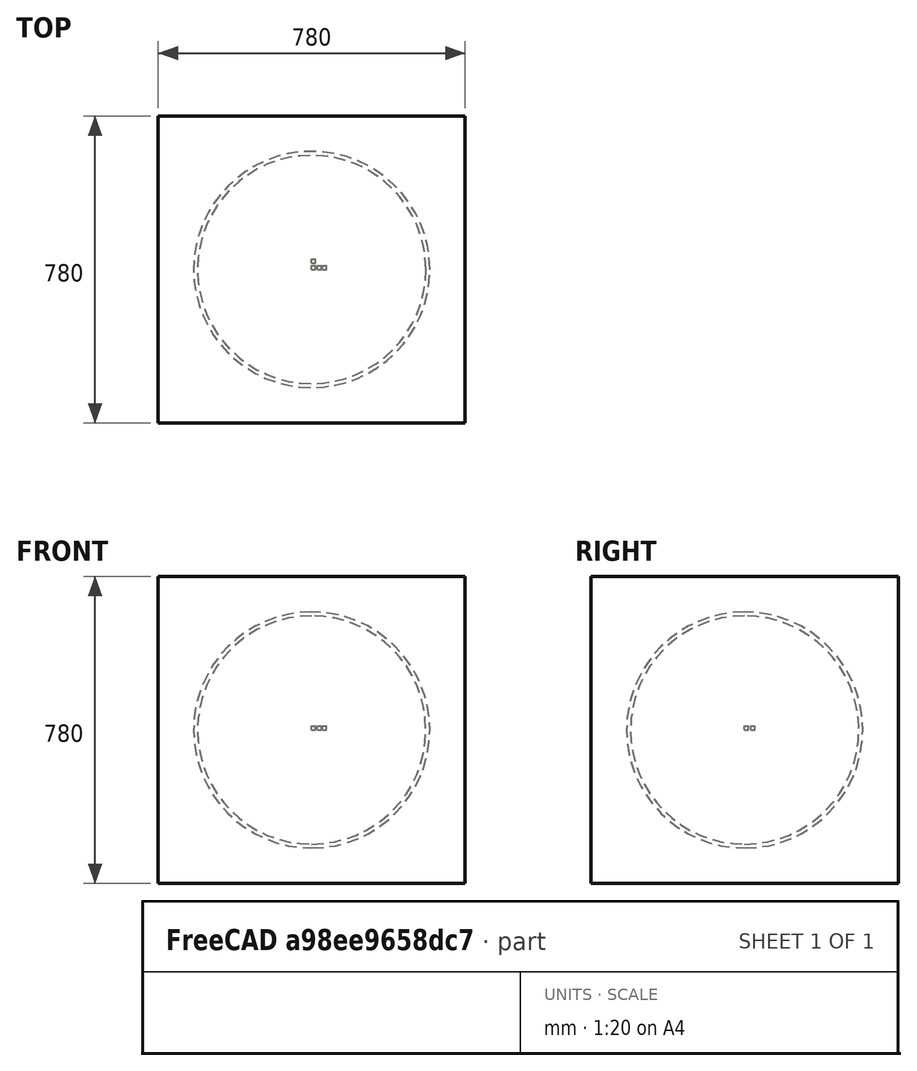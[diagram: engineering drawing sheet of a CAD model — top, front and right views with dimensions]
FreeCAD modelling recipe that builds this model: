
FCSTD DOCUMENT  (FreeCAD 0.20RUnknown)
Label: myTestExperiment_equivalent
License: All rights reserved
objects: App::DocumentObjectGroupPython×1251, App::Part×7, Part::FeaturePython×6, Part::Box×4
note: 6 computed .brp shape members not serialized (recipe doc carries the construction recipe); baked Part::Feature solids carry a one-line shape summary decoded from their .brp

FEATURE [App::DocumentObjectGroupPython] HALFPI  # scripted group (container) (typed FeaturePython)
  name = HALFPI
  value = pi/2.
FEATURE [App::DocumentObjectGroupPython] PI  # scripted group (container) (typed FeaturePython)
  name = PI
  value = 1.*pi
FEATURE [App::DocumentObjectGroupPython] TWOPI  # scripted group (container) (typed FeaturePython)
  name = TWOPI
  value = 2.*pi
FEATURE [App::DocumentObjectGroupPython] Constants  # scripted group (container) (typed FeaturePython)
  Group = -> [HALFPI,PI,TWOPI]
FEATURE [App::DocumentObjectGroupPython] Variables  # scripted group (container) (typed FeaturePython)
FEATURE [App::DocumentObjectGroupPython] Quantities  # scripted group (container) (typed FeaturePython)
FEATURE [App::DocumentObjectGroupPython] Isotopes  # scripted group (container) (typed FeaturePython)
FEATURE [App::DocumentObjectGroupPython] Elements  # scripted group (container) (typed FeaturePython)
FEATURE [App::DocumentObjectGroupPython] Matrix  # scripted group (container) (typed FeaturePython)
FEATURE [App::DocumentObjectGroupPython] Surfaces  # scripted group (container) (typed FeaturePython)
FEATURE [App::DocumentObjectGroupPython] Opticals  # scripted group (container) (typed FeaturePython)
  Group = -> [Matrix,Surfaces]
FEATURE [App::DocumentObjectGroupPython] G4Isotopes  # scripted group (container) (typed FeaturePython)
FEATURE [App::DocumentObjectGroupPython] H_element  # scripted group (container) (typed FeaturePython)
  Z = 1
  atom_value = 1.008
  formula = H
  name = H_element
FEATURE [App::DocumentObjectGroupPython] He_element  # scripted group (container) (typed FeaturePython)
  Z = 2
  atom_value = 4.0026
  formula = He
  name = He_element
FEATURE [App::DocumentObjectGroupPython] Li_element  # scripted group (container) (typed FeaturePython)
  Z = 3
  atom_value = 6.94
  formula = Li
  name = Li_element
FEATURE [App::DocumentObjectGroupPython] Be_element  # scripted group (container) (typed FeaturePython)
  Z = 4
  atom_value = 9.01218
  formula = Be
  name = Be_element
FEATURE [App::DocumentObjectGroupPython] B_element  # scripted group (container) (typed FeaturePython)
  Z = 5
  atom_value = 10.81
  formula = B
  name = B_element
FEATURE [App::DocumentObjectGroupPython] C_element  # scripted group (container) (typed FeaturePython)
  Z = 6
  atom_value = 12.011
  formula = C
  name = C_element
FEATURE [App::DocumentObjectGroupPython] N_element  # scripted group (container) (typed FeaturePython)
  Z = 7
  atom_value = 14.007
  formula = N
  name = N_element
FEATURE [App::DocumentObjectGroupPython] O_element  # scripted group (container) (typed FeaturePython)
  Z = 8
  atom_value = 15.999
  formula = O
  name = O_element
FEATURE [App::DocumentObjectGroupPython] F_element  # scripted group (container) (typed FeaturePython)
  Z = 9
  atom_value = 18.9984
  formula = F
  name = F_element
FEATURE [App::DocumentObjectGroupPython] Ne_element  # scripted group (container) (typed FeaturePython)
  Z = 10
  atom_value = 20.1797
  formula = Ne
  name = Ne_element
FEATURE [App::DocumentObjectGroupPython] Na_element  # scripted group (container) (typed FeaturePython)
  Z = 11
  atom_value = 22.9898
  formula = Na
  name = Na_element
FEATURE [App::DocumentObjectGroupPython] Mg_element  # scripted group (container) (typed FeaturePython)
  Z = 12
  atom_value = 24.305
  formula = Mg
  name = Mg_element
FEATURE [App::DocumentObjectGroupPython] Al_element  # scripted group (container) (typed FeaturePython)
  Z = 13
  atom_value = 26.9815
  formula = Al
  name = Al_element
FEATURE [App::DocumentObjectGroupPython] Si_element  # scripted group (container) (typed FeaturePython)
  Z = 14
  atom_value = 28.085
  formula = Si
  name = Si_element
FEATURE [App::DocumentObjectGroupPython] P_element  # scripted group (container) (typed FeaturePython)
  Z = 15
  atom_value = 30.9738
  formula = P
  name = P_element
FEATURE [App::DocumentObjectGroupPython] S_element  # scripted group (container) (typed FeaturePython)
  Z = 16
  atom_value = 32.06
  formula = S
  name = S_element
FEATURE [App::DocumentObjectGroupPython] Cl_element  # scripted group (container) (typed FeaturePython)
  Z = 17
  atom_value = 35.45
  formula = Cl
  name = Cl_element
FEATURE [App::DocumentObjectGroupPython] Ar_element  # scripted group (container) (typed FeaturePython)
  Z = 18
  atom_value = 39.95
  formula = Ar
  name = Ar_element
FEATURE [App::DocumentObjectGroupPython] K_element  # scripted group (container) (typed FeaturePython)
  Z = 19
  atom_value = 39.0983
  formula = K
  name = K_element
FEATURE [App::DocumentObjectGroupPython] Ca_element  # scripted group (container) (typed FeaturePython)
  Z = 20
  atom_value = 40.078
  formula = Ca
  name = Ca_element
FEATURE [App::DocumentObjectGroupPython] Sc_element  # scripted group (container) (typed FeaturePython)
  Z = 21
  atom_value = 44.9559
  formula = Sc
  name = Sc_element
FEATURE [App::DocumentObjectGroupPython] Ti_element  # scripted group (container) (typed FeaturePython)
  Z = 22
  atom_value = 47.867
  formula = Ti
  name = Ti_element
FEATURE [App::DocumentObjectGroupPython] V_element  # scripted group (container) (typed FeaturePython)
  Z = 23
  atom_value = 50.9415
  formula = V
  name = V_element
FEATURE [App::DocumentObjectGroupPython] Cr_element  # scripted group (container) (typed FeaturePython)
  Z = 24
  atom_value = 51.9961
  formula = Cr
  name = Cr_element
FEATURE [App::DocumentObjectGroupPython] Mn_element  # scripted group (container) (typed FeaturePython)
  Z = 25
  atom_value = 54.938
  formula = Mn
  name = Mn_element
FEATURE [App::DocumentObjectGroupPython] Fe_element  # scripted group (container) (typed FeaturePython)
  Z = 26
  atom_value = 55.845
  formula = Fe
  name = Fe_element
FEATURE [App::DocumentObjectGroupPython] Co_element  # scripted group (container) (typed FeaturePython)
  Z = 27
  atom_value = 58.9332
  formula = Co
  name = Co_element
FEATURE [App::DocumentObjectGroupPython] Ni_element  # scripted group (container) (typed FeaturePython)
  Z = 28
  atom_value = 58.6934
  formula = Ni
  name = Ni_element
FEATURE [App::DocumentObjectGroupPython] Cu_element  # scripted group (container) (typed FeaturePython)
  Z = 29
  atom_value = 63.546
  formula = Cu
  name = Cu_element
FEATURE [App::DocumentObjectGroupPython] Zn_element  # scripted group (container) (typed FeaturePython)
  Z = 30
  atom_value = 65.38
  formula = Zn
  name = Zn_element
FEATURE [App::DocumentObjectGroupPython] Ga_element  # scripted group (container) (typed FeaturePython)
  Z = 31
  atom_value = 69.723
  formula = Ga
  name = Ga_element
FEATURE [App::DocumentObjectGroupPython] Ge_element  # scripted group (container) (typed FeaturePython)
  Z = 32
  atom_value = 72.63
  formula = Ge
  name = Ge_element
FEATURE [App::DocumentObjectGroupPython] As_element  # scripted group (container) (typed FeaturePython)
  Z = 33
  atom_value = 74.9216
  formula = As
  name = As_element
FEATURE [App::DocumentObjectGroupPython] Se_element  # scripted group (container) (typed FeaturePython)
  Z = 34
  atom_value = 78.971
  formula = Se
  name = Se_element
FEATURE [App::DocumentObjectGroupPython] Br_element  # scripted group (container) (typed FeaturePython)
  Z = 35
  atom_value = 79.904
  formula = Br
  name = Br_element
FEATURE [App::DocumentObjectGroupPython] Kr_element  # scripted group (container) (typed FeaturePython)
  Z = 36
  atom_value = 83.798
  formula = Kr
  name = Kr_element
FEATURE [App::DocumentObjectGroupPython] Rb_element  # scripted group (container) (typed FeaturePython)
  Z = 37
  atom_value = 85.4678
  formula = Rb
  name = Rb_element
FEATURE [App::DocumentObjectGroupPython] Sr_element  # scripted group (container) (typed FeaturePython)
  Z = 38
  atom_value = 87.62
  formula = Sr
  name = Sr_element
FEATURE [App::DocumentObjectGroupPython] Y_element  # scripted group (container) (typed FeaturePython)
  Z = 39
  atom_value = 88.9058
  formula = Y
  name = Y_element
FEATURE [App::DocumentObjectGroupPython] Zr_element  # scripted group (container) (typed FeaturePython)
  Z = 40
  atom_value = 91.224
  formula = Zr
  name = Zr_element
FEATURE [App::DocumentObjectGroupPython] Nb_element  # scripted group (container) (typed FeaturePython)
  Z = 41
  atom_value = 92.9064
  formula = Nb
  name = Nb_element
FEATURE [App::DocumentObjectGroupPython] Mo_element  # scripted group (container) (typed FeaturePython)
  Z = 42
  atom_value = 95.95
  formula = Mo
  name = Mo_element
FEATURE [App::DocumentObjectGroupPython] Tc_element  # scripted group (container) (typed FeaturePython)
  Z = 43
  atom_value = 97
  formula = Tc
  name = Tc_element
FEATURE [App::DocumentObjectGroupPython] Ru_element  # scripted group (container) (typed FeaturePython)
  Z = 44
  atom_value = 101.07
  formula = Ru
  name = Ru_element
FEATURE [App::DocumentObjectGroupPython] Rh_element  # scripted group (container) (typed FeaturePython)
  Z = 45
  atom_value = 102.905
  formula = Rh
  name = Rh_element
FEATURE [App::DocumentObjectGroupPython] Pd_element  # scripted group (container) (typed FeaturePython)
  Z = 46
  atom_value = 106.42
  formula = Pd
  name = Pd_element
FEATURE [App::DocumentObjectGroupPython] Ag_element  # scripted group (container) (typed FeaturePython)
  Z = 47
  atom_value = 107.868
  formula = Ag
  name = Ag_element
FEATURE [App::DocumentObjectGroupPython] Cd_element  # scripted group (container) (typed FeaturePython)
  Z = 48
  atom_value = 112.414
  formula = Cd
  name = Cd_element
FEATURE [App::DocumentObjectGroupPython] In_element  # scripted group (container) (typed FeaturePython)
  Z = 49
  atom_value = 114.818
  formula = In
  name = In_element
FEATURE [App::DocumentObjectGroupPython] Sn_element  # scripted group (container) (typed FeaturePython)
  Z = 50
  atom_value = 118.71
  formula = Sn
  name = Sn_element
FEATURE [App::DocumentObjectGroupPython] Sb_element  # scripted group (container) (typed FeaturePython)
  Z = 51
  atom_value = 121.76
  formula = Sb
  name = Sb_element
FEATURE [App::DocumentObjectGroupPython] Te_element  # scripted group (container) (typed FeaturePython)
  Z = 52
  atom_value = 127.6
  formula = Te
  name = Te_element
FEATURE [App::DocumentObjectGroupPython] I_element  # scripted group (container) (typed FeaturePython)
  Z = 53
  atom_value = 126.904
  formula = I
  name = I_element
FEATURE [App::DocumentObjectGroupPython] Xe_element  # scripted group (container) (typed FeaturePython)
  Z = 54
  atom_value = 131.293
  formula = Xe
  name = Xe_element
FEATURE [App::DocumentObjectGroupPython] Cs_element  # scripted group (container) (typed FeaturePython)
  Z = 55
  atom_value = 132.905
  formula = Cs
  name = Cs_element
FEATURE [App::DocumentObjectGroupPython] Ba_element  # scripted group (container) (typed FeaturePython)
  Z = 56
  atom_value = 137.327
  formula = Ba
  name = Ba_element
FEATURE [App::DocumentObjectGroupPython] La_element  # scripted group (container) (typed FeaturePython)
  Z = 57
  atom_value = 138.905
  formula = La
  name = La_element
FEATURE [App::DocumentObjectGroupPython] Ce_element  # scripted group (container) (typed FeaturePython)
  Z = 58
  atom_value = 140.116
  formula = Ce
  name = Ce_element
FEATURE [App::DocumentObjectGroupPython] Pr_element  # scripted group (container) (typed FeaturePython)
  Z = 59
  atom_value = 140.908
  formula = Pr
  name = Pr_element
FEATURE [App::DocumentObjectGroupPython] Nd_element  # scripted group (container) (typed FeaturePython)
  Z = 60
  atom_value = 144.242
  formula = Nd
  name = Nd_element
FEATURE [App::DocumentObjectGroupPython] Pm_element  # scripted group (container) (typed FeaturePython)
  Z = 61
  atom_value = 145
  formula = Pm
  name = Pm_element
FEATURE [App::DocumentObjectGroupPython] Sm_element  # scripted group (container) (typed FeaturePython)
  Z = 62
  atom_value = 150.36
  formula = Sm
  name = Sm_element
FEATURE [App::DocumentObjectGroupPython] Eu_element  # scripted group (container) (typed FeaturePython)
  Z = 63
  atom_value = 151.964
  formula = Eu
  name = Eu_element
FEATURE [App::DocumentObjectGroupPython] Gd_element  # scripted group (container) (typed FeaturePython)
  Z = 64
  atom_value = 157.25
  formula = Gd
  name = Gd_element
FEATURE [App::DocumentObjectGroupPython] Tb_element  # scripted group (container) (typed FeaturePython)
  Z = 65
  atom_value = 158.925
  formula = Tb
  name = Tb_element
FEATURE [App::DocumentObjectGroupPython] Dy_element  # scripted group (container) (typed FeaturePython)
  Z = 66
  atom_value = 162.5
  formula = Dy
  name = Dy_element
FEATURE [App::DocumentObjectGroupPython] Ho_element  # scripted group (container) (typed FeaturePython)
  Z = 67
  atom_value = 164.93
  formula = Ho
  name = Ho_element
FEATURE [App::DocumentObjectGroupPython] Er_element  # scripted group (container) (typed FeaturePython)
  Z = 68
  atom_value = 167.259
  formula = Er
  name = Er_element
FEATURE [App::DocumentObjectGroupPython] Tm_element  # scripted group (container) (typed FeaturePython)
  Z = 69
  atom_value = 168.934
  formula = Tm
  name = Tm_element
FEATURE [App::DocumentObjectGroupPython] Yb_element  # scripted group (container) (typed FeaturePython)
  Z = 70
  atom_value = 173.045
  formula = Yb
  name = Yb_element
FEATURE [App::DocumentObjectGroupPython] Lu_element  # scripted group (container) (typed FeaturePython)
  Z = 71
  atom_value = 174.967
  formula = Lu
  name = Lu_element
FEATURE [App::DocumentObjectGroupPython] Hf_element  # scripted group (container) (typed FeaturePython)
  Z = 72
  atom_value = 178.49
  formula = Hf
  name = Hf_element
FEATURE [App::DocumentObjectGroupPython] Ta_element  # scripted group (container) (typed FeaturePython)
  Z = 73
  atom_value = 180.948
  formula = Ta
  name = Ta_element
FEATURE [App::DocumentObjectGroupPython] W_element  # scripted group (container) (typed FeaturePython)
  Z = 74
  atom_value = 183.84
  formula = W
  name = W_element
FEATURE [App::DocumentObjectGroupPython] Re_element  # scripted group (container) (typed FeaturePython)
  Z = 75
  atom_value = 186.207
  formula = Re
  name = Re_element
FEATURE [App::DocumentObjectGroupPython] Os_element  # scripted group (container) (typed FeaturePython)
  Z = 76
  atom_value = 190.23
  formula = Os
  name = Os_element
FEATURE [App::DocumentObjectGroupPython] Ir_element  # scripted group (container) (typed FeaturePython)
  Z = 77
  atom_value = 192.217
  formula = Ir
  name = Ir_element
FEATURE [App::DocumentObjectGroupPython] Pt_element  # scripted group (container) (typed FeaturePython)
  Z = 78
  atom_value = 195.084
  formula = Pt
  name = Pt_element
FEATURE [App::DocumentObjectGroupPython] Au_element  # scripted group (container) (typed FeaturePython)
  Z = 79
  atom_value = 196.967
  formula = Au
  name = Au_element
FEATURE [App::DocumentObjectGroupPython] Hg_element  # scripted group (container) (typed FeaturePython)
  Z = 80
  atom_value = 200.592
  formula = Hg
  name = Hg_element
FEATURE [App::DocumentObjectGroupPython] Tl_element  # scripted group (container) (typed FeaturePython)
  Z = 81
  atom_value = 204.38
  formula = Tl
  name = Tl_element
FEATURE [App::DocumentObjectGroupPython] Pb_element  # scripted group (container) (typed FeaturePython)
  Z = 82
  atom_value = 207.2
  formula = Pb
  name = Pb_element
FEATURE [App::DocumentObjectGroupPython] Bi_element  # scripted group (container) (typed FeaturePython)
  Z = 83
  atom_value = 208.98
  formula = Bi
  name = Bi_element
FEATURE [App::DocumentObjectGroupPython] Po_element  # scripted group (container) (typed FeaturePython)
  Z = 84
  atom_value = 209
  formula = Po
  name = Po_element
FEATURE [App::DocumentObjectGroupPython] At_element  # scripted group (container) (typed FeaturePython)
  Z = 85
  atom_value = 210
  formula = At
  name = At_element
FEATURE [App::DocumentObjectGroupPython] Rn_element  # scripted group (container) (typed FeaturePython)
  Z = 86
  atom_value = 222
  formula = Rn
  name = Rn_element
FEATURE [App::DocumentObjectGroupPython] Fr_element  # scripted group (container) (typed FeaturePython)
  Z = 87
  atom_value = 223
  formula = Fr
  name = Fr_element
FEATURE [App::DocumentObjectGroupPython] Ra_element  # scripted group (container) (typed FeaturePython)
  Z = 88
  atom_value = 226
  formula = Ra
  name = Ra_element
FEATURE [App::DocumentObjectGroupPython] Ac_element  # scripted group (container) (typed FeaturePython)
  Z = 89
  atom_value = 227
  formula = Ac
  name = Ac_element
FEATURE [App::DocumentObjectGroupPython] Th_element  # scripted group (container) (typed FeaturePython)
  Z = 90
  atom_value = 232.038
  formula = Th
  name = Th_element
FEATURE [App::DocumentObjectGroupPython] Pa_element  # scripted group (container) (typed FeaturePython)
  Z = 91
  atom_value = 231.036
  formula = Pa
  name = Pa_element
FEATURE [App::DocumentObjectGroupPython] U_element  # scripted group (container) (typed FeaturePython)
  Z = 92
  atom_value = 238.029
  formula = U
  name = U_element
FEATURE [App::DocumentObjectGroupPython] Np_element  # scripted group (container) (typed FeaturePython)
  Z = 93
  atom_value = 237
  formula = Np
  name = Np_element
FEATURE [App::DocumentObjectGroupPython] Pu_element  # scripted group (container) (typed FeaturePython)
  Z = 94
  atom_value = 244
  formula = Pu
  name = Pu_element
FEATURE [App::DocumentObjectGroupPython] Am_element  # scripted group (container) (typed FeaturePython)
  Z = 95
  atom_value = 243
  formula = Am
  name = Am_element
FEATURE [App::DocumentObjectGroupPython] Cm_element  # scripted group (container) (typed FeaturePython)
  Z = 96
  atom_value = 247
  formula = Cm
  name = Cm_element
FEATURE [App::DocumentObjectGroupPython] Bk_element  # scripted group (container) (typed FeaturePython)
  Z = 97
  atom_value = 247
  formula = Bk
  name = Bk_element
FEATURE [App::DocumentObjectGroupPython] Cf_element  # scripted group (container) (typed FeaturePython)
  Z = 98
  atom_value = 251
  formula = Cf
  name = Cf_element
FEATURE [App::DocumentObjectGroupPython] G4Elements  # scripted group (container) (typed FeaturePython)
  Group = -> [H_element,He_element,Li_element,Be_element,B_element,C_element,N_element,O_element,F_element,Ne_element,Na_element,Mg_element,Al_element,Si_element,P_element,S_element,Cl_element,Ar_element,K_element,Ca_element,Sc_element,Ti_element,V_element,Cr_element,Mn_element,Fe_element,Co_element,Ni_element,Cu_element,Zn_element,Ga_element,Ge_element,As_element,Se_element,Br_element,Kr_element,Rb_element,+61 more]
FEATURE [App::DocumentObjectGroupPython] H_element001  label="H_element : 0.101"  # scripted group (container) (typed FeaturePython)
  n = 0.101327
FEATURE [App::DocumentObjectGroupPython] C_element001  label="C_element : 0.775"  # scripted group (container) (typed FeaturePython)
  n = 0.7755
FEATURE [App::DocumentObjectGroupPython] N_element001  label="N_element : 0.035"  # scripted group (container) (typed FeaturePython)
  n = 0.035057
FEATURE [App::DocumentObjectGroupPython] O_element001  label="O_element : 0.052"  # scripted group (container) (typed FeaturePython)
  n = 0.0523159
FEATURE [App::DocumentObjectGroupPython] F_element001  label="F_element : 0.017"  # scripted group (container) (typed FeaturePython)
  n = 0.017422
FEATURE [App::DocumentObjectGroupPython] Ca_element001  label="Ca_element : 0.018"  # scripted group (container) (typed FeaturePython)
  n = 0.018378
FEATURE [App::DocumentObjectGroupPython] G4_A_150_TISSUE  label="G4_A-150_TISSUE"  # scripted group (container) (typed FeaturePython)
  Dunit = g/cm3
  Dvalue = 1.127
  Group = -> [H_element001,C_element001,N_element001,O_element001,F_element001,Ca_element001]
  conduct = 2
  density = 1
  expand = 3
  formula = G4_A-150_TISSUE
  name = G4_A-150_TISSUE
  specific = 4
FEATURE [App::DocumentObjectGroupPython] C_element002  label="C_element : 3"  # scripted group (container) (typed FeaturePython)
  n = 3
  ref = C_element
FEATURE [App::DocumentObjectGroupPython] H_element002  label="H_element : 6"  # scripted group (container) (typed FeaturePython)
  n = 6
  ref = H_element
FEATURE [App::DocumentObjectGroupPython] O_element002  label="O_element : 1"  # scripted group (container) (typed FeaturePython)
  n = 1
  ref = O_element
FEATURE [App::DocumentObjectGroupPython] G4_ACETONE  # scripted group (container) (typed FeaturePython)
  Dunit = g/cm3
  Dvalue = 0.7899
  Group = -> [C_element002,H_element002,O_element002]
  conduct = 2
  density = 1
  expand = 3
  formula = G4_ACETONE
  name = G4_ACETONE
  specific = 4
FEATURE [App::DocumentObjectGroupPython] C_element003  label="C_element : 2"  # scripted group (container) (typed FeaturePython)
  n = 2
  ref = C_element
FEATURE [App::DocumentObjectGroupPython] H_element003  label="H_element : 2"  # scripted group (container) (typed FeaturePython)
  n = 2
  ref = H_element
FEATURE [App::DocumentObjectGroupPython] G4_ACETYLENE  # scripted group (container) (typed FeaturePython)
  Dunit = g/cm3
  Dvalue = 0.0010967
  Group = -> [C_element003,H_element003]
  conduct = 2
  density = 1
  expand = 3
  formula = G4_ACETYLENE
  name = G4_ACETYLENE
  specific = 4
FEATURE [App::DocumentObjectGroupPython] C_element004  label="C_element : 5"  # scripted group (container) (typed FeaturePython)
  n = 5
  ref = C_element
FEATURE [App::DocumentObjectGroupPython] H_element004  label="H_element : 5"  # scripted group (container) (typed FeaturePython)
  n = 5
  ref = H_element
FEATURE [App::DocumentObjectGroupPython] N_element002  label="N_element : 5"  # scripted group (container) (typed FeaturePython)
  n = 5
  ref = N_element
FEATURE [App::DocumentObjectGroupPython] G4_ADENINE  # scripted group (container) (typed FeaturePython)
  Dunit = g/cm3
  Dvalue = 1.6
  Group = -> [C_element004,H_element004,N_element002]
  conduct = 2
  density = 1
  expand = 3
  formula = G4_ADENINE
  name = G4_ADENINE
  specific = 4
FEATURE [App::DocumentObjectGroupPython] H_element005  label="H_element : 0.114"  # scripted group (container) (typed FeaturePython)
  n = 0.114
FEATURE [App::DocumentObjectGroupPython] C_element005  label="C_element : 0.598"  # scripted group (container) (typed FeaturePython)
  n = 0.598
FEATURE [App::DocumentObjectGroupPython] N_element003  label="N_element : 0.007"  # scripted group (container) (typed FeaturePython)
  n = 0.007
FEATURE [App::DocumentObjectGroupPython] O_element003  label="O_element : 0.278"  # scripted group (container) (typed FeaturePython)
  n = 0.278
FEATURE [App::DocumentObjectGroupPython] Na_element001  label="Na_element : 0.001"  # scripted group (container) (typed FeaturePython)
  n = 0.001
FEATURE [App::DocumentObjectGroupPython] S_element001  label="S_element : 0.001"  # scripted group (container) (typed FeaturePython)
  n = 0.001
FEATURE [App::DocumentObjectGroupPython] Cl_element001  label="Cl_element : 0.001"  # scripted group (container) (typed FeaturePython)
  n = 0.001
FEATURE [App::DocumentObjectGroupPython] G4_ADIPOSE_TISSUE_ICRP  # scripted group (container) (typed FeaturePython)
  Dunit = g/cm3
  Dvalue = 0.95
  Group = -> [H_element005,C_element005,N_element003,O_element003,Na_element001,S_element001,Cl_element001]
  conduct = 2
  density = 1
  expand = 3
  formula = G4_ADIPOSE_TISSUE_ICRP
  name = G4_ADIPOSE_TISSUE_ICRP
  specific = 4
FEATURE [App::DocumentObjectGroupPython] C_element006  label="C_element : 0.000"  # scripted group (container) (typed FeaturePython)
  n = 0.000124
FEATURE [App::DocumentObjectGroupPython] N_element004  label="N_element : 0.755"  # scripted group (container) (typed FeaturePython)
  n = 0.755268
FEATURE [App::DocumentObjectGroupPython] O_element004  label="O_element : 0.232"  # scripted group (container) (typed FeaturePython)
  n = 0.231781
FEATURE [App::DocumentObjectGroupPython] Ar_element001  label="Ar_element : 0.013"  # scripted group (container) (typed FeaturePython)
  n = 0.012827
FEATURE [App::DocumentObjectGroupPython] G4_AIR  # scripted group (container) (typed FeaturePython)
  Dunit = g/cm3
  Dvalue = 0.00120479
  Group = -> [C_element006,N_element004,O_element004,Ar_element001]
  conduct = 2
  density = 1
  expand = 3
  formula = G4_AIR
  name = G4_AIR
  specific = 4
FEATURE [App::DocumentObjectGroupPython] C_element007  label="C_element : 006"  # scripted group (container) (typed FeaturePython)
  n = 3
  ref = C_element
FEATURE [App::DocumentObjectGroupPython] H_element006  label="H_element : 7"  # scripted group (container) (typed FeaturePython)
  n = 7
  ref = H_element
FEATURE [App::DocumentObjectGroupPython] N_element005  label="N_element : 1"  # scripted group (container) (typed FeaturePython)
  n = 1
  ref = N_element
FEATURE [App::DocumentObjectGroupPython] O_element005  label="O_element : 2"  # scripted group (container) (typed FeaturePython)
  n = 2
  ref = O_element
FEATURE [App::DocumentObjectGroupPython] G4_ALANINE  # scripted group (container) (typed FeaturePython)
  Dunit = g/cm3
  Dvalue = 1.42
  Group = -> [C_element007,H_element006,N_element005,O_element005]
  conduct = 2
  density = 1
  expand = 3
  formula = G4_ALANINE
  name = G4_ALANINE
  specific = 4
FEATURE [App::DocumentObjectGroupPython] Al_element001  label="Al_element : 2"  # scripted group (container) (typed FeaturePython)
  n = 2
  ref = Al_element
FEATURE [App::DocumentObjectGroupPython] O_element006  label="O_element : 3"  # scripted group (container) (typed FeaturePython)
  n = 3
  ref = O_element
FEATURE [App::DocumentObjectGroupPython] G4_ALUMINUM_OXIDE  # scripted group (container) (typed FeaturePython)
  Dunit = g/cm3
  Dvalue = 3.97
  Group = -> [Al_element001,O_element006]
  conduct = 2
  density = 1
  expand = 3
  formula = G4_ALUMINUM_OXIDE
  name = G4_ALUMINUM_OXIDE
  specific = 4
FEATURE [App::DocumentObjectGroupPython] H_element007  label="H_element : 0.106"  # scripted group (container) (typed FeaturePython)
  n = 0.10593
FEATURE [App::DocumentObjectGroupPython] C_element008  label="C_element : 0.789"  # scripted group (container) (typed FeaturePython)
  n = 0.788974
FEATURE [App::DocumentObjectGroupPython] O_element007  label="O_element : 0.105"  # scripted group (container) (typed FeaturePython)
  n = 0.105096
FEATURE [App::DocumentObjectGroupPython] G4_AMBER  # scripted group (container) (typed FeaturePython)
  Dunit = g/cm3
  Dvalue = 1.1
  Group = -> [H_element007,C_element008,O_element007]
  conduct = 2
  density = 1
  expand = 3
  formula = G4_AMBER
  name = G4_AMBER
  specific = 4
FEATURE [App::DocumentObjectGroupPython] N_element006  label="N_element : 006"  # scripted group (container) (typed FeaturePython)
  n = 1
  ref = N_element
FEATURE [App::DocumentObjectGroupPython] H_element008  label="H_element : 3"  # scripted group (container) (typed FeaturePython)
  n = 3
  ref = H_element
FEATURE [App::DocumentObjectGroupPython] G4_AMMONIA  # scripted group (container) (typed FeaturePython)
  Dunit = g/cm3
  Dvalue = 0.000826019
  Group = -> [N_element006,H_element008]
  conduct = 2
  density = 1
  expand = 3
  formula = G4_AMMONIA
  name = G4_AMMONIA
  specific = 4
FEATURE [App::DocumentObjectGroupPython] C_element009  label="C_element : 6"  # scripted group (container) (typed FeaturePython)
  n = 6
  ref = C_element
FEATURE [App::DocumentObjectGroupPython] H_element009  label="H_element : 008"  # scripted group (container) (typed FeaturePython)
  n = 7
  ref = H_element
FEATURE [App::DocumentObjectGroupPython] N_element007  label="N_element : 007"  # scripted group (container) (typed FeaturePython)
  n = 1
  ref = N_element
FEATURE [App::DocumentObjectGroupPython] G4_ANILINE  # scripted group (container) (typed FeaturePython)
  Dunit = g/cm3
  Dvalue = 1.0235
  Group = -> [C_element009,H_element009,N_element007]
  conduct = 2
  density = 1
  expand = 3
  formula = G4_ANILINE
  name = G4_ANILINE
  specific = 4
FEATURE [App::DocumentObjectGroupPython] C_element010  label="C_element : 14"  # scripted group (container) (typed FeaturePython)
  n = 14
  ref = C_element
FEATURE [App::DocumentObjectGroupPython] H_element010  label="H_element : 10"  # scripted group (container) (typed FeaturePython)
  n = 10
  ref = H_element
FEATURE [App::DocumentObjectGroupPython] G4_ANTHRACENE  # scripted group (container) (typed FeaturePython)
  Dunit = g/cm3
  Dvalue = 1.283
  Group = -> [C_element010,H_element010]
  conduct = 2
  density = 1
  expand = 3
  formula = G4_ANTHRACENE
  name = G4_ANTHRACENE
  specific = 4
FEATURE [App::DocumentObjectGroupPython] H_element011  label="H_element : 0.065"  # scripted group (container) (typed FeaturePython)
  n = 0.0654709
FEATURE [App::DocumentObjectGroupPython] C_element011  label="C_element : 0.537"  # scripted group (container) (typed FeaturePython)
  n = 0.536944
FEATURE [App::DocumentObjectGroupPython] N_element008  label="N_element : 0.021"  # scripted group (container) (typed FeaturePython)
  n = 0.0215
FEATURE [App::DocumentObjectGroupPython] O_element008  label="O_element : 0.032"  # scripted group (container) (typed FeaturePython)
  n = 0.032085
FEATURE [App::DocumentObjectGroupPython] F_element002  label="F_element : 0.167"  # scripted group (container) (typed FeaturePython)
  n = 0.167411
FEATURE [App::DocumentObjectGroupPython] Ca_element002  label="Ca_element : 0.177"  # scripted group (container) (typed FeaturePython)
  n = 0.176589
FEATURE [App::DocumentObjectGroupPython] G4_B_100_BONE  label="G4_B-100_BONE"  # scripted group (container) (typed FeaturePython)
  Dunit = g/cm3
  Dvalue = 1.45
  Group = -> [H_element011,C_element011,N_element008,O_element008,F_element002,Ca_element002]
  conduct = 2
  density = 1
  expand = 3
  formula = G4_B-100_BONE
  name = G4_B-100_BONE
  specific = 4
FEATURE [App::DocumentObjectGroupPython] H_element012  label="H_element : 0.057"  # scripted group (container) (typed FeaturePython)
  n = 0.057441
FEATURE [App::DocumentObjectGroupPython] C_element012  label="C_element : 0.790"  # scripted group (container) (typed FeaturePython)
  n = 0.774591
FEATURE [App::DocumentObjectGroupPython] O_element009  label="O_element : 0.168"  # scripted group (container) (typed FeaturePython)
  n = 0.167968
FEATURE [App::DocumentObjectGroupPython] G4_BAKELITE  # scripted group (container) (typed FeaturePython)
  Dunit = g/cm3
  Dvalue = 1.25
  Group = -> [H_element012,C_element012,O_element009]
  conduct = 2
  density = 1
  expand = 3
  formula = G4_BAKELITE
  name = G4_BAKELITE
  specific = 4
FEATURE [App::DocumentObjectGroupPython] Ba_element001  label="Ba_element : 1"  # scripted group (container) (typed FeaturePython)
  n = 1
  ref = Ba_element
FEATURE [App::DocumentObjectGroupPython] F_element003  label="F_element : 2"  # scripted group (container) (typed FeaturePython)
  n = 2
  ref = F_element
FEATURE [App::DocumentObjectGroupPython] G4_BARIUM_FLUORIDE  # scripted group (container) (typed FeaturePython)
  Dunit = g/cm3
  Dvalue = 4.89
  Group = -> [Ba_element001,F_element003]
  conduct = 2
  density = 1
  expand = 3
  formula = G4_BARIUM_FLUORIDE
  name = G4_BARIUM_FLUORIDE
  specific = 4
FEATURE [App::DocumentObjectGroupPython] Ba_element002  label="Ba_element : 002"  # scripted group (container) (typed FeaturePython)
  n = 1
  ref = Ba_element
FEATURE [App::DocumentObjectGroupPython] S_element002  label="S_element : 1"  # scripted group (container) (typed FeaturePython)
  n = 1
  ref = S_element
FEATURE [App::DocumentObjectGroupPython] O_element010  label="O_element : 4"  # scripted group (container) (typed FeaturePython)
  n = 4
  ref = O_element
FEATURE [App::DocumentObjectGroupPython] G4_BARIUM_SULFATE  # scripted group (container) (typed FeaturePython)
  Dunit = g/cm3
  Dvalue = 4.5
  Group = -> [Ba_element002,S_element002,O_element010]
  conduct = 2
  density = 1
  expand = 3
  formula = G4_BARIUM_SULFATE
  name = G4_BARIUM_SULFATE
  specific = 4
FEATURE [App::DocumentObjectGroupPython] C_element013  label="C_element : 007"  # scripted group (container) (typed FeaturePython)
  n = 6
  ref = C_element
FEATURE [App::DocumentObjectGroupPython] H_element013  label="H_element : 009"  # scripted group (container) (typed FeaturePython)
  n = 6
  ref = H_element
FEATURE [App::DocumentObjectGroupPython] G4_BENZENE  # scripted group (container) (typed FeaturePython)
  Dunit = g/cm3
  Dvalue = 0.87865
  Group = -> [C_element013,H_element013]
  conduct = 2
  density = 1
  expand = 3
  formula = G4_BENZENE
  name = G4_BENZENE
  specific = 4
FEATURE [App::DocumentObjectGroupPython] Be_element001  label="Be_element : 1"  # scripted group (container) (typed FeaturePython)
  n = 1
  ref = Be_element
FEATURE [App::DocumentObjectGroupPython] O_element011  label="O_element : 005"  # scripted group (container) (typed FeaturePython)
  n = 1
  ref = O_element
FEATURE [App::DocumentObjectGroupPython] G4_BERYLLIUM_OXIDE  # scripted group (container) (typed FeaturePython)
  Dunit = g/cm3
  Dvalue = 3.01
  Group = -> [Be_element001,O_element011]
  conduct = 2
  density = 1
  expand = 3
  formula = G4_BERYLLIUM_OXIDE
  name = G4_BERYLLIUM_OXIDE
  specific = 4
FEATURE [App::DocumentObjectGroupPython] Bi_element001  label="Bi_element : 4"  # scripted group (container) (typed FeaturePython)
  n = 4
  ref = Bi_element
FEATURE [App::DocumentObjectGroupPython] Ge_element001  label="Ge_element : 3"  # scripted group (container) (typed FeaturePython)
  n = 3
  ref = Ge_element
FEATURE [App::DocumentObjectGroupPython] O_element012  label="O_element : 12"  # scripted group (container) (typed FeaturePython)
  n = 12
  ref = O_element
FEATURE [App::DocumentObjectGroupPython] G4_BGO  # scripted group (container) (typed FeaturePython)
  Dunit = g/cm3
  Dvalue = 7.13
  Group = -> [Bi_element001,Ge_element001,O_element012]
  conduct = 2
  density = 1
  expand = 3
  formula = G4_BGO
  name = G4_BGO
  specific = 4
FEATURE [App::DocumentObjectGroupPython] H_element014  label="H_element : 0.102"  # scripted group (container) (typed FeaturePython)
  n = 0.102
FEATURE [App::DocumentObjectGroupPython] C_element014  label="C_element : 0.110"  # scripted group (container) (typed FeaturePython)
  n = 0.11
FEATURE [App::DocumentObjectGroupPython] N_element009  label="N_element : 0.033"  # scripted group (container) (typed FeaturePython)
  n = 0.033
FEATURE [App::DocumentObjectGroupPython] O_element013  label="O_element : 0.745"  # scripted group (container) (typed FeaturePython)
  n = 0.745
FEATURE [App::DocumentObjectGroupPython] Na_element002  label="Na_element : 0.002"  # scripted group (container) (typed FeaturePython)
  n = 0.001
FEATURE [App::DocumentObjectGroupPython] P_element001  label="P_element : 0.001"  # scripted group (container) (typed FeaturePython)
  n = 0.001
FEATURE [App::DocumentObjectGroupPython] S_element003  label="S_element : 0.002"  # scripted group (container) (typed FeaturePython)
  n = 0.002
FEATURE [App::DocumentObjectGroupPython] Cl_element002  label="Cl_element : 0.003"  # scripted group (container) (typed FeaturePython)
  n = 0.003
FEATURE [App::DocumentObjectGroupPython] K_element001  label="K_element : 0.002"  # scripted group (container) (typed FeaturePython)
  n = 0.002
FEATURE [App::DocumentObjectGroupPython] Fe_element001  label="Fe_element : 0.001"  # scripted group (container) (typed FeaturePython)
  n = 0.001
FEATURE [App::DocumentObjectGroupPython] G4_BLOOD_ICRP  # scripted group (container) (typed FeaturePython)
  Dunit = g/cm3
  Dvalue = 1.06
  Group = -> [H_element014,C_element014,N_element009,O_element013,Na_element002,P_element001,S_element003,Cl_element002,K_element001,Fe_element001]
  conduct = 2
  density = 1
  expand = 3
  formula = G4_BLOOD_ICRP
  name = G4_BLOOD_ICRP
  specific = 4
FEATURE [App::DocumentObjectGroupPython] H_element015  label="H_element : 0.064"  # scripted group (container) (typed FeaturePython)
  n = 0.064
FEATURE [App::DocumentObjectGroupPython] C_element015  label="C_element : 0.278"  # scripted group (container) (typed FeaturePython)
  n = 0.278
FEATURE [App::DocumentObjectGroupPython] N_element010  label="N_element : 0.027"  # scripted group (container) (typed FeaturePython)
  n = 0.027
FEATURE [App::DocumentObjectGroupPython] O_element014  label="O_element : 0.410"  # scripted group (container) (typed FeaturePython)
  n = 0.41
FEATURE [App::DocumentObjectGroupPython] Mg_element001  label="Mg_element : 0.002"  # scripted group (container) (typed FeaturePython)
  n = 0.002
FEATURE [App::DocumentObjectGroupPython] P_element002  label="P_element : 0.070"  # scripted group (container) (typed FeaturePython)
  n = 0.07
FEATURE [App::DocumentObjectGroupPython] S_element004  label="S_element : 0.003"  # scripted group (container) (typed FeaturePython)
  n = 0.002
FEATURE [App::DocumentObjectGroupPython] Ca_element003  label="Ca_element : 0.147"  # scripted group (container) (typed FeaturePython)
  n = 0.147
FEATURE [App::DocumentObjectGroupPython] G4_BONE_COMPACT_ICRU  # scripted group (container) (typed FeaturePython)
  Dunit = g/cm3
  Dvalue = 1.85
  Group = -> [H_element015,C_element015,N_element010,O_element014,Mg_element001,P_element002,S_element004,Ca_element003]
  conduct = 2
  density = 1
  expand = 3
  formula = G4_BONE_COMPACT_ICRU
  name = G4_BONE_COMPACT_ICRU
  specific = 4
FEATURE [App::DocumentObjectGroupPython] H_element016  label="H_element : 0.034"  # scripted group (container) (typed FeaturePython)
  n = 0.034
FEATURE [App::DocumentObjectGroupPython] C_element016  label="C_element : 0.155"  # scripted group (container) (typed FeaturePython)
  n = 0.155
FEATURE [App::DocumentObjectGroupPython] N_element011  label="N_element : 0.042"  # scripted group (container) (typed FeaturePython)
  n = 0.042
FEATURE [App::DocumentObjectGroupPython] O_element015  label="O_element : 0.435"  # scripted group (container) (typed FeaturePython)
  n = 0.435
FEATURE [App::DocumentObjectGroupPython] Na_element003  label="Na_element : 0.003"  # scripted group (container) (typed FeaturePython)
  n = 0.001
FEATURE [App::DocumentObjectGroupPython] Mg_element002  label="Mg_element : 0.003"  # scripted group (container) (typed FeaturePython)
  n = 0.002
FEATURE [App::DocumentObjectGroupPython] P_element003  label="P_element : 0.103"  # scripted group (container) (typed FeaturePython)
  n = 0.103
FEATURE [App::DocumentObjectGroupPython] S_element005  label="S_element : 0.004"  # scripted group (container) (typed FeaturePython)
  n = 0.003
FEATURE [App::DocumentObjectGroupPython] Ca_element004  label="Ca_element : 0.225"  # scripted group (container) (typed FeaturePython)
  n = 0.225
FEATURE [App::DocumentObjectGroupPython] G4_BONE_CORTICAL_ICRP  # scripted group (container) (typed FeaturePython)
  Dunit = g/cm3
  Dvalue = 1.92
  Group = -> [H_element016,C_element016,N_element011,O_element015,Na_element003,Mg_element002,P_element003,S_element005,Ca_element004]
  conduct = 2
  density = 1
  expand = 3
  formula = G4_BONE_CORTICAL_ICRP
  name = G4_BONE_CORTICAL_ICRP
  specific = 4
FEATURE [App::DocumentObjectGroupPython] B_element001  label="B_element : 4"  # scripted group (container) (typed FeaturePython)
  n = 4
  ref = B_element
FEATURE [App::DocumentObjectGroupPython] C_element017  label="C_element : 1"  # scripted group (container) (typed FeaturePython)
  n = 1
  ref = C_element
FEATURE [App::DocumentObjectGroupPython] G4_BORON_CARBIDE  # scripted group (container) (typed FeaturePython)
  Dunit = g/cm3
  Dvalue = 2.52
  Group = -> [B_element001,C_element017]
  conduct = 2
  density = 1
  expand = 3
  formula = G4_BORON_CARBIDE
  name = G4_BORON_CARBIDE
  specific = 4
FEATURE [App::DocumentObjectGroupPython] B_element002  label="B_element : 2"  # scripted group (container) (typed FeaturePython)
  n = 2
  ref = B_element
FEATURE [App::DocumentObjectGroupPython] O_element016  label="O_element : 006"  # scripted group (container) (typed FeaturePython)
  n = 3
  ref = O_element
FEATURE [App::DocumentObjectGroupPython] G4_BORON_OXIDE  # scripted group (container) (typed FeaturePython)
  Dunit = g/cm3
  Dvalue = 1.812
  Group = -> [B_element002,O_element016]
  conduct = 2
  density = 1
  expand = 3
  formula = G4_BORON_OXIDE
  name = G4_BORON_OXIDE
  specific = 4
FEATURE [App::DocumentObjectGroupPython] H_element017  label="H_element : 0.107"  # scripted group (container) (typed FeaturePython)
  n = 0.107
FEATURE [App::DocumentObjectGroupPython] C_element018  label="C_element : 0.145"  # scripted group (container) (typed FeaturePython)
  n = 0.145
FEATURE [App::DocumentObjectGroupPython] N_element012  label="N_element : 0.022"  # scripted group (container) (typed FeaturePython)
  n = 0.022
FEATURE [App::DocumentObjectGroupPython] O_element017  label="O_element : 0.712"  # scripted group (container) (typed FeaturePython)
  n = 0.712
FEATURE [App::DocumentObjectGroupPython] Na_element004  label="Na_element : 0.004"  # scripted group (container) (typed FeaturePython)
  n = 0.002
FEATURE [App::DocumentObjectGroupPython] P_element004  label="P_element : 0.004"  # scripted group (container) (typed FeaturePython)
  n = 0.004
FEATURE [App::DocumentObjectGroupPython] S_element006  label="S_element : 0.005"  # scripted group (container) (typed FeaturePython)
  n = 0.002
FEATURE [App::DocumentObjectGroupPython] Cl_element003  label="Cl_element : 0.004"  # scripted group (container) (typed FeaturePython)
  n = 0.003
FEATURE [App::DocumentObjectGroupPython] K_element002  label="K_element : 0.003"  # scripted group (container) (typed FeaturePython)
  n = 0.003
FEATURE [App::DocumentObjectGroupPython] G4_BRAIN_ICRP  # scripted group (container) (typed FeaturePython)
  Dunit = g/cm3
  Dvalue = 1.04
  Group = -> [H_element017,C_element018,N_element012,O_element017,Na_element004,P_element004,S_element006,Cl_element003,K_element002]
  conduct = 2
  density = 1
  expand = 3
  formula = G4_BRAIN_ICRP
  name = G4_BRAIN_ICRP
  specific = 4
FEATURE [App::DocumentObjectGroupPython] C_element019  label="C_element : 4"  # scripted group (container) (typed FeaturePython)
  n = 4
  ref = C_element
FEATURE [App::DocumentObjectGroupPython] H_element018  label="H_element : 010"  # scripted group (container) (typed FeaturePython)
  n = 10
  ref = H_element
FEATURE [App::DocumentObjectGroupPython] G4_BUTANE  # scripted group (container) (typed FeaturePython)
  Dunit = g/cm3
  Dvalue = 0.00249343
  Group = -> [C_element019,H_element018]
  conduct = 2
  density = 1
  expand = 3
  formula = G4_BUTANE
  name = G4_BUTANE
  specific = 4
FEATURE [App::DocumentObjectGroupPython] C_element020  label="C_element : 008"  # scripted group (container) (typed FeaturePython)
  n = 4
  ref = C_element
FEATURE [App::DocumentObjectGroupPython] H_element019  label="H_element : 011"  # scripted group (container) (typed FeaturePython)
  n = 10
  ref = H_element
FEATURE [App::DocumentObjectGroupPython] O_element018  label="O_element : 007"  # scripted group (container) (typed FeaturePython)
  n = 1
  ref = O_element
FEATURE [App::DocumentObjectGroupPython] G4_N_BUTYL_ALCOHOL  label="G4_N-BUTYL_ALCOHOL"  # scripted group (container) (typed FeaturePython)
  Dunit = g/cm3
  Dvalue = 0.8098
  Group = -> [C_element020,H_element019,O_element018]
  conduct = 2
  density = 1
  expand = 3
  formula = G4_N-BUTYL_ALCOHOL
  name = G4_N-BUTYL_ALCOHOL
  specific = 4
FEATURE [App::DocumentObjectGroupPython] H_element020  label="H_element : 0.025"  # scripted group (container) (typed FeaturePython)
  n = 0.02468
FEATURE [App::DocumentObjectGroupPython] C_element021  label="C_element : 0.502"  # scripted group (container) (typed FeaturePython)
  n = 0.501611
FEATURE [App::DocumentObjectGroupPython] O_element019  label="O_element : 0.005"  # scripted group (container) (typed FeaturePython)
  n = 0.004527
FEATURE [App::DocumentObjectGroupPython] F_element004  label="F_element : 0.465"  # scripted group (container) (typed FeaturePython)
  n = 0.465209
FEATURE [App::DocumentObjectGroupPython] Si_element001  label="Si_element : 0.004"  # scripted group (container) (typed FeaturePython)
  n = 0.003973
FEATURE [App::DocumentObjectGroupPython] G4_C_552  label="G4_C-552"  # scripted group (container) (typed FeaturePython)
  Dunit = g/cm3
  Dvalue = 1.76
  Group = -> [H_element020,C_element021,O_element019,F_element004,Si_element001]
  conduct = 2
  density = 1
  expand = 3
  formula = G4_C-552
  name = G4_C-552
  specific = 4
FEATURE [App::DocumentObjectGroupPython] Cd_element001  label="Cd_element : 1"  # scripted group (container) (typed FeaturePython)
  n = 1
  ref = Cd_element
FEATURE [App::DocumentObjectGroupPython] Te_element001  label="Te_element : 1"  # scripted group (container) (typed FeaturePython)
  n = 1
  ref = Te_element
FEATURE [App::DocumentObjectGroupPython] G4_CADMIUM_TELLURIDE  # scripted group (container) (typed FeaturePython)
  Dunit = g/cm3
  Dvalue = 6.2
  Group = -> [Cd_element001,Te_element001]
  conduct = 2
  density = 1
  expand = 3
  formula = G4_CADMIUM_TELLURIDE
  name = G4_CADMIUM_TELLURIDE
  specific = 4
FEATURE [App::DocumentObjectGroupPython] Cd_element002  label="Cd_element : 002"  # scripted group (container) (typed FeaturePython)
  n = 1
  ref = Cd_element
FEATURE [App::DocumentObjectGroupPython] W_element001  label="W_element : 1"  # scripted group (container) (typed FeaturePython)
  n = 1
  ref = W_element
FEATURE [App::DocumentObjectGroupPython] O_element020  label="O_element : 008"  # scripted group (container) (typed FeaturePython)
  n = 4
  ref = O_element
FEATURE [App::DocumentObjectGroupPython] G4_CADMIUM_TUNGSTATE  # scripted group (container) (typed FeaturePython)
  Dunit = g/cm3
  Dvalue = 7.9
  Group = -> [Cd_element002,W_element001,O_element020]
  conduct = 2
  density = 1
  expand = 3
  formula = G4_CADMIUM_TUNGSTATE
  name = G4_CADMIUM_TUNGSTATE
  specific = 4
FEATURE [App::DocumentObjectGroupPython] Ca_element005  label="Ca_element : 1"  # scripted group (container) (typed FeaturePython)
  n = 1
  ref = Ca_element
FEATURE [App::DocumentObjectGroupPython] C_element022  label="C_element : 009"  # scripted group (container) (typed FeaturePython)
  n = 1
  ref = C_element
FEATURE [App::DocumentObjectGroupPython] O_element021  label="O_element : 009"  # scripted group (container) (typed FeaturePython)
  n = 3
  ref = O_element
FEATURE [App::DocumentObjectGroupPython] G4_CALCIUM_CARBONATE  # scripted group (container) (typed FeaturePython)
  Dunit = g/cm3
  Dvalue = 2.8
  Group = -> [Ca_element005,C_element022,O_element021]
  conduct = 2
  density = 1
  expand = 3
  formula = G4_CALCIUM_CARBONATE
  name = G4_CALCIUM_CARBONATE
  specific = 4
FEATURE [App::DocumentObjectGroupPython] Ca_element006  label="Ca_element : 002"  # scripted group (container) (typed FeaturePython)
  n = 1
  ref = Ca_element
FEATURE [App::DocumentObjectGroupPython] F_element005  label="F_element : 003"  # scripted group (container) (typed FeaturePython)
  n = 2
  ref = F_element
FEATURE [App::DocumentObjectGroupPython] G4_CALCIUM_FLUORIDE  # scripted group (container) (typed FeaturePython)
  Dunit = g/cm3
  Dvalue = 3.18
  Group = -> [Ca_element006,F_element005]
  conduct = 2
  density = 1
  expand = 3
  formula = G4_CALCIUM_FLUORIDE
  name = G4_CALCIUM_FLUORIDE
  specific = 4
FEATURE [App::DocumentObjectGroupPython] Ca_element007  label="Ca_element : 003"  # scripted group (container) (typed FeaturePython)
  n = 1
  ref = Ca_element
FEATURE [App::DocumentObjectGroupPython] O_element022  label="O_element : 010"  # scripted group (container) (typed FeaturePython)
  n = 1
  ref = O_element
FEATURE [App::DocumentObjectGroupPython] G4_CALCIUM_OXIDE  # scripted group (container) (typed FeaturePython)
  Dunit = g/cm3
  Dvalue = 3.3
  Group = -> [Ca_element007,O_element022]
  conduct = 2
  density = 1
  expand = 3
  formula = G4_CALCIUM_OXIDE
  name = G4_CALCIUM_OXIDE
  specific = 4
FEATURE [App::DocumentObjectGroupPython] Ca_element008  label="Ca_element : 004"  # scripted group (container) (typed FeaturePython)
  n = 1
  ref = Ca_element
FEATURE [App::DocumentObjectGroupPython] S_element007  label="S_element : 002"  # scripted group (container) (typed FeaturePython)
  n = 1
  ref = S_element
FEATURE [App::DocumentObjectGroupPython] O_element023  label="O_element : 011"  # scripted group (container) (typed FeaturePython)
  n = 4
  ref = O_element
FEATURE [App::DocumentObjectGroupPython] G4_CALCIUM_SULFATE  # scripted group (container) (typed FeaturePython)
  Dunit = g/cm3
  Dvalue = 2.96
  Group = -> [Ca_element008,S_element007,O_element023]
  conduct = 2
  density = 1
  expand = 3
  formula = G4_CALCIUM_SULFATE
  name = G4_CALCIUM_SULFATE
  specific = 4
FEATURE [App::DocumentObjectGroupPython] Ca_element009  label="Ca_element : 005"  # scripted group (container) (typed FeaturePython)
  n = 1
  ref = Ca_element
FEATURE [App::DocumentObjectGroupPython] W_element002  label="W_element : 002"  # scripted group (container) (typed FeaturePython)
  n = 1
  ref = W_element
FEATURE [App::DocumentObjectGroupPython] O_element024  label="O_element : 012"  # scripted group (container) (typed FeaturePython)
  n = 4
  ref = O_element
FEATURE [App::DocumentObjectGroupPython] G4_CALCIUM_TUNGSTATE  # scripted group (container) (typed FeaturePython)
  Dunit = g/cm3
  Dvalue = 6.062
  Group = -> [Ca_element009,W_element002,O_element024]
  conduct = 2
  density = 1
  expand = 3
  formula = G4_CALCIUM_TUNGSTATE
  name = G4_CALCIUM_TUNGSTATE
  specific = 4
FEATURE [App::DocumentObjectGroupPython] C_element023  label="C_element : 010"  # scripted group (container) (typed FeaturePython)
  n = 1
  ref = C_element
FEATURE [App::DocumentObjectGroupPython] O_element025  label="O_element : 013"  # scripted group (container) (typed FeaturePython)
  n = 2
  ref = O_element
FEATURE [App::DocumentObjectGroupPython] G4_CARBON_DIOXIDE  # scripted group (container) (typed FeaturePython)
  Dunit = g/cm3
  Dvalue = 0.00184212
  Group = -> [C_element023,O_element025]
  conduct = 2
  density = 1
  expand = 3
  formula = G4_CARBON_DIOXIDE
  name = G4_CARBON_DIOXIDE
  specific = 4
FEATURE [App::DocumentObjectGroupPython] C_element024  label="C_element : 011"  # scripted group (container) (typed FeaturePython)
  n = 1
  ref = C_element
FEATURE [App::DocumentObjectGroupPython] Cl_element004  label="Cl_element : 4"  # scripted group (container) (typed FeaturePython)
  n = 4
  ref = Cl_element
FEATURE [App::DocumentObjectGroupPython] G4_CARBON_TETRACHLORIDE  # scripted group (container) (typed FeaturePython)
  Dunit = g/cm3
  Dvalue = 1.594
  Group = -> [C_element024,Cl_element004]
  conduct = 2
  density = 1
  expand = 3
  formula = G4_CARBON_TETRACHLORIDE
  name = G4_CARBON_TETRACHLORIDE
  specific = 4
FEATURE [App::DocumentObjectGroupPython] C_element025  label="C_element : 012"  # scripted group (container) (typed FeaturePython)
  n = 6
  ref = C_element
FEATURE [App::DocumentObjectGroupPython] H_element021  label="H_element : 012"  # scripted group (container) (typed FeaturePython)
  n = 10
  ref = H_element
FEATURE [App::DocumentObjectGroupPython] O_element026  label="O_element : 5"  # scripted group (container) (typed FeaturePython)
  n = 5
  ref = O_element
FEATURE [App::DocumentObjectGroupPython] G4_CELLULOSE_CELLOPHANE  # scripted group (container) (typed FeaturePython)
  Dunit = g/cm3
  Dvalue = 1.42
  Group = -> [C_element025,H_element021,O_element026]
  conduct = 2
  density = 1
  expand = 3
  formula = G4_CELLULOSE_CELLOPHANE
  name = G4_CELLULOSE_CELLOPHANE
  specific = 4
FEATURE [App::DocumentObjectGroupPython] H_element022  label="H_element : 0.067"  # scripted group (container) (typed FeaturePython)
  n = 0.067125
FEATURE [App::DocumentObjectGroupPython] C_element026  label="C_element : 0.545"  # scripted group (container) (typed FeaturePython)
  n = 0.545403
FEATURE [App::DocumentObjectGroupPython] O_element027  label="O_element : 0.387"  # scripted group (container) (typed FeaturePython)
  n = 0.387472
FEATURE [App::DocumentObjectGroupPython] G4_CELLULOSE_BUTYRATE  # scripted group (container) (typed FeaturePython)
  Dunit = g/cm3
  Dvalue = 1.2
  Group = -> [H_element022,C_element026,O_element027]
  conduct = 2
  density = 1
  expand = 3
  formula = G4_CELLULOSE_BUTYRATE
  name = G4_CELLULOSE_BUTYRATE
  specific = 4
FEATURE [App::DocumentObjectGroupPython] H_element023  label="H_element : 0.029"  # scripted group (container) (typed FeaturePython)
  n = 0.029216
FEATURE [App::DocumentObjectGroupPython] C_element027  label="C_element : 0.271"  # scripted group (container) (typed FeaturePython)
  n = 0.271296
FEATURE [App::DocumentObjectGroupPython] N_element013  label="N_element : 0.121"  # scripted group (container) (typed FeaturePython)
  n = 0.121276
FEATURE [App::DocumentObjectGroupPython] O_element028  label="O_element : 0.578"  # scripted group (container) (typed FeaturePython)
  n = 0.578212
FEATURE [App::DocumentObjectGroupPython] G4_CELLULOSE_NITRATE  # scripted group (container) (typed FeaturePython)
  Dunit = g/cm3
  Dvalue = 1.49
  Group = -> [H_element023,C_element027,N_element013,O_element028]
  conduct = 2
  density = 1
  expand = 3
  formula = G4_CELLULOSE_NITRATE
  name = G4_CELLULOSE_NITRATE
  specific = 4
FEATURE [App::DocumentObjectGroupPython] H_element024  label="H_element : 0.108"  # scripted group (container) (typed FeaturePython)
  n = 0.107596
FEATURE [App::DocumentObjectGroupPython] N_element014  label="N_element : 0.001"  # scripted group (container) (typed FeaturePython)
  n = 0.0008
FEATURE [App::DocumentObjectGroupPython] O_element029  label="O_element : 0.875"  # scripted group (container) (typed FeaturePython)
  n = 0.874976
FEATURE [App::DocumentObjectGroupPython] S_element008  label="S_element : 0.015"  # scripted group (container) (typed FeaturePython)
  n = 0.014627
FEATURE [App::DocumentObjectGroupPython] Ce_element001  label="Ce_element : 0.002"  # scripted group (container) (typed FeaturePython)
  n = 0.002001
FEATURE [App::DocumentObjectGroupPython] G4_CERIC_SULFATE  # scripted group (container) (typed FeaturePython)
  Dunit = g/cm3
  Dvalue = 1.03
  Group = -> [H_element024,N_element014,O_element029,S_element008,Ce_element001]
  conduct = 2
  density = 1
  expand = 3
  formula = G4_CERIC_SULFATE
  name = G4_CERIC_SULFATE
  specific = 4
FEATURE [App::DocumentObjectGroupPython] Cs_element001  label="Cs_element : 1"  # scripted group (container) (typed FeaturePython)
  n = 1
  ref = Cs_element
FEATURE [App::DocumentObjectGroupPython] F_element006  label="F_element : 1"  # scripted group (container) (typed FeaturePython)
  n = 1
  ref = F_element
FEATURE [App::DocumentObjectGroupPython] G4_CESIUM_FLUORIDE  # scripted group (container) (typed FeaturePython)
  Dunit = g/cm3
  Dvalue = 4.115
  Group = -> [Cs_element001,F_element006]
  conduct = 2
  density = 1
  expand = 3
  formula = G4_CESIUM_FLUORIDE
  name = G4_CESIUM_FLUORIDE
  specific = 4
FEATURE [App::DocumentObjectGroupPython] Cs_element002  label="Cs_element : 002"  # scripted group (container) (typed FeaturePython)
  n = 1
  ref = Cs_element
FEATURE [App::DocumentObjectGroupPython] I_element001  label="I_element : 1"  # scripted group (container) (typed FeaturePython)
  n = 1
  ref = I_element
FEATURE [App::DocumentObjectGroupPython] G4_CESIUM_IODIDE  # scripted group (container) (typed FeaturePython)
  Dunit = g/cm3
  Dvalue = 4.51
  Group = -> [Cs_element002,I_element001]
  conduct = 2
  density = 1
  expand = 3
  formula = G4_CESIUM_IODIDE
  name = G4_CESIUM_IODIDE
  specific = 4
FEATURE [App::DocumentObjectGroupPython] C_element028  label="C_element : 013"  # scripted group (container) (typed FeaturePython)
  n = 6
  ref = C_element
FEATURE [App::DocumentObjectGroupPython] H_element025  label="H_element : 013"  # scripted group (container) (typed FeaturePython)
  n = 5
  ref = H_element
FEATURE [App::DocumentObjectGroupPython] Cl_element005  label="Cl_element : 1"  # scripted group (container) (typed FeaturePython)
  n = 1
  ref = Cl_element
FEATURE [App::DocumentObjectGroupPython] G4_CHLOROBENZENE  # scripted group (container) (typed FeaturePython)
  Dunit = g/cm3
  Dvalue = 1.1058
  Group = -> [C_element028,H_element025,Cl_element005]
  conduct = 2
  density = 1
  expand = 3
  formula = G4_CHLOROBENZENE
  name = G4_CHLOROBENZENE
  specific = 4
FEATURE [App::DocumentObjectGroupPython] C_element029  label="C_element : 014"  # scripted group (container) (typed FeaturePython)
  n = 1
  ref = C_element
FEATURE [App::DocumentObjectGroupPython] H_element026  label="H_element : 1"  # scripted group (container) (typed FeaturePython)
  n = 1
  ref = H_element
FEATURE [App::DocumentObjectGroupPython] Cl_element006  label="Cl_element : 3"  # scripted group (container) (typed FeaturePython)
  n = 3
  ref = Cl_element
FEATURE [App::DocumentObjectGroupPython] G4_CHLOROFORM  # scripted group (container) (typed FeaturePython)
  Dunit = g/cm3
  Dvalue = 1.4832
  Group = -> [C_element029,H_element026,Cl_element006]
  conduct = 2
  density = 1
  expand = 3
  formula = G4_CHLOROFORM
  name = G4_CHLOROFORM
  specific = 4
FEATURE [App::DocumentObjectGroupPython] H_element027  label="H_element : 0.010"  # scripted group (container) (typed FeaturePython)
  n = 0.01
FEATURE [App::DocumentObjectGroupPython] C_element030  label="C_element : 0.001"  # scripted group (container) (typed FeaturePython)
  n = 0.001
FEATURE [App::DocumentObjectGroupPython] O_element030  label="O_element : 0.529"  # scripted group (container) (typed FeaturePython)
  n = 0.529107
FEATURE [App::DocumentObjectGroupPython] Na_element005  label="Na_element : 0.016"  # scripted group (container) (typed FeaturePython)
  n = 0.016
FEATURE [App::DocumentObjectGroupPython] Mg_element003  label="Mg_element : 0.004"  # scripted group (container) (typed FeaturePython)
  n = 0.002
FEATURE [App::DocumentObjectGroupPython] Al_element002  label="Al_element : 0.034"  # scripted group (container) (typed FeaturePython)
  n = 0.033872
FEATURE [App::DocumentObjectGroupPython] Si_element002  label="Si_element : 0.337"  # scripted group (container) (typed FeaturePython)
  n = 0.337021
FEATURE [App::DocumentObjectGroupPython] K_element003  label="K_element : 0.013"  # scripted group (container) (typed FeaturePython)
  n = 0.013
FEATURE [App::DocumentObjectGroupPython] Ca_element010  label="Ca_element : 0.044"  # scripted group (container) (typed FeaturePython)
  n = 0.044
FEATURE [App::DocumentObjectGroupPython] Fe_element002  label="Fe_element : 0.014"  # scripted group (container) (typed FeaturePython)
  n = 0.014
FEATURE [App::DocumentObjectGroupPython] G4_CONCRETE  # scripted group (container) (typed FeaturePython)
  Dunit = g/cm3
  Dvalue = 2.3
  Group = -> [H_element027,C_element030,O_element030,Na_element005,Mg_element003,Al_element002,Si_element002,K_element003,Ca_element010,Fe_element002]
  conduct = 2
  density = 1
  expand = 3
  formula = G4_CONCRETE
  name = G4_CONCRETE
  specific = 4
FEATURE [App::DocumentObjectGroupPython] C_element031  label="C_element : 015"  # scripted group (container) (typed FeaturePython)
  n = 6
  ref = C_element
FEATURE [App::DocumentObjectGroupPython] H_element028  label="H_element : 12"  # scripted group (container) (typed FeaturePython)
  n = 12
  ref = H_element
FEATURE [App::DocumentObjectGroupPython] G4_CYCLOHEXANE  # scripted group (container) (typed FeaturePython)
  Dunit = g/cm3
  Dvalue = 0.779
  Group = -> [C_element031,H_element028]
  conduct = 2
  density = 1
  expand = 3
  formula = G4_CYCLOHEXANE
  name = G4_CYCLOHEXANE
  specific = 4
FEATURE [App::DocumentObjectGroupPython] C_element032  label="C_element : 016"  # scripted group (container) (typed FeaturePython)
  n = 6
  ref = C_element
FEATURE [App::DocumentObjectGroupPython] H_element029  label="H_element : 4"  # scripted group (container) (typed FeaturePython)
  n = 4
  ref = H_element
FEATURE [App::DocumentObjectGroupPython] Cl_element007  label="Cl_element : 2"  # scripted group (container) (typed FeaturePython)
  n = 2
  ref = Cl_element
FEATURE [App::DocumentObjectGroupPython] G4_1_2_DICHLOROBENZENE  label="G4_1.2-DICHLOROBENZENE"  # scripted group (container) (typed FeaturePython)
  Dunit = g/cm3
  Dvalue = 1.3048
  Group = -> [C_element032,H_element029,Cl_element007]
  conduct = 2
  density = 1
  expand = 3
  formula = G4_1.2-DICHLOROBENZENE
  name = G4_1.2-DICHLOROBENZENE
  specific = 4
FEATURE [App::DocumentObjectGroupPython] C_element033  label="C_element : 017"  # scripted group (container) (typed FeaturePython)
  n = 4
  ref = C_element
FEATURE [App::DocumentObjectGroupPython] H_element030  label="H_element : 8"  # scripted group (container) (typed FeaturePython)
  n = 8
  ref = H_element
FEATURE [App::DocumentObjectGroupPython] O_element031  label="O_element : 014"  # scripted group (container) (typed FeaturePython)
  n = 1
  ref = O_element
FEATURE [App::DocumentObjectGroupPython] Cl_element008  label="Cl_element : 005"  # scripted group (container) (typed FeaturePython)
  n = 2
  ref = Cl_element
FEATURE [App::DocumentObjectGroupPython] G4_DICHLORODIETHYL_ETHER  # scripted group (container) (typed FeaturePython)
  Dunit = g/cm3
  Dvalue = 1.2199
  Group = -> [C_element033,H_element030,O_element031,Cl_element008]
  conduct = 2
  density = 1
  expand = 3
  formula = G4_DICHLORODIETHYL_ETHER
  name = G4_DICHLORODIETHYL_ETHER
  specific = 4
FEATURE [App::DocumentObjectGroupPython] C_element034  label="C_element : 018"  # scripted group (container) (typed FeaturePython)
  n = 2
  ref = C_element
FEATURE [App::DocumentObjectGroupPython] H_element031  label="H_element : 014"  # scripted group (container) (typed FeaturePython)
  n = 4
  ref = H_element
FEATURE [App::DocumentObjectGroupPython] Cl_element009  label="Cl_element : 006"  # scripted group (container) (typed FeaturePython)
  n = 2
  ref = Cl_element
FEATURE [App::DocumentObjectGroupPython] G4_1_2_DICHLOROETHANE  label="G4_1.2-DICHLOROETHANE"  # scripted group (container) (typed FeaturePython)
  Dunit = g/cm3
  Dvalue = 1.2351
  Group = -> [C_element034,H_element031,Cl_element009]
  conduct = 2
  density = 1
  expand = 3
  formula = G4_1.2-DICHLOROETHANE
  name = G4_1.2-DICHLOROETHANE
  specific = 4
FEATURE [App::DocumentObjectGroupPython] C_element035  label="C_element : 019"  # scripted group (container) (typed FeaturePython)
  n = 4
  ref = C_element
FEATURE [App::DocumentObjectGroupPython] H_element032  label="H_element : 015"  # scripted group (container) (typed FeaturePython)
  n = 10
  ref = H_element
FEATURE [App::DocumentObjectGroupPython] O_element032  label="O_element : 015"  # scripted group (container) (typed FeaturePython)
  n = 1
  ref = O_element
FEATURE [App::DocumentObjectGroupPython] G4_DIETHYL_ETHER  # scripted group (container) (typed FeaturePython)
  Dunit = g/cm3
  Dvalue = 0.71378
  Group = -> [C_element035,H_element032,O_element032]
  conduct = 2
  density = 1
  expand = 3
  formula = G4_DIETHYL_ETHER
  name = G4_DIETHYL_ETHER
  specific = 4
FEATURE [App::DocumentObjectGroupPython] C_element036  label="C_element : 020"  # scripted group (container) (typed FeaturePython)
  n = 3
  ref = C_element
FEATURE [App::DocumentObjectGroupPython] H_element033  label="H_element : 016"  # scripted group (container) (typed FeaturePython)
  n = 7
  ref = H_element
FEATURE [App::DocumentObjectGroupPython] N_element015  label="N_element : 008"  # scripted group (container) (typed FeaturePython)
  n = 1
  ref = N_element
FEATURE [App::DocumentObjectGroupPython] O_element033  label="O_element : 016"  # scripted group (container) (typed FeaturePython)
  n = 1
  ref = O_element
FEATURE [App::DocumentObjectGroupPython] G4_N_N_DIMETHYL_FORMAMIDE  label="G4_N.N-DIMETHYL_FORMAMIDE"  # scripted group (container) (typed FeaturePython)
  Dunit = g/cm3
  Dvalue = 0.9487
  Group = -> [C_element036,H_element033,N_element015,O_element033]
  conduct = 2
  density = 1
  expand = 3
  formula = G4_N.N-DIMETHYL_FORMAMIDE
  name = G4_N.N-DIMETHYL_FORMAMIDE
  specific = 4
FEATURE [App::DocumentObjectGroupPython] C_element037  label="C_element : 021"  # scripted group (container) (typed FeaturePython)
  n = 2
  ref = C_element
FEATURE [App::DocumentObjectGroupPython] H_element034  label="H_element : 017"  # scripted group (container) (typed FeaturePython)
  n = 6
  ref = H_element
FEATURE [App::DocumentObjectGroupPython] O_element034  label="O_element : 017"  # scripted group (container) (typed FeaturePython)
  n = 1
  ref = O_element
FEATURE [App::DocumentObjectGroupPython] S_element009  label="S_element : 003"  # scripted group (container) (typed FeaturePython)
  n = 1
  ref = S_element
FEATURE [App::DocumentObjectGroupPython] G4_DIMETHYL_SULFOXIDE  # scripted group (container) (typed FeaturePython)
  Dunit = g/cm3
  Dvalue = 1.1014
  Group = -> [C_element037,H_element034,O_element034,S_element009]
  conduct = 2
  density = 1
  expand = 3
  formula = G4_DIMETHYL_SULFOXIDE
  name = G4_DIMETHYL_SULFOXIDE
  specific = 4
FEATURE [App::DocumentObjectGroupPython] C_element038  label="C_element : 022"  # scripted group (container) (typed FeaturePython)
  n = 2
  ref = C_element
FEATURE [App::DocumentObjectGroupPython] H_element035  label="H_element : 018"  # scripted group (container) (typed FeaturePython)
  n = 6
  ref = H_element
FEATURE [App::DocumentObjectGroupPython] G4_ETHANE  # scripted group (container) (typed FeaturePython)
  Dunit = g/cm3
  Dvalue = 0.00125324
  Group = -> [C_element038,H_element035]
  conduct = 2
  density = 1
  expand = 3
  formula = G4_ETHANE
  name = G4_ETHANE
  specific = 4
FEATURE [App::DocumentObjectGroupPython] C_element039  label="C_element : 023"  # scripted group (container) (typed FeaturePython)
  n = 2
  ref = C_element
FEATURE [App::DocumentObjectGroupPython] H_element036  label="H_element : 019"  # scripted group (container) (typed FeaturePython)
  n = 6
  ref = H_element
FEATURE [App::DocumentObjectGroupPython] O_element035  label="O_element : 018"  # scripted group (container) (typed FeaturePython)
  n = 1
  ref = O_element
FEATURE [App::DocumentObjectGroupPython] G4_ETHYL_ALCOHOL  # scripted group (container) (typed FeaturePython)
  Dunit = g/cm3
  Dvalue = 0.7893
  Group = -> [C_element039,H_element036,O_element035]
  conduct = 2
  density = 1
  expand = 3
  formula = G4_ETHYL_ALCOHOL
  name = G4_ETHYL_ALCOHOL
  specific = 4
FEATURE [App::DocumentObjectGroupPython] H_element037  label="H_element : 0.090"  # scripted group (container) (typed FeaturePython)
  n = 0.090027
FEATURE [App::DocumentObjectGroupPython] C_element040  label="C_element : 0.585"  # scripted group (container) (typed FeaturePython)
  n = 0.585182
FEATURE [App::DocumentObjectGroupPython] O_element036  label="O_element : 0.325"  # scripted group (container) (typed FeaturePython)
  n = 0.324791
FEATURE [App::DocumentObjectGroupPython] G4_ETHYL_CELLULOSE  # scripted group (container) (typed FeaturePython)
  Dunit = g/cm3
  Dvalue = 1.13
  Group = -> [H_element037,C_element040,O_element036]
  conduct = 2
  density = 1
  expand = 3
  formula = G4_ETHYL_CELLULOSE
  name = G4_ETHYL_CELLULOSE
  specific = 4
FEATURE [App::DocumentObjectGroupPython] C_element041  label="C_element : 024"  # scripted group (container) (typed FeaturePython)
  n = 2
  ref = C_element
FEATURE [App::DocumentObjectGroupPython] H_element038  label="H_element : 020"  # scripted group (container) (typed FeaturePython)
  n = 4
  ref = H_element
FEATURE [App::DocumentObjectGroupPython] G4_ETHYLENE  # scripted group (container) (typed FeaturePython)
  Dunit = g/cm3
  Dvalue = 0.00117497
  Group = -> [C_element041,H_element038]
  conduct = 2
  density = 1
  expand = 3
  formula = G4_ETHYLENE
  name = G4_ETHYLENE
  specific = 4
FEATURE [App::DocumentObjectGroupPython] H_element039  label="H_element : 0.096"  # scripted group (container) (typed FeaturePython)
  n = 0.096
FEATURE [App::DocumentObjectGroupPython] C_element042  label="C_element : 0.195"  # scripted group (container) (typed FeaturePython)
  n = 0.195
FEATURE [App::DocumentObjectGroupPython] N_element016  label="N_element : 0.057"  # scripted group (container) (typed FeaturePython)
  n = 0.057
FEATURE [App::DocumentObjectGroupPython] O_element037  label="O_element : 0.646"  # scripted group (container) (typed FeaturePython)
  n = 0.646
FEATURE [App::DocumentObjectGroupPython] Na_element006  label="Na_element : 0.017"  # scripted group (container) (typed FeaturePython)
  n = 0.001
FEATURE [App::DocumentObjectGroupPython] P_element005  label="P_element : 0.104"  # scripted group (container) (typed FeaturePython)
  n = 0.001
FEATURE [App::DocumentObjectGroupPython] S_element010  label="S_element : 0.016"  # scripted group (container) (typed FeaturePython)
  n = 0.003
FEATURE [App::DocumentObjectGroupPython] Cl_element010  label="Cl_element : 0.005"  # scripted group (container) (typed FeaturePython)
  n = 0.001
FEATURE [App::DocumentObjectGroupPython] G4_EYE_LENS_ICRP  # scripted group (container) (typed FeaturePython)
  Dunit = g/cm3
  Dvalue = 1.07
  Group = -> [H_element039,C_element042,N_element016,O_element037,Na_element006,P_element005,S_element010,Cl_element010]
  conduct = 2
  density = 1
  expand = 3
  formula = G4_EYE_LENS_ICRP
  name = G4_EYE_LENS_ICRP
  specific = 4
FEATURE [App::DocumentObjectGroupPython] Fe_element003  label="Fe_element : 2"  # scripted group (container) (typed FeaturePython)
  n = 2
  ref = Fe_element
FEATURE [App::DocumentObjectGroupPython] O_element038  label="O_element : 019"  # scripted group (container) (typed FeaturePython)
  n = 3
  ref = O_element
FEATURE [App::DocumentObjectGroupPython] G4_FERRIC_OXIDE  # scripted group (container) (typed FeaturePython)
  Dunit = g/cm3
  Dvalue = 5.2
  Group = -> [Fe_element003,O_element038]
  conduct = 2
  density = 1
  expand = 3
  formula = G4_FERRIC_OXIDE
  name = G4_FERRIC_OXIDE
  specific = 4
FEATURE [App::DocumentObjectGroupPython] Fe_element004  label="Fe_element : 1"  # scripted group (container) (typed FeaturePython)
  n = 1
  ref = Fe_element
FEATURE [App::DocumentObjectGroupPython] B_element003  label="B_element : 1"  # scripted group (container) (typed FeaturePython)
  n = 1
  ref = B_element
FEATURE [App::DocumentObjectGroupPython] G4_FERROBORIDE  # scripted group (container) (typed FeaturePython)
  Dunit = g/cm3
  Dvalue = 7.15
  Group = -> [Fe_element004,B_element003]
  conduct = 2
  density = 1
  expand = 3
  formula = G4_FERROBORIDE
  name = G4_FERROBORIDE
  specific = 4
FEATURE [App::DocumentObjectGroupPython] Fe_element005  label="Fe_element : 003"  # scripted group (container) (typed FeaturePython)
  n = 1
  ref = Fe_element
FEATURE [App::DocumentObjectGroupPython] O_element039  label="O_element : 020"  # scripted group (container) (typed FeaturePython)
  n = 1
  ref = O_element
FEATURE [App::DocumentObjectGroupPython] G4_FERROUS_OXIDE  # scripted group (container) (typed FeaturePython)
  Dunit = g/cm3
  Dvalue = 5.7
  Group = -> [Fe_element005,O_element039]
  conduct = 2
  density = 1
  expand = 3
  formula = G4_FERROUS_OXIDE
  name = G4_FERROUS_OXIDE
  specific = 4
FEATURE [App::DocumentObjectGroupPython] H_element040  label="H_element : 0.115"  # scripted group (container) (typed FeaturePython)
  n = 0.108259
FEATURE [App::DocumentObjectGroupPython] N_element017  label="N_element : 0.000"  # scripted group (container) (typed FeaturePython)
  n = 2.7e-05
FEATURE [App::DocumentObjectGroupPython] O_element040  label="O_element : 0.879"  # scripted group (container) (typed FeaturePython)
  n = 0.878636
FEATURE [App::DocumentObjectGroupPython] Na_element007  label="Na_element : 0.000"  # scripted group (container) (typed FeaturePython)
  n = 2.2e-05
FEATURE [App::DocumentObjectGroupPython] S_element011  label="S_element : 0.013"  # scripted group (container) (typed FeaturePython)
  n = 0.012968
FEATURE [App::DocumentObjectGroupPython] Cl_element011  label="Cl_element : 0.000"  # scripted group (container) (typed FeaturePython)
  n = 3.4e-05
FEATURE [App::DocumentObjectGroupPython] Fe_element006  label="Fe_element : 0.000"  # scripted group (container) (typed FeaturePython)
  n = 5.4e-05
FEATURE [App::DocumentObjectGroupPython] G4_FERROUS_SULFATE  # scripted group (container) (typed FeaturePython)
  Dunit = g/cm3
  Dvalue = 1.024
  Group = -> [H_element040,N_element017,O_element040,Na_element007,S_element011,Cl_element011,Fe_element006]
  conduct = 2
  density = 1
  expand = 3
  formula = G4_FERROUS_SULFATE
  name = G4_FERROUS_SULFATE
  specific = 4
FEATURE [App::DocumentObjectGroupPython] C_element043  label="C_element : 0.099"  # scripted group (container) (typed FeaturePython)
  n = 0.099335
FEATURE [App::DocumentObjectGroupPython] F_element007  label="F_element : 0.314"  # scripted group (container) (typed FeaturePython)
  n = 0.314247
FEATURE [App::DocumentObjectGroupPython] Cl_element012  label="Cl_element : 0.586"  # scripted group (container) (typed FeaturePython)
  n = 0.586418
FEATURE [App::DocumentObjectGroupPython] G4_FREON_12  label="G4_FREON-12"  # scripted group (container) (typed FeaturePython)
  Dunit = g/cm3
  Dvalue = 1.12
  Group = -> [C_element043,F_element007,Cl_element012]
  conduct = 2
  density = 1
  expand = 3
  formula = G4_FREON-12
  name = G4_FREON-12
  specific = 4
FEATURE [App::DocumentObjectGroupPython] C_element044  label="C_element : 0.057"  # scripted group (container) (typed FeaturePython)
  n = 0.057245
FEATURE [App::DocumentObjectGroupPython] F_element008  label="F_element : 0.181"  # scripted group (container) (typed FeaturePython)
  n = 0.181096
FEATURE [App::DocumentObjectGroupPython] Br_element001  label="Br_element : 0.762"  # scripted group (container) (typed FeaturePython)
  n = 0.761659
FEATURE [App::DocumentObjectGroupPython] G4_FREON_12B2  label="G4_FREON-12B2"  # scripted group (container) (typed FeaturePython)
  Dunit = g/cm3
  Dvalue = 1.8
  Group = -> [C_element044,F_element008,Br_element001]
  conduct = 2
  density = 1
  expand = 3
  formula = G4_FREON-12B2
  name = G4_FREON-12B2
  specific = 4
FEATURE [App::DocumentObjectGroupPython] C_element045  label="C_element : 0.115"  # scripted group (container) (typed FeaturePython)
  n = 0.114983
FEATURE [App::DocumentObjectGroupPython] F_element009  label="F_element : 0.546"  # scripted group (container) (typed FeaturePython)
  n = 0.545621
FEATURE [App::DocumentObjectGroupPython] Cl_element013  label="Cl_element : 0.339"  # scripted group (container) (typed FeaturePython)
  n = 0.339396
FEATURE [App::DocumentObjectGroupPython] G4_FREON_13  label="G4_FREON-13"  # scripted group (container) (typed FeaturePython)
  Dunit = g/cm3
  Dvalue = 0.95
  Group = -> [C_element045,F_element009,Cl_element013]
  conduct = 2
  density = 1
  expand = 3
  formula = G4_FREON-13
  name = G4_FREON-13
  specific = 4
FEATURE [App::DocumentObjectGroupPython] C_element046  label="C_element : 025"  # scripted group (container) (typed FeaturePython)
  n = 1
  ref = C_element
FEATURE [App::DocumentObjectGroupPython] F_element010  label="F_element : 3"  # scripted group (container) (typed FeaturePython)
  n = 3
  ref = F_element
FEATURE [App::DocumentObjectGroupPython] Br_element002  label="Br_element : 1"  # scripted group (container) (typed FeaturePython)
  n = 1
  ref = Br_element
FEATURE [App::DocumentObjectGroupPython] G4_FREON_13B1  label="G4_FREON-13B1"  # scripted group (container) (typed FeaturePython)
  Dunit = g/cm3
  Dvalue = 1.5
  Group = -> [C_element046,F_element010,Br_element002]
  conduct = 2
  density = 1
  expand = 3
  formula = G4_FREON-13B1
  name = G4_FREON-13B1
  specific = 4
FEATURE [App::DocumentObjectGroupPython] C_element047  label="C_element : 0.061"  # scripted group (container) (typed FeaturePython)
  n = 0.061309
FEATURE [App::DocumentObjectGroupPython] F_element011  label="F_element : 0.291"  # scripted group (container) (typed FeaturePython)
  n = 0.290924
FEATURE [App::DocumentObjectGroupPython] I_element002  label="I_element : 0.648"  # scripted group (container) (typed FeaturePython)
  n = 0.647767
FEATURE [App::DocumentObjectGroupPython] G4_FREON_13I1  label="G4_FREON-13I1"  # scripted group (container) (typed FeaturePython)
  Dunit = g/cm3
  Dvalue = 1.8
  Group = -> [C_element047,F_element011,I_element002]
  conduct = 2
  density = 1
  expand = 3
  formula = G4_FREON-13I1
  name = G4_FREON-13I1
  specific = 4
FEATURE [App::DocumentObjectGroupPython] Gd_element001  label="Gd_element : 2"  # scripted group (container) (typed FeaturePython)
  n = 2
  ref = Gd_element
FEATURE [App::DocumentObjectGroupPython] O_element041  label="O_element : 021"  # scripted group (container) (typed FeaturePython)
  n = 2
  ref = O_element
FEATURE [App::DocumentObjectGroupPython] S_element012  label="S_element : 004"  # scripted group (container) (typed FeaturePython)
  n = 1
  ref = S_element
FEATURE [App::DocumentObjectGroupPython] G4_GADOLINIUM_OXYSULFIDE  # scripted group (container) (typed FeaturePython)
  Dunit = g/cm3
  Dvalue = 7.44
  Group = -> [Gd_element001,O_element041,S_element012]
  conduct = 2
  density = 1
  expand = 3
  formula = G4_GADOLINIUM_OXYSULFIDE
  name = G4_GADOLINIUM_OXYSULFIDE
  specific = 4
FEATURE [App::DocumentObjectGroupPython] Ga_element001  label="Ga_element : 1"  # scripted group (container) (typed FeaturePython)
  n = 1
  ref = Ga_element
FEATURE [App::DocumentObjectGroupPython] As_element001  label="As_element : 1"  # scripted group (container) (typed FeaturePython)
  n = 1
  ref = As_element
FEATURE [App::DocumentObjectGroupPython] G4_GALLIUM_ARSENIDE  # scripted group (container) (typed FeaturePython)
  Dunit = g/cm3
  Dvalue = 5.31
  Group = -> [Ga_element001,As_element001]
  conduct = 2
  density = 1
  expand = 3
  formula = G4_GALLIUM_ARSENIDE
  name = G4_GALLIUM_ARSENIDE
  specific = 4
FEATURE [App::DocumentObjectGroupPython] H_element041  label="H_element : 0.081"  # scripted group (container) (typed FeaturePython)
  n = 0.08118
FEATURE [App::DocumentObjectGroupPython] C_element048  label="C_element : 0.416"  # scripted group (container) (typed FeaturePython)
  n = 0.41606
FEATURE [App::DocumentObjectGroupPython] N_element018  label="N_element : 0.111"  # scripted group (container) (typed FeaturePython)
  n = 0.11124
FEATURE [App::DocumentObjectGroupPython] O_element042  label="O_element : 0.381"  # scripted group (container) (typed FeaturePython)
  n = 0.38064
FEATURE [App::DocumentObjectGroupPython] S_element013  label="S_element : 0.011"  # scripted group (container) (typed FeaturePython)
  n = 0.01088
FEATURE [App::DocumentObjectGroupPython] G4_GEL_PHOTO_EMULSION  # scripted group (container) (typed FeaturePython)
  Dunit = g/cm3
  Dvalue = 1.2914
  Group = -> [H_element041,C_element048,N_element018,O_element042,S_element013]
  conduct = 2
  density = 1
  expand = 3
  formula = G4_GEL_PHOTO_EMULSION
  name = G4_GEL_PHOTO_EMULSION
  specific = 4
FEATURE [App::DocumentObjectGroupPython] B_element004  label="B_element : 0.040"  # scripted group (container) (typed FeaturePython)
  n = 0.0400639
FEATURE [App::DocumentObjectGroupPython] O_element043  label="O_element : 0.540"  # scripted group (container) (typed FeaturePython)
  n = 0.539561
FEATURE [App::DocumentObjectGroupPython] Na_element008  label="Na_element : 0.028"  # scripted group (container) (typed FeaturePython)
  n = 0.0281909
FEATURE [App::DocumentObjectGroupPython] Al_element003  label="Al_element : 0.012"  # scripted group (container) (typed FeaturePython)
  n = 0.011644
FEATURE [App::DocumentObjectGroupPython] Si_element003  label="Si_element : 0.377"  # scripted group (container) (typed FeaturePython)
  n = 0.377219
FEATURE [App::DocumentObjectGroupPython] K_element004  label="K_element : 0.014"  # scripted group (container) (typed FeaturePython)
  n = 0.00332099
FEATURE [App::DocumentObjectGroupPython] G4_Pyrex_Glass  # scripted group (container) (typed FeaturePython)
  Dunit = g/cm3
  Dvalue = 2.23
  Group = -> [B_element004,O_element043,Na_element008,Al_element003,Si_element003,K_element004]
  conduct = 2
  density = 1
  expand = 3
  formula = G4_Pyrex_Glass
  name = G4_Pyrex_Glass
  specific = 4
FEATURE [App::DocumentObjectGroupPython] O_element044  label="O_element : 0.156"  # scripted group (container) (typed FeaturePython)
  n = 0.156453
FEATURE [App::DocumentObjectGroupPython] Si_element004  label="Si_element : 0.081"  # scripted group (container) (typed FeaturePython)
  n = 0.080866
FEATURE [App::DocumentObjectGroupPython] Ti_element001  label="Ti_element : 0.008"  # scripted group (container) (typed FeaturePython)
  n = 0.008092
FEATURE [App::DocumentObjectGroupPython] As_element002  label="As_element : 0.003"  # scripted group (container) (typed FeaturePython)
  n = 0.002651
FEATURE [App::DocumentObjectGroupPython] Pb_element001  label="Pb_element : 0.752"  # scripted group (container) (typed FeaturePython)
  n = 0.751938
FEATURE [App::DocumentObjectGroupPython] G4_GLASS_LEAD  # scripted group (container) (typed FeaturePython)
  Dunit = g/cm3
  Dvalue = 6.22
  Group = -> [O_element044,Si_element004,Ti_element001,As_element002,Pb_element001]
  conduct = 2
  density = 1
  expand = 3
  formula = G4_GLASS_LEAD
  name = G4_GLASS_LEAD
  specific = 4
FEATURE [App::DocumentObjectGroupPython] O_element045  label="O_element : 0.460"  # scripted group (container) (typed FeaturePython)
  n = 0.4598
FEATURE [App::DocumentObjectGroupPython] Na_element009  label="Na_element : 0.096"  # scripted group (container) (typed FeaturePython)
  n = 0.0964411
FEATURE [App::DocumentObjectGroupPython] Si_element005  label="Si_element : 0.378"  # scripted group (container) (typed FeaturePython)
  n = 0.336553
FEATURE [App::DocumentObjectGroupPython] Ca_element011  label="Ca_element : 0.107"  # scripted group (container) (typed FeaturePython)
  n = 0.107205
FEATURE [App::DocumentObjectGroupPython] G4_GLASS_PLATE  # scripted group (container) (typed FeaturePython)
  Dunit = g/cm3
  Dvalue = 2.4
  Group = -> [O_element045,Na_element009,Si_element005,Ca_element011]
  conduct = 2
  density = 1
  expand = 3
  formula = G4_GLASS_PLATE
  name = G4_GLASS_PLATE
  specific = 4
FEATURE [App::DocumentObjectGroupPython] C_element049  label="C_element : 026"  # scripted group (container) (typed FeaturePython)
  n = 5
  ref = C_element
FEATURE [App::DocumentObjectGroupPython] H_element042  label="H_element : 021"  # scripted group (container) (typed FeaturePython)
  n = 10
  ref = H_element
FEATURE [App::DocumentObjectGroupPython] N_element019  label="N_element : 2"  # scripted group (container) (typed FeaturePython)
  n = 2
  ref = N_element
FEATURE [App::DocumentObjectGroupPython] O_element046  label="O_element : 022"  # scripted group (container) (typed FeaturePython)
  n = 3
  ref = O_element
FEATURE [App::DocumentObjectGroupPython] G4_GLUTAMINE  # scripted group (container) (typed FeaturePython)
  Dunit = g/cm3
  Dvalue = 1.46
  Group = -> [C_element049,H_element042,N_element019,O_element046]
  conduct = 2
  density = 1
  expand = 3
  formula = G4_GLUTAMINE
  name = G4_GLUTAMINE
  specific = 4
FEATURE [App::DocumentObjectGroupPython] C_element050  label="C_element : 027"  # scripted group (container) (typed FeaturePython)
  n = 3
  ref = C_element
FEATURE [App::DocumentObjectGroupPython] H_element043  label="H_element : 022"  # scripted group (container) (typed FeaturePython)
  n = 8
  ref = H_element
FEATURE [App::DocumentObjectGroupPython] O_element047  label="O_element : 023"  # scripted group (container) (typed FeaturePython)
  n = 3
  ref = O_element
FEATURE [App::DocumentObjectGroupPython] G4_GLYCEROL  # scripted group (container) (typed FeaturePython)
  Dunit = g/cm3
  Dvalue = 1.2613
  Group = -> [C_element050,H_element043,O_element047]
  conduct = 2
  density = 1
  expand = 3
  formula = G4_GLYCEROL
  name = G4_GLYCEROL
  specific = 4
FEATURE [App::DocumentObjectGroupPython] C_element051  label="C_element : 028"  # scripted group (container) (typed FeaturePython)
  n = 5
  ref = C_element
FEATURE [App::DocumentObjectGroupPython] H_element044  label="H_element : 023"  # scripted group (container) (typed FeaturePython)
  n = 5
  ref = H_element
FEATURE [App::DocumentObjectGroupPython] N_element020  label="N_element : 009"  # scripted group (container) (typed FeaturePython)
  n = 5
  ref = N_element
FEATURE [App::DocumentObjectGroupPython] O_element048  label="O_element : 024"  # scripted group (container) (typed FeaturePython)
  n = 1
  ref = O_element
FEATURE [App::DocumentObjectGroupPython] G4_GUANINE  # scripted group (container) (typed FeaturePython)
  Dunit = g/cm3
  Dvalue = 2.2
  Group = -> [C_element051,H_element044,N_element020,O_element048]
  conduct = 2
  density = 1
  expand = 3
  formula = G4_GUANINE
  name = G4_GUANINE
  specific = 4
FEATURE [App::DocumentObjectGroupPython] Ca_element012  label="Ca_element : 006"  # scripted group (container) (typed FeaturePython)
  n = 1
  ref = Ca_element
FEATURE [App::DocumentObjectGroupPython] S_element014  label="S_element : 005"  # scripted group (container) (typed FeaturePython)
  n = 1
  ref = S_element
FEATURE [App::DocumentObjectGroupPython] O_element049  label="O_element : 6"  # scripted group (container) (typed FeaturePython)
  n = 6
  ref = O_element
FEATURE [App::DocumentObjectGroupPython] H_element045  label="H_element : 024"  # scripted group (container) (typed FeaturePython)
  n = 4
  ref = H_element
FEATURE [App::DocumentObjectGroupPython] G4_GYPSUM  # scripted group (container) (typed FeaturePython)
  Dunit = g/cm3
  Dvalue = 2.32
  Group = -> [Ca_element012,S_element014,O_element049,H_element045]
  conduct = 2
  density = 1
  expand = 3
  formula = G4_GYPSUM
  name = G4_GYPSUM
  specific = 4
FEATURE [App::DocumentObjectGroupPython] C_element052  label="C_element : 7"  # scripted group (container) (typed FeaturePython)
  n = 7
  ref = C_element
FEATURE [App::DocumentObjectGroupPython] H_element046  label="H_element : 16"  # scripted group (container) (typed FeaturePython)
  n = 16
  ref = H_element
FEATURE [App::DocumentObjectGroupPython] G4_N_HEPTANE  label="G4_N-HEPTANE"  # scripted group (container) (typed FeaturePython)
  Dunit = g/cm3
  Dvalue = 0.68376
  Group = -> [C_element052,H_element046]
  conduct = 2
  density = 1
  expand = 3
  formula = G4_N-HEPTANE
  name = G4_N-HEPTANE
  specific = 4
FEATURE [App::DocumentObjectGroupPython] C_element053  label="C_element : 029"  # scripted group (container) (typed FeaturePython)
  n = 6
  ref = C_element
FEATURE [App::DocumentObjectGroupPython] H_element047  label="H_element : 14"  # scripted group (container) (typed FeaturePython)
  n = 14
  ref = H_element
FEATURE [App::DocumentObjectGroupPython] G4_N_HEXANE  label="G4_N-HEXANE"  # scripted group (container) (typed FeaturePython)
  Dunit = g/cm3
  Dvalue = 0.6603
  Group = -> [C_element053,H_element047]
  conduct = 2
  density = 1
  expand = 3
  formula = G4_N-HEXANE
  name = G4_N-HEXANE
  specific = 4
FEATURE [App::DocumentObjectGroupPython] C_element054  label="C_element : 22"  # scripted group (container) (typed FeaturePython)
  n = 22
  ref = C_element
FEATURE [App::DocumentObjectGroupPython] H_element048  label="H_element : 025"  # scripted group (container) (typed FeaturePython)
  n = 10
  ref = H_element
FEATURE [App::DocumentObjectGroupPython] N_element021  label="N_element : 010"  # scripted group (container) (typed FeaturePython)
  n = 2
  ref = N_element
FEATURE [App::DocumentObjectGroupPython] O_element050  label="O_element : 025"  # scripted group (container) (typed FeaturePython)
  n = 5
  ref = O_element
FEATURE [App::DocumentObjectGroupPython] G4_KAPTON  # scripted group (container) (typed FeaturePython)
  Dunit = g/cm3
  Dvalue = 1.42
  Group = -> [C_element054,H_element048,N_element021,O_element050]
  conduct = 2
  density = 1
  expand = 3
  formula = G4_KAPTON
  name = G4_KAPTON
  specific = 4
FEATURE [App::DocumentObjectGroupPython] La_element001  label="La_element : 1"  # scripted group (container) (typed FeaturePython)
  n = 1
  ref = La_element
FEATURE [App::DocumentObjectGroupPython] Br_element003  label="Br_element : 002"  # scripted group (container) (typed FeaturePython)
  n = 1
  ref = Br_element
FEATURE [App::DocumentObjectGroupPython] O_element051  label="O_element : 026"  # scripted group (container) (typed FeaturePython)
  n = 1
  ref = O_element
FEATURE [App::DocumentObjectGroupPython] G4_LANTHANUM_OXYBROMIDE  # scripted group (container) (typed FeaturePython)
  Dunit = g/cm3
  Dvalue = 6.28
  Group = -> [La_element001,Br_element003,O_element051]
  conduct = 2
  density = 1
  expand = 3
  formula = G4_LANTHANUM_OXYBROMIDE
  name = G4_LANTHANUM_OXYBROMIDE
  specific = 4
FEATURE [App::DocumentObjectGroupPython] La_element002  label="La_element : 2"  # scripted group (container) (typed FeaturePython)
  n = 2
  ref = La_element
FEATURE [App::DocumentObjectGroupPython] O_element052  label="O_element : 027"  # scripted group (container) (typed FeaturePython)
  n = 2
  ref = O_element
FEATURE [App::DocumentObjectGroupPython] S_element015  label="S_element : 006"  # scripted group (container) (typed FeaturePython)
  n = 1
  ref = S_element
FEATURE [App::DocumentObjectGroupPython] G4_LANTHANUM_OXYSULFIDE  # scripted group (container) (typed FeaturePython)
  Dunit = g/cm3
  Dvalue = 5.86
  Group = -> [La_element002,O_element052,S_element015]
  conduct = 2
  density = 1
  expand = 3
  formula = G4_LANTHANUM_OXYSULFIDE
  name = G4_LANTHANUM_OXYSULFIDE
  specific = 4
FEATURE [App::DocumentObjectGroupPython] O_element053  label="O_element : 0.072"  # scripted group (container) (typed FeaturePython)
  n = 0.071682
FEATURE [App::DocumentObjectGroupPython] Pb_element002  label="Pb_element : 0.928"  # scripted group (container) (typed FeaturePython)
  n = 0.928318
FEATURE [App::DocumentObjectGroupPython] G4_LEAD_OXIDE  # scripted group (container) (typed FeaturePython)
  Dunit = g/cm3
  Dvalue = 9.53
  Group = -> [O_element053,Pb_element002]
  conduct = 2
  density = 1
  expand = 3
  formula = G4_LEAD_OXIDE
  name = G4_LEAD_OXIDE
  specific = 4
FEATURE [App::DocumentObjectGroupPython] Li_element001  label="Li_element : 1"  # scripted group (container) (typed FeaturePython)
  n = 1
  ref = Li_element
FEATURE [App::DocumentObjectGroupPython] N_element022  label="N_element : 011"  # scripted group (container) (typed FeaturePython)
  n = 1
  ref = N_element
FEATURE [App::DocumentObjectGroupPython] H_element049  label="H_element : 026"  # scripted group (container) (typed FeaturePython)
  n = 2
  ref = H_element
FEATURE [App::DocumentObjectGroupPython] G4_LITHIUM_AMIDE  # scripted group (container) (typed FeaturePython)
  Dunit = g/cm3
  Dvalue = 1.178
  Group = -> [Li_element001,N_element022,H_element049]
  conduct = 2
  density = 1
  expand = 3
  formula = G4_LITHIUM_AMIDE
  name = G4_LITHIUM_AMIDE
  specific = 4
FEATURE [App::DocumentObjectGroupPython] Li_element002  label="Li_element : 2"  # scripted group (container) (typed FeaturePython)
  n = 2
  ref = Li_element
FEATURE [App::DocumentObjectGroupPython] C_element055  label="C_element : 030"  # scripted group (container) (typed FeaturePython)
  n = 1
  ref = C_element
FEATURE [App::DocumentObjectGroupPython] O_element054  label="O_element : 028"  # scripted group (container) (typed FeaturePython)
  n = 3
  ref = O_element
FEATURE [App::DocumentObjectGroupPython] G4_LITHIUM_CARBONATE  # scripted group (container) (typed FeaturePython)
  Dunit = g/cm3
  Dvalue = 2.11
  Group = -> [Li_element002,C_element055,O_element054]
  conduct = 2
  density = 1
  expand = 3
  formula = G4_LITHIUM_CARBONATE
  name = G4_LITHIUM_CARBONATE
  specific = 4
FEATURE [App::DocumentObjectGroupPython] Li_element003  label="Li_element : 003"  # scripted group (container) (typed FeaturePython)
  n = 1
  ref = Li_element
FEATURE [App::DocumentObjectGroupPython] F_element012  label="F_element : 004"  # scripted group (container) (typed FeaturePython)
  n = 1
  ref = F_element
FEATURE [App::DocumentObjectGroupPython] G4_LITHIUM_FLUORIDE  # scripted group (container) (typed FeaturePython)
  Dunit = g/cm3
  Dvalue = 2.635
  Group = -> [Li_element003,F_element012]
  conduct = 2
  density = 1
  expand = 3
  formula = G4_LITHIUM_FLUORIDE
  name = G4_LITHIUM_FLUORIDE
  specific = 4
FEATURE [App::DocumentObjectGroupPython] Li_element004  label="Li_element : 004"  # scripted group (container) (typed FeaturePython)
  n = 1
  ref = Li_element
FEATURE [App::DocumentObjectGroupPython] H_element050  label="H_element : 027"  # scripted group (container) (typed FeaturePython)
  n = 1
  ref = H_element
FEATURE [App::DocumentObjectGroupPython] G4_LITHIUM_HYDRIDE  # scripted group (container) (typed FeaturePython)
  Dunit = g/cm3
  Dvalue = 0.82
  Group = -> [Li_element004,H_element050]
  conduct = 2
  density = 1
  expand = 3
  formula = G4_LITHIUM_HYDRIDE
  name = G4_LITHIUM_HYDRIDE
  specific = 4
FEATURE [App::DocumentObjectGroupPython] Li_element005  label="Li_element : 005"  # scripted group (container) (typed FeaturePython)
  n = 1
  ref = Li_element
FEATURE [App::DocumentObjectGroupPython] I_element003  label="I_element : 002"  # scripted group (container) (typed FeaturePython)
  n = 1
  ref = I_element
FEATURE [App::DocumentObjectGroupPython] G4_LITHIUM_IODIDE  # scripted group (container) (typed FeaturePython)
  Dunit = g/cm3
  Dvalue = 3.494
  Group = -> [Li_element005,I_element003]
  conduct = 2
  density = 1
  expand = 3
  formula = G4_LITHIUM_IODIDE
  name = G4_LITHIUM_IODIDE
  specific = 4
FEATURE [App::DocumentObjectGroupPython] Li_element006  label="Li_element : 006"  # scripted group (container) (typed FeaturePython)
  n = 2
  ref = Li_element
FEATURE [App::DocumentObjectGroupPython] O_element055  label="O_element : 029"  # scripted group (container) (typed FeaturePython)
  n = 1
  ref = O_element
FEATURE [App::DocumentObjectGroupPython] G4_LITHIUM_OXIDE  # scripted group (container) (typed FeaturePython)
  Dunit = g/cm3
  Dvalue = 2.013
  Group = -> [Li_element006,O_element055]
  conduct = 2
  density = 1
  expand = 3
  formula = G4_LITHIUM_OXIDE
  name = G4_LITHIUM_OXIDE
  specific = 4
FEATURE [App::DocumentObjectGroupPython] Li_element007  label="Li_element : 007"  # scripted group (container) (typed FeaturePython)
  n = 2
  ref = Li_element
FEATURE [App::DocumentObjectGroupPython] B_element005  label="B_element : 005"  # scripted group (container) (typed FeaturePython)
  n = 4
  ref = B_element
FEATURE [App::DocumentObjectGroupPython] O_element056  label="O_element : 7"  # scripted group (container) (typed FeaturePython)
  n = 7
  ref = O_element
FEATURE [App::DocumentObjectGroupPython] G4_LITHIUM_TETRABORATE  # scripted group (container) (typed FeaturePython)
  Dunit = g/cm3
  Dvalue = 2.44
  Group = -> [Li_element007,B_element005,O_element056]
  conduct = 2
  density = 1
  expand = 3
  formula = G4_LITHIUM_TETRABORATE
  name = G4_LITHIUM_TETRABORATE
  specific = 4
FEATURE [App::DocumentObjectGroupPython] H_element051  label="H_element : 0.105"  # scripted group (container) (typed FeaturePython)
  n = 0.105
FEATURE [App::DocumentObjectGroupPython] C_element056  label="C_element : 0.083"  # scripted group (container) (typed FeaturePython)
  n = 0.083
FEATURE [App::DocumentObjectGroupPython] N_element023  label="N_element : 0.023"  # scripted group (container) (typed FeaturePython)
  n = 0.023
FEATURE [App::DocumentObjectGroupPython] O_element057  label="O_element : 0.779"  # scripted group (container) (typed FeaturePython)
  n = 0.779
FEATURE [App::DocumentObjectGroupPython] Na_element010  label="Na_element : 0.097"  # scripted group (container) (typed FeaturePython)
  n = 0.002
FEATURE [App::DocumentObjectGroupPython] P_element006  label="P_element : 0.105"  # scripted group (container) (typed FeaturePython)
  n = 0.001
FEATURE [App::DocumentObjectGroupPython] S_element016  label="S_element : 0.017"  # scripted group (container) (typed FeaturePython)
  n = 0.002
FEATURE [App::DocumentObjectGroupPython] Cl_element014  label="Cl_element : 0.587"  # scripted group (container) (typed FeaturePython)
  n = 0.003
FEATURE [App::DocumentObjectGroupPython] K_element005  label="K_element : 0.015"  # scripted group (container) (typed FeaturePython)
  n = 0.002
FEATURE [App::DocumentObjectGroupPython] G4_LUNG_ICRP  # scripted group (container) (typed FeaturePython)
  Dunit = g/cm3
  Dvalue = 1.04
  Group = -> [H_element051,C_element056,N_element023,O_element057,Na_element010,P_element006,S_element016,Cl_element014,K_element005]
  conduct = 2
  density = 1
  expand = 3
  formula = G4_LUNG_ICRP
  name = G4_LUNG_ICRP
  specific = 4
FEATURE [App::DocumentObjectGroupPython] H_element052  label="H_element : 0.116"  # scripted group (container) (typed FeaturePython)
  n = 0.114318
FEATURE [App::DocumentObjectGroupPython] C_element057  label="C_element : 0.656"  # scripted group (container) (typed FeaturePython)
  n = 0.655824
FEATURE [App::DocumentObjectGroupPython] O_element058  label="O_element : 0.092"  # scripted group (container) (typed FeaturePython)
  n = 0.0921831
FEATURE [App::DocumentObjectGroupPython] Mg_element004  label="Mg_element : 0.135"  # scripted group (container) (typed FeaturePython)
  n = 0.134792
FEATURE [App::DocumentObjectGroupPython] Ca_element013  label="Ca_element : 0.003"  # scripted group (container) (typed FeaturePython)
  n = 0.002883
FEATURE [App::DocumentObjectGroupPython] G4_M3_WAX  # scripted group (container) (typed FeaturePython)
  Dunit = g/cm3
  Dvalue = 1.05
  Group = -> [H_element052,C_element057,O_element058,Mg_element004,Ca_element013]
  conduct = 2
  density = 1
  expand = 3
  formula = G4_M3_WAX
  name = G4_M3_WAX
  specific = 4
FEATURE [App::DocumentObjectGroupPython] Mg_element005  label="Mg_element : 1"  # scripted group (container) (typed FeaturePython)
  n = 1
  ref = Mg_element
FEATURE [App::DocumentObjectGroupPython] C_element058  label="C_element : 031"  # scripted group (container) (typed FeaturePython)
  n = 1
  ref = C_element
FEATURE [App::DocumentObjectGroupPython] O_element059  label="O_element : 030"  # scripted group (container) (typed FeaturePython)
  n = 3
  ref = O_element
FEATURE [App::DocumentObjectGroupPython] G4_MAGNESIUM_CARBONATE  # scripted group (container) (typed FeaturePython)
  Dunit = g/cm3
  Dvalue = 2.958
  Group = -> [Mg_element005,C_element058,O_element059]
  conduct = 2
  density = 1
  expand = 3
  formula = G4_MAGNESIUM_CARBONATE
  name = G4_MAGNESIUM_CARBONATE
  specific = 4
FEATURE [App::DocumentObjectGroupPython] Mg_element006  label="Mg_element : 002"  # scripted group (container) (typed FeaturePython)
  n = 1
  ref = Mg_element
FEATURE [App::DocumentObjectGroupPython] F_element013  label="F_element : 005"  # scripted group (container) (typed FeaturePython)
  n = 2
  ref = F_element
FEATURE [App::DocumentObjectGroupPython] G4_MAGNESIUM_FLUORIDE  # scripted group (container) (typed FeaturePython)
  Dunit = g/cm3
  Dvalue = 3
  Group = -> [Mg_element006,F_element013]
  conduct = 2
  density = 1
  expand = 3
  formula = G4_MAGNESIUM_FLUORIDE
  name = G4_MAGNESIUM_FLUORIDE
  specific = 4
FEATURE [App::DocumentObjectGroupPython] Mg_element007  label="Mg_element : 003"  # scripted group (container) (typed FeaturePython)
  n = 1
  ref = Mg_element
FEATURE [App::DocumentObjectGroupPython] O_element060  label="O_element : 031"  # scripted group (container) (typed FeaturePython)
  n = 1
  ref = O_element
FEATURE [App::DocumentObjectGroupPython] G4_MAGNESIUM_OXIDE  # scripted group (container) (typed FeaturePython)
  Dunit = g/cm3
  Dvalue = 3.58
  Group = -> [Mg_element007,O_element060]
  conduct = 2
  density = 1
  expand = 3
  formula = G4_MAGNESIUM_OXIDE
  name = G4_MAGNESIUM_OXIDE
  specific = 4
FEATURE [App::DocumentObjectGroupPython] Mg_element008  label="Mg_element : 004"  # scripted group (container) (typed FeaturePython)
  n = 1
  ref = Mg_element
FEATURE [App::DocumentObjectGroupPython] B_element006  label="B_element : 006"  # scripted group (container) (typed FeaturePython)
  n = 4
  ref = B_element
FEATURE [App::DocumentObjectGroupPython] O_element061  label="O_element : 032"  # scripted group (container) (typed FeaturePython)
  n = 7
  ref = O_element
FEATURE [App::DocumentObjectGroupPython] G4_MAGNESIUM_TETRABORATE  # scripted group (container) (typed FeaturePython)
  Dunit = g/cm3
  Dvalue = 2.53
  Group = -> [Mg_element008,B_element006,O_element061]
  conduct = 2
  density = 1
  expand = 3
  formula = G4_MAGNESIUM_TETRABORATE
  name = G4_MAGNESIUM_TETRABORATE
  specific = 4
FEATURE [App::DocumentObjectGroupPython] Hg_element001  label="Hg_element : 1"  # scripted group (container) (typed FeaturePython)
  n = 1
  ref = Hg_element
FEATURE [App::DocumentObjectGroupPython] I_element004  label="I_element : 2"  # scripted group (container) (typed FeaturePython)
  n = 2
  ref = I_element
FEATURE [App::DocumentObjectGroupPython] G4_MERCURIC_IODIDE  # scripted group (container) (typed FeaturePython)
  Dunit = g/cm3
  Dvalue = 6.36
  Group = -> [Hg_element001,I_element004]
  conduct = 2
  density = 1
  expand = 3
  formula = G4_MERCURIC_IODIDE
  name = G4_MERCURIC_IODIDE
  specific = 4
FEATURE [App::DocumentObjectGroupPython] C_element059  label="C_element : 032"  # scripted group (container) (typed FeaturePython)
  n = 1
  ref = C_element
FEATURE [App::DocumentObjectGroupPython] H_element053  label="H_element : 028"  # scripted group (container) (typed FeaturePython)
  n = 4
  ref = H_element
FEATURE [App::DocumentObjectGroupPython] G4_METHANE  # scripted group (container) (typed FeaturePython)
  Dunit = g/cm3
  Dvalue = 0.000667151
  Group = -> [C_element059,H_element053]
  conduct = 2
  density = 1
  expand = 3
  formula = G4_METHANE
  name = G4_METHANE
  specific = 4
FEATURE [App::DocumentObjectGroupPython] C_element060  label="C_element : 033"  # scripted group (container) (typed FeaturePython)
  n = 1
  ref = C_element
FEATURE [App::DocumentObjectGroupPython] H_element054  label="H_element : 029"  # scripted group (container) (typed FeaturePython)
  n = 4
  ref = H_element
FEATURE [App::DocumentObjectGroupPython] O_element062  label="O_element : 033"  # scripted group (container) (typed FeaturePython)
  n = 1
  ref = O_element
FEATURE [App::DocumentObjectGroupPython] G4_METHANOL  # scripted group (container) (typed FeaturePython)
  Dunit = g/cm3
  Dvalue = 0.7914
  Group = -> [C_element060,H_element054,O_element062]
  conduct = 2
  density = 1
  expand = 3
  formula = G4_METHANOL
  name = G4_METHANOL
  specific = 4
FEATURE [App::DocumentObjectGroupPython] H_element055  label="H_element : 0.134"  # scripted group (container) (typed FeaturePython)
  n = 0.13404
FEATURE [App::DocumentObjectGroupPython] C_element061  label="C_element : 0.778"  # scripted group (container) (typed FeaturePython)
  n = 0.77796
FEATURE [App::DocumentObjectGroupPython] O_element063  label="O_element : 0.035"  # scripted group (container) (typed FeaturePython)
  n = 0.03502
FEATURE [App::DocumentObjectGroupPython] Mg_element009  label="Mg_element : 0.039"  # scripted group (container) (typed FeaturePython)
  n = 0.038594
FEATURE [App::DocumentObjectGroupPython] Ti_element002  label="Ti_element : 0.014"  # scripted group (container) (typed FeaturePython)
  n = 0.014386
FEATURE [App::DocumentObjectGroupPython] G4_MIX_D_WAX  # scripted group (container) (typed FeaturePython)
  Dunit = g/cm3
  Dvalue = 0.99
  Group = -> [H_element055,C_element061,O_element063,Mg_element009,Ti_element002]
  conduct = 2
  density = 1
  expand = 3
  formula = G4_MIX_D_WAX
  name = G4_MIX_D_WAX
  specific = 4
FEATURE [App::DocumentObjectGroupPython] H_element056  label="H_element : 0.135"  # scripted group (container) (typed FeaturePython)
  n = 0.081192
FEATURE [App::DocumentObjectGroupPython] C_element062  label="C_element : 0.583"  # scripted group (container) (typed FeaturePython)
  n = 0.583442
FEATURE [App::DocumentObjectGroupPython] N_element024  label="N_element : 0.018"  # scripted group (container) (typed FeaturePython)
  n = 0.017798
FEATURE [App::DocumentObjectGroupPython] O_element064  label="O_element : 0.186"  # scripted group (container) (typed FeaturePython)
  n = 0.186381
FEATURE [App::DocumentObjectGroupPython] Mg_element010  label="Mg_element : 0.130"  # scripted group (container) (typed FeaturePython)
  n = 0.130287
FEATURE [App::DocumentObjectGroupPython] Cl_element015  label="Cl_element : 0.588"  # scripted group (container) (typed FeaturePython)
  n = 0.0009
FEATURE [App::DocumentObjectGroupPython] G4_MS20_TISSUE  # scripted group (container) (typed FeaturePython)
  Dunit = g/cm3
  Dvalue = 1
  Group = -> [H_element056,C_element062,N_element024,O_element064,Mg_element010,Cl_element015]
  conduct = 2
  density = 1
  expand = 3
  formula = G4_MS20_TISSUE
  name = G4_MS20_TISSUE
  specific = 4
FEATURE [App::DocumentObjectGroupPython] H_element057  label="H_element : 0.136"  # scripted group (container) (typed FeaturePython)
  n = 0.102
FEATURE [App::DocumentObjectGroupPython] C_element063  label="C_element : 0.143"  # scripted group (container) (typed FeaturePython)
  n = 0.143
FEATURE [App::DocumentObjectGroupPython] N_element025  label="N_element : 0.034"  # scripted group (container) (typed FeaturePython)
  n = 0.034
FEATURE [App::DocumentObjectGroupPython] O_element065  label="O_element : 0.710"  # scripted group (container) (typed FeaturePython)
  n = 0.71
FEATURE [App::DocumentObjectGroupPython] Na_element011  label="Na_element : 0.098"  # scripted group (container) (typed FeaturePython)
  n = 0.001
FEATURE [App::DocumentObjectGroupPython] P_element007  label="P_element : 0.002"  # scripted group (container) (typed FeaturePython)
  n = 0.002
FEATURE [App::DocumentObjectGroupPython] S_element017  label="S_element : 0.018"  # scripted group (container) (typed FeaturePython)
  n = 0.003
FEATURE [App::DocumentObjectGroupPython] Cl_element016  label="Cl_element : 0.589"  # scripted group (container) (typed FeaturePython)
  n = 0.001
FEATURE [App::DocumentObjectGroupPython] K_element006  label="K_element : 0.004"  # scripted group (container) (typed FeaturePython)
  n = 0.004
FEATURE [App::DocumentObjectGroupPython] G4_MUSCLE_SKELETAL_ICRP  # scripted group (container) (typed FeaturePython)
  Dunit = g/cm3
  Dvalue = 1.05
  Group = -> [H_element057,C_element063,N_element025,O_element065,Na_element011,P_element007,S_element017,Cl_element016,K_element006]
  conduct = 2
  density = 1
  expand = 3
  formula = G4_MUSCLE_SKELETAL_ICRP
  name = G4_MUSCLE_SKELETAL_ICRP
  specific = 4
FEATURE [App::DocumentObjectGroupPython] H_element058  label="H_element : 0.137"  # scripted group (container) (typed FeaturePython)
  n = 0.102102
FEATURE [App::DocumentObjectGroupPython] C_element064  label="C_element : 0.123"  # scripted group (container) (typed FeaturePython)
  n = 0.123123
FEATURE [App::DocumentObjectGroupPython] N_element026  label="N_element : 0.756"  # scripted group (container) (typed FeaturePython)
  n = 0.035035
FEATURE [App::DocumentObjectGroupPython] O_element066  label="O_element : 0.730"  # scripted group (container) (typed FeaturePython)
  n = 0.72973
FEATURE [App::DocumentObjectGroupPython] Na_element012  label="Na_element : 0.099"  # scripted group (container) (typed FeaturePython)
  n = 0.001001
FEATURE [App::DocumentObjectGroupPython] P_element008  label="P_element : 0.106"  # scripted group (container) (typed FeaturePython)
  n = 0.002002
FEATURE [App::DocumentObjectGroupPython] S_element018  label="S_element : 0.019"  # scripted group (container) (typed FeaturePython)
  n = 0.004004
FEATURE [App::DocumentObjectGroupPython] K_element007  label="K_element : 0.016"  # scripted group (container) (typed FeaturePython)
  n = 0.003003
FEATURE [App::DocumentObjectGroupPython] G4_MUSCLE_STRIATED_ICRU  # scripted group (container) (typed FeaturePython)
  Dunit = g/cm3
  Dvalue = 1.04
  Group = -> [H_element058,C_element064,N_element026,O_element066,Na_element012,P_element008,S_element018,K_element007]
  conduct = 2
  density = 1
  expand = 3
  formula = G4_MUSCLE_STRIATED_ICRU
  name = G4_MUSCLE_STRIATED_ICRU
  specific = 4
FEATURE [App::DocumentObjectGroupPython] H_element059  label="H_element : 0.098"  # scripted group (container) (typed FeaturePython)
  n = 0.0982341
FEATURE [App::DocumentObjectGroupPython] C_element065  label="C_element : 0.156"  # scripted group (container) (typed FeaturePython)
  n = 0.156214
FEATURE [App::DocumentObjectGroupPython] N_element027  label="N_element : 0.757"  # scripted group (container) (typed FeaturePython)
  n = 0.035451
FEATURE [App::DocumentObjectGroupPython] O_element067  label="O_element : 0.880"  # scripted group (container) (typed FeaturePython)
  n = 0.710101
FEATURE [App::DocumentObjectGroupPython] G4_MUSCLE_WITH_SUCROSE  # scripted group (container) (typed FeaturePython)
  Dunit = g/cm3
  Dvalue = 1.11
  Group = -> [H_element059,C_element065,N_element027,O_element067]
  conduct = 2
  density = 1
  expand = 3
  formula = G4_MUSCLE_WITH_SUCROSE
  name = G4_MUSCLE_WITH_SUCROSE
  specific = 4
FEATURE [App::DocumentObjectGroupPython] H_element060  label="H_element : 0.138"  # scripted group (container) (typed FeaturePython)
  n = 0.101969
FEATURE [App::DocumentObjectGroupPython] C_element066  label="C_element : 0.120"  # scripted group (container) (typed FeaturePython)
  n = 0.120058
FEATURE [App::DocumentObjectGroupPython] N_element028  label="N_element : 0.758"  # scripted group (container) (typed FeaturePython)
  n = 0.035451
FEATURE [App::DocumentObjectGroupPython] O_element068  label="O_element : 0.743"  # scripted group (container) (typed FeaturePython)
  n = 0.742522
FEATURE [App::DocumentObjectGroupPython] G4_MUSCLE_WITHOUT_SUCROSE  # scripted group (container) (typed FeaturePython)
  Dunit = g/cm3
  Dvalue = 1.07
  Group = -> [H_element060,C_element066,N_element028,O_element068]
  conduct = 2
  density = 1
  expand = 3
  formula = G4_MUSCLE_WITHOUT_SUCROSE
  name = G4_MUSCLE_WITHOUT_SUCROSE
  specific = 4
FEATURE [App::DocumentObjectGroupPython] C_element067  label="C_element : 10"  # scripted group (container) (typed FeaturePython)
  n = 10
  ref = C_element
FEATURE [App::DocumentObjectGroupPython] H_element061  label="H_element : 030"  # scripted group (container) (typed FeaturePython)
  n = 8
  ref = H_element
FEATURE [App::DocumentObjectGroupPython] G4_NAPHTHALENE  # scripted group (container) (typed FeaturePython)
  Dunit = g/cm3
  Dvalue = 1.145
  Group = -> [C_element067,H_element061]
  conduct = 2
  density = 1
  expand = 3
  formula = G4_NAPHTHALENE
  name = G4_NAPHTHALENE
  specific = 4
FEATURE [App::DocumentObjectGroupPython] C_element068  label="C_element : 034"  # scripted group (container) (typed FeaturePython)
  n = 6
  ref = C_element
FEATURE [App::DocumentObjectGroupPython] H_element062  label="H_element : 031"  # scripted group (container) (typed FeaturePython)
  n = 5
  ref = H_element
FEATURE [App::DocumentObjectGroupPython] N_element029  label="N_element : 012"  # scripted group (container) (typed FeaturePython)
  n = 1
  ref = N_element
FEATURE [App::DocumentObjectGroupPython] O_element069  label="O_element : 034"  # scripted group (container) (typed FeaturePython)
  n = 2
  ref = O_element
FEATURE [App::DocumentObjectGroupPython] G4_NITROBENZENE  # scripted group (container) (typed FeaturePython)
  Dunit = g/cm3
  Dvalue = 1.19867
  Group = -> [C_element068,H_element062,N_element029,O_element069]
  conduct = 2
  density = 1
  expand = 3
  formula = G4_NITROBENZENE
  name = G4_NITROBENZENE
  specific = 4
FEATURE [App::DocumentObjectGroupPython] N_element030  label="N_element : 013"  # scripted group (container) (typed FeaturePython)
  n = 2
  ref = N_element
FEATURE [App::DocumentObjectGroupPython] O_element070  label="O_element : 035"  # scripted group (container) (typed FeaturePython)
  n = 1
  ref = O_element
FEATURE [App::DocumentObjectGroupPython] G4_NITROUS_OXIDE  # scripted group (container) (typed FeaturePython)
  Dunit = g/cm3
  Dvalue = 0.00183094
  Group = -> [N_element030,O_element070]
  conduct = 2
  density = 1
  expand = 3
  formula = G4_NITROUS_OXIDE
  name = G4_NITROUS_OXIDE
  specific = 4
FEATURE [App::DocumentObjectGroupPython] H_element063  label="H_element : 0.104"  # scripted group (container) (typed FeaturePython)
  n = 0.103509
FEATURE [App::DocumentObjectGroupPython] C_element069  label="C_element : 0.648"  # scripted group (container) (typed FeaturePython)
  n = 0.648416
FEATURE [App::DocumentObjectGroupPython] N_element031  label="N_element : 0.100"  # scripted group (container) (typed FeaturePython)
  n = 0.0995361
FEATURE [App::DocumentObjectGroupPython] O_element071  label="O_element : 0.149"  # scripted group (container) (typed FeaturePython)
  n = 0.148539
FEATURE [App::DocumentObjectGroupPython] G4_NYLON_8062  label="G4_NYLON-8062"  # scripted group (container) (typed FeaturePython)
  Dunit = g/cm3
  Dvalue = 1.08
  Group = -> [H_element063,C_element069,N_element031,O_element071]
  conduct = 2
  density = 1
  expand = 3
  formula = G4_NYLON-8062
  name = G4_NYLON-8062
  specific = 4
FEATURE [App::DocumentObjectGroupPython] C_element070  label="C_element : 035"  # scripted group (container) (typed FeaturePython)
  n = 6
  ref = C_element
FEATURE [App::DocumentObjectGroupPython] H_element064  label="H_element : 11"  # scripted group (container) (typed FeaturePython)
  n = 11
  ref = H_element
FEATURE [App::DocumentObjectGroupPython] N_element032  label="N_element : 014"  # scripted group (container) (typed FeaturePython)
  n = 1
  ref = N_element
FEATURE [App::DocumentObjectGroupPython] O_element072  label="O_element : 036"  # scripted group (container) (typed FeaturePython)
  n = 1
  ref = O_element
FEATURE [App::DocumentObjectGroupPython] G4_NYLON_6_6  label="G4_NYLON-6-6"  # scripted group (container) (typed FeaturePython)
  Dunit = g/cm3
  Dvalue = 1.14
  Group = -> [C_element070,H_element064,N_element032,O_element072]
  conduct = 2
  density = 1
  expand = 3
  formula = G4_NYLON-6-6
  name = G4_NYLON-6-6
  specific = 4
FEATURE [App::DocumentObjectGroupPython] H_element065  label="H_element : 0.139"  # scripted group (container) (typed FeaturePython)
  n = 0.107062
FEATURE [App::DocumentObjectGroupPython] C_element071  label="C_element : 0.680"  # scripted group (container) (typed FeaturePython)
  n = 0.680449
FEATURE [App::DocumentObjectGroupPython] N_element033  label="N_element : 0.099"  # scripted group (container) (typed FeaturePython)
  n = 0.099189
FEATURE [App::DocumentObjectGroupPython] O_element073  label="O_element : 0.113"  # scripted group (container) (typed FeaturePython)
  n = 0.1133
FEATURE [App::DocumentObjectGroupPython] G4_NYLON_6_10  label="G4_NYLON-6-10"  # scripted group (container) (typed FeaturePython)
  Dunit = g/cm3
  Dvalue = 1.14
  Group = -> [H_element065,C_element071,N_element033,O_element073]
  conduct = 2
  density = 1
  expand = 3
  formula = G4_NYLON-6-10
  name = G4_NYLON-6-10
  specific = 4
FEATURE [App::DocumentObjectGroupPython] H_element066  label="H_element : 0.140"  # scripted group (container) (typed FeaturePython)
  n = 0.115476
FEATURE [App::DocumentObjectGroupPython] C_element072  label="C_element : 0.721"  # scripted group (container) (typed FeaturePython)
  n = 0.720818
FEATURE [App::DocumentObjectGroupPython] N_element034  label="N_element : 0.076"  # scripted group (container) (typed FeaturePython)
  n = 0.0764169
FEATURE [App::DocumentObjectGroupPython] O_element074  label="O_element : 0.087"  # scripted group (container) (typed FeaturePython)
  n = 0.0872889
FEATURE [App::DocumentObjectGroupPython] G4_NYLON_11_RILSAN  label="G4_NYLON-11_RILSAN"  # scripted group (container) (typed FeaturePython)
  Dunit = g/cm3
  Dvalue = 1.425
  Group = -> [H_element066,C_element072,N_element034,O_element074]
  conduct = 2
  density = 1
  expand = 3
  formula = G4_NYLON-11_RILSAN
  name = G4_NYLON-11_RILSAN
  specific = 4
FEATURE [App::DocumentObjectGroupPython] C_element073  label="C_element : 8"  # scripted group (container) (typed FeaturePython)
  n = 8
  ref = C_element
FEATURE [App::DocumentObjectGroupPython] H_element067  label="H_element : 18"  # scripted group (container) (typed FeaturePython)
  n = 18
  ref = H_element
FEATURE [App::DocumentObjectGroupPython] G4_OCTANE  # scripted group (container) (typed FeaturePython)
  Dunit = g/cm3
  Dvalue = 0.7026
  Group = -> [C_element073,H_element067]
  conduct = 2
  density = 1
  expand = 3
  formula = G4_OCTANE
  name = G4_OCTANE
  specific = 4
FEATURE [App::DocumentObjectGroupPython] C_element074  label="C_element : 25"  # scripted group (container) (typed FeaturePython)
  n = 25
  ref = C_element
FEATURE [App::DocumentObjectGroupPython] H_element068  label="H_element : 52"  # scripted group (container) (typed FeaturePython)
  n = 52
  ref = H_element
FEATURE [App::DocumentObjectGroupPython] G4_PARAFFIN  # scripted group (container) (typed FeaturePython)
  Dunit = g/cm3
  Dvalue = 0.93
  Group = -> [C_element074,H_element068]
  conduct = 2
  density = 1
  expand = 3
  formula = G4_PARAFFIN
  name = G4_PARAFFIN
  specific = 4
FEATURE [App::DocumentObjectGroupPython] C_element075  label="C_element : 036"  # scripted group (container) (typed FeaturePython)
  n = 5
  ref = C_element
FEATURE [App::DocumentObjectGroupPython] H_element069  label="H_element : 032"  # scripted group (container) (typed FeaturePython)
  n = 12
  ref = H_element
FEATURE [App::DocumentObjectGroupPython] G4_N_PENTANE  label="G4_N-PENTANE"  # scripted group (container) (typed FeaturePython)
  Dunit = g/cm3
  Dvalue = 0.6262
  Group = -> [C_element075,H_element069]
  conduct = 2
  density = 1
  expand = 3
  formula = G4_N-PENTANE
  name = G4_N-PENTANE
  specific = 4
FEATURE [App::DocumentObjectGroupPython] H_element070  label="H_element : 0.014"  # scripted group (container) (typed FeaturePython)
  n = 0.0141
FEATURE [App::DocumentObjectGroupPython] C_element076  label="C_element : 0.072"  # scripted group (container) (typed FeaturePython)
  n = 0.072261
FEATURE [App::DocumentObjectGroupPython] N_element035  label="N_element : 0.019"  # scripted group (container) (typed FeaturePython)
  n = 0.01932
FEATURE [App::DocumentObjectGroupPython] O_element075  label="O_element : 0.066"  # scripted group (container) (typed FeaturePython)
  n = 0.066101
FEATURE [App::DocumentObjectGroupPython] S_element019  label="S_element : 0.020"  # scripted group (container) (typed FeaturePython)
  n = 0.00189
FEATURE [App::DocumentObjectGroupPython] Br_element004  label="Br_element : 0.349"  # scripted group (container) (typed FeaturePython)
  n = 0.349103
FEATURE [App::DocumentObjectGroupPython] Ag_element001  label="Ag_element : 0.474"  # scripted group (container) (typed FeaturePython)
  n = 0.474105
FEATURE [App::DocumentObjectGroupPython] I_element005  label="I_element : 0.003"  # scripted group (container) (typed FeaturePython)
  n = 0.00312
FEATURE [App::DocumentObjectGroupPython] G4_PHOTO_EMULSION  # scripted group (container) (typed FeaturePython)
  Dunit = g/cm3
  Dvalue = 3.815
  Group = -> [H_element070,C_element076,N_element035,O_element075,S_element019,Br_element004,Ag_element001,I_element005]
  conduct = 2
  density = 1
  expand = 3
  formula = G4_PHOTO_EMULSION
  name = G4_PHOTO_EMULSION
  specific = 4
FEATURE [App::DocumentObjectGroupPython] C_element077  label="C_element : 9"  # scripted group (container) (typed FeaturePython)
  n = 9
  ref = C_element
FEATURE [App::DocumentObjectGroupPython] H_element071  label="H_element : 033"  # scripted group (container) (typed FeaturePython)
  n = 10
  ref = H_element
FEATURE [App::DocumentObjectGroupPython] G4_PLASTIC_SC_VINYLTOLUENE  # scripted group (container) (typed FeaturePython)
  Dunit = g/cm3
  Dvalue = 1.032
  Group = -> [C_element077,H_element071]
  conduct = 2
  density = 1
  expand = 3
  formula = G4_PLASTIC_SC_VINYLTOLUENE
  name = G4_PLASTIC_SC_VINYLTOLUENE
  specific = 4
FEATURE [App::DocumentObjectGroupPython] Pu_element001  label="Pu_element : 1"  # scripted group (container) (typed FeaturePython)
  n = 1
  ref = Pu_element
FEATURE [App::DocumentObjectGroupPython] O_element076  label="O_element : 037"  # scripted group (container) (typed FeaturePython)
  n = 2
  ref = O_element
FEATURE [App::DocumentObjectGroupPython] G4_PLUTONIUM_DIOXIDE  # scripted group (container) (typed FeaturePython)
  Dunit = g/cm3
  Dvalue = 11.46
  Group = -> [Pu_element001,O_element076]
  conduct = 2
  density = 1
  expand = 3
  formula = G4_PLUTONIUM_DIOXIDE
  name = G4_PLUTONIUM_DIOXIDE
  specific = 4
FEATURE [App::DocumentObjectGroupPython] C_element078  label="C_element : 037"  # scripted group (container) (typed FeaturePython)
  n = 3
  ref = C_element
FEATURE [App::DocumentObjectGroupPython] H_element072  label="H_element : 034"  # scripted group (container) (typed FeaturePython)
  n = 3
  ref = H_element
FEATURE [App::DocumentObjectGroupPython] N_element036  label="N_element : 015"  # scripted group (container) (typed FeaturePython)
  n = 1
  ref = N_element
FEATURE [App::DocumentObjectGroupPython] G4_POLYACRYLONITRILE  # scripted group (container) (typed FeaturePython)
  Dunit = g/cm3
  Dvalue = 1.17
  Group = -> [C_element078,H_element072,N_element036]
  conduct = 2
  density = 1
  expand = 3
  formula = G4_POLYACRYLONITRILE
  name = G4_POLYACRYLONITRILE
  specific = 4
FEATURE [App::DocumentObjectGroupPython] C_element079  label="C_element : 16"  # scripted group (container) (typed FeaturePython)
  n = 16
  ref = C_element
FEATURE [App::DocumentObjectGroupPython] H_element073  label="H_element : 035"  # scripted group (container) (typed FeaturePython)
  n = 14
  ref = H_element
FEATURE [App::DocumentObjectGroupPython] O_element077  label="O_element : 038"  # scripted group (container) (typed FeaturePython)
  n = 3
  ref = O_element
FEATURE [App::DocumentObjectGroupPython] G4_POLYCARBONATE  # scripted group (container) (typed FeaturePython)
  Dunit = g/cm3
  Dvalue = 1.2
  Group = -> [C_element079,H_element073,O_element077]
  conduct = 2
  density = 1
  expand = 3
  formula = G4_POLYCARBONATE
  name = G4_POLYCARBONATE
  specific = 4
FEATURE [App::DocumentObjectGroupPython] C_element080  label="C_element : 038"  # scripted group (container) (typed FeaturePython)
  n = 8
  ref = C_element
FEATURE [App::DocumentObjectGroupPython] H_element074  label="H_element : 036"  # scripted group (container) (typed FeaturePython)
  n = 7
  ref = H_element
FEATURE [App::DocumentObjectGroupPython] Cl_element017  label="Cl_element : 007"  # scripted group (container) (typed FeaturePython)
  n = 1
  ref = Cl_element
FEATURE [App::DocumentObjectGroupPython] G4_POLYCHLOROSTYRENE  # scripted group (container) (typed FeaturePython)
  Dunit = g/cm3
  Dvalue = 1.3
  Group = -> [C_element080,H_element074,Cl_element017]
  conduct = 2
  density = 1
  expand = 3
  formula = G4_POLYCHLOROSTYRENE
  name = G4_POLYCHLOROSTYRENE
  specific = 4
FEATURE [App::DocumentObjectGroupPython] C_element081  label="C_element : 039"  # scripted group (container) (typed FeaturePython)
  n = 1
  ref = C_element
FEATURE [App::DocumentObjectGroupPython] H_element075  label="H_element : 037"  # scripted group (container) (typed FeaturePython)
  n = 2
  ref = H_element
FEATURE [App::DocumentObjectGroupPython] G4_POLYETHYLENE  # scripted group (container) (typed FeaturePython)
  Dunit = g/cm3
  Dvalue = 0.94
  Group = -> [C_element081,H_element075]
  conduct = 2
  density = 1
  expand = 3
  formula = G4_POLYETHYLENE
  name = G4_POLYETHYLENE
  specific = 4
FEATURE [App::DocumentObjectGroupPython] C_element082  label="C_element : 040"  # scripted group (container) (typed FeaturePython)
  n = 10
  ref = C_element
FEATURE [App::DocumentObjectGroupPython] H_element076  label="H_element : 038"  # scripted group (container) (typed FeaturePython)
  n = 8
  ref = H_element
FEATURE [App::DocumentObjectGroupPython] O_element078  label="O_element : 039"  # scripted group (container) (typed FeaturePython)
  n = 4
  ref = O_element
FEATURE [App::DocumentObjectGroupPython] G4_MYLAR  # scripted group (container) (typed FeaturePython)
  Dunit = g/cm3
  Dvalue = 1.4
  Group = -> [C_element082,H_element076,O_element078]
  conduct = 2
  density = 1
  expand = 3
  formula = G4_MYLAR
  name = G4_MYLAR
  specific = 4
FEATURE [App::DocumentObjectGroupPython] C_element083  label="C_element : 041"  # scripted group (container) (typed FeaturePython)
  n = 5
  ref = C_element
FEATURE [App::DocumentObjectGroupPython] H_element077  label="H_element : 039"  # scripted group (container) (typed FeaturePython)
  n = 8
  ref = H_element
FEATURE [App::DocumentObjectGroupPython] O_element079  label="O_element : 040"  # scripted group (container) (typed FeaturePython)
  n = 2
  ref = O_element
FEATURE [App::DocumentObjectGroupPython] G4_PLEXIGLASS  # scripted group (container) (typed FeaturePython)
  Dunit = g/cm3
  Dvalue = 1.19
  Group = -> [C_element083,H_element077,O_element079]
  conduct = 2
  density = 1
  expand = 3
  formula = G4_PLEXIGLASS
  name = G4_PLEXIGLASS
  specific = 4
FEATURE [App::DocumentObjectGroupPython] C_element084  label="C_element : 042"  # scripted group (container) (typed FeaturePython)
  n = 1
  ref = C_element
FEATURE [App::DocumentObjectGroupPython] H_element078  label="H_element : 040"  # scripted group (container) (typed FeaturePython)
  n = 2
  ref = H_element
FEATURE [App::DocumentObjectGroupPython] O_element080  label="O_element : 041"  # scripted group (container) (typed FeaturePython)
  n = 1
  ref = O_element
FEATURE [App::DocumentObjectGroupPython] G4_POLYOXYMETHYLENE  # scripted group (container) (typed FeaturePython)
  Dunit = g/cm3
  Dvalue = 1.425
  Group = -> [C_element084,H_element078,O_element080]
  conduct = 2
  density = 1
  expand = 3
  formula = G4_POLYOXYMETHYLENE
  name = G4_POLYOXYMETHYLENE
  specific = 4
FEATURE [App::DocumentObjectGroupPython] C_element085  label="C_element : 043"  # scripted group (container) (typed FeaturePython)
  n = 2
  ref = C_element
FEATURE [App::DocumentObjectGroupPython] H_element079  label="H_element : 041"  # scripted group (container) (typed FeaturePython)
  n = 4
  ref = H_element
FEATURE [App::DocumentObjectGroupPython] G4_POLYPROPYLENE  # scripted group (container) (typed FeaturePython)
  Dunit = g/cm3
  Dvalue = 0.9
  Group = -> [C_element085,H_element079]
  conduct = 2
  density = 1
  expand = 3
  formula = G4_POLYPROPYLENE
  name = G4_POLYPROPYLENE
  specific = 4
FEATURE [App::DocumentObjectGroupPython] C_element086  label="C_element : 044"  # scripted group (container) (typed FeaturePython)
  n = 8
  ref = C_element
FEATURE [App::DocumentObjectGroupPython] H_element080  label="H_element : 042"  # scripted group (container) (typed FeaturePython)
  n = 8
  ref = H_element
FEATURE [App::DocumentObjectGroupPython] G4_POLYSTYRENE  # scripted group (container) (typed FeaturePython)
  Dunit = g/cm3
  Dvalue = 1.06
  Group = -> [C_element086,H_element080]
  conduct = 2
  density = 1
  expand = 3
  formula = G4_POLYSTYRENE
  name = G4_POLYSTYRENE
  specific = 4
FEATURE [App::DocumentObjectGroupPython] C_element087  label="C_element : 045"  # scripted group (container) (typed FeaturePython)
  n = 2
  ref = C_element
FEATURE [App::DocumentObjectGroupPython] F_element014  label="F_element : 4"  # scripted group (container) (typed FeaturePython)
  n = 4
  ref = F_element
FEATURE [App::DocumentObjectGroupPython] G4_TEFLON  # scripted group (container) (typed FeaturePython)
  Dunit = g/cm3
  Dvalue = 2.2
  Group = -> [C_element087,F_element014]
  conduct = 2
  density = 1
  expand = 3
  formula = G4_TEFLON
  name = G4_TEFLON
  specific = 4
FEATURE [App::DocumentObjectGroupPython] C_element088  label="C_element : 046"  # scripted group (container) (typed FeaturePython)
  n = 2
  ref = C_element
FEATURE [App::DocumentObjectGroupPython] F_element015  label="F_element : 006"  # scripted group (container) (typed FeaturePython)
  n = 3
  ref = F_element
FEATURE [App::DocumentObjectGroupPython] Cl_element018  label="Cl_element : 008"  # scripted group (container) (typed FeaturePython)
  n = 1
  ref = Cl_element
FEATURE [App::DocumentObjectGroupPython] G4_POLYTRIFLUOROCHLOROETHYLENE  # scripted group (container) (typed FeaturePython)
  Dunit = g/cm3
  Dvalue = 2.1
  Group = -> [C_element088,F_element015,Cl_element018]
  conduct = 2
  density = 1
  expand = 3
  formula = G4_POLYTRIFLUOROCHLOROETHYLENE
  name = G4_POLYTRIFLUOROCHLOROETHYLENE
  specific = 4
FEATURE [App::DocumentObjectGroupPython] C_element089  label="C_element : 047"  # scripted group (container) (typed FeaturePython)
  n = 4
  ref = C_element
FEATURE [App::DocumentObjectGroupPython] H_element081  label="H_element : 043"  # scripted group (container) (typed FeaturePython)
  n = 6
  ref = H_element
FEATURE [App::DocumentObjectGroupPython] O_element081  label="O_element : 042"  # scripted group (container) (typed FeaturePython)
  n = 2
  ref = O_element
FEATURE [App::DocumentObjectGroupPython] G4_POLYVINYL_ACETATE  # scripted group (container) (typed FeaturePython)
  Dunit = g/cm3
  Dvalue = 1.19
  Group = -> [C_element089,H_element081,O_element081]
  conduct = 2
  density = 1
  expand = 3
  formula = G4_POLYVINYL_ACETATE
  name = G4_POLYVINYL_ACETATE
  specific = 4
FEATURE [App::DocumentObjectGroupPython] C_element090  label="C_element : 048"  # scripted group (container) (typed FeaturePython)
  n = 2
  ref = C_element
FEATURE [App::DocumentObjectGroupPython] H_element082  label="H_element : 044"  # scripted group (container) (typed FeaturePython)
  n = 4
  ref = H_element
FEATURE [App::DocumentObjectGroupPython] O_element082  label="O_element : 043"  # scripted group (container) (typed FeaturePython)
  n = 1
  ref = O_element
FEATURE [App::DocumentObjectGroupPython] G4_POLYVINYL_ALCOHOL  # scripted group (container) (typed FeaturePython)
  Dunit = g/cm3
  Dvalue = 1.3
  Group = -> [C_element090,H_element082,O_element082]
  conduct = 2
  density = 1
  expand = 3
  formula = G4_POLYVINYL_ALCOHOL
  name = G4_POLYVINYL_ALCOHOL
  specific = 4
FEATURE [App::DocumentObjectGroupPython] C_element091  label="C_element : 049"  # scripted group (container) (typed FeaturePython)
  n = 8
  ref = C_element
FEATURE [App::DocumentObjectGroupPython] H_element083  label="H_element : 045"  # scripted group (container) (typed FeaturePython)
  n = 14
  ref = H_element
FEATURE [App::DocumentObjectGroupPython] O_element083  label="O_element : 044"  # scripted group (container) (typed FeaturePython)
  n = 2
  ref = O_element
FEATURE [App::DocumentObjectGroupPython] G4_POLYVINYL_BUTYRAL  # scripted group (container) (typed FeaturePython)
  Dunit = g/cm3
  Dvalue = 1.12
  Group = -> [C_element091,H_element083,O_element083]
  conduct = 2
  density = 1
  expand = 3
  formula = G4_POLYVINYL_BUTYRAL
  name = G4_POLYVINYL_BUTYRAL
  specific = 4
FEATURE [App::DocumentObjectGroupPython] C_element092  label="C_element : 050"  # scripted group (container) (typed FeaturePython)
  n = 2
  ref = C_element
FEATURE [App::DocumentObjectGroupPython] H_element084  label="H_element : 046"  # scripted group (container) (typed FeaturePython)
  n = 3
  ref = H_element
FEATURE [App::DocumentObjectGroupPython] Cl_element019  label="Cl_element : 009"  # scripted group (container) (typed FeaturePython)
  n = 1
  ref = Cl_element
FEATURE [App::DocumentObjectGroupPython] G4_POLYVINYL_CHLORIDE  # scripted group (container) (typed FeaturePython)
  Dunit = g/cm3
  Dvalue = 1.3
  Group = -> [C_element092,H_element084,Cl_element019]
  conduct = 2
  density = 1
  expand = 3
  formula = G4_POLYVINYL_CHLORIDE
  name = G4_POLYVINYL_CHLORIDE
  specific = 4
FEATURE [App::DocumentObjectGroupPython] C_element093  label="C_element : 051"  # scripted group (container) (typed FeaturePython)
  n = 2
  ref = C_element
FEATURE [App::DocumentObjectGroupPython] H_element085  label="H_element : 047"  # scripted group (container) (typed FeaturePython)
  n = 2
  ref = H_element
FEATURE [App::DocumentObjectGroupPython] Cl_element020  label="Cl_element : 010"  # scripted group (container) (typed FeaturePython)
  n = 2
  ref = Cl_element
FEATURE [App::DocumentObjectGroupPython] G4_POLYVINYLIDENE_CHLORIDE  # scripted group (container) (typed FeaturePython)
  Dunit = g/cm3
  Dvalue = 1.7
  Group = -> [C_element093,H_element085,Cl_element020]
  conduct = 2
  density = 1
  expand = 3
  formula = G4_POLYVINYLIDENE_CHLORIDE
  name = G4_POLYVINYLIDENE_CHLORIDE
  specific = 4
FEATURE [App::DocumentObjectGroupPython] C_element094  label="C_element : 052"  # scripted group (container) (typed FeaturePython)
  n = 2
  ref = C_element
FEATURE [App::DocumentObjectGroupPython] H_element086  label="H_element : 048"  # scripted group (container) (typed FeaturePython)
  n = 2
  ref = H_element
FEATURE [App::DocumentObjectGroupPython] F_element016  label="F_element : 007"  # scripted group (container) (typed FeaturePython)
  n = 2
  ref = F_element
FEATURE [App::DocumentObjectGroupPython] G4_POLYVINYLIDENE_FLUORIDE  # scripted group (container) (typed FeaturePython)
  Dunit = g/cm3
  Dvalue = 1.76
  Group = -> [C_element094,H_element086,F_element016]
  conduct = 2
  density = 1
  expand = 3
  formula = G4_POLYVINYLIDENE_FLUORIDE
  name = G4_POLYVINYLIDENE_FLUORIDE
  specific = 4
FEATURE [App::DocumentObjectGroupPython] C_element095  label="C_element : 053"  # scripted group (container) (typed FeaturePython)
  n = 6
  ref = C_element
FEATURE [App::DocumentObjectGroupPython] H_element087  label="H_element : 9"  # scripted group (container) (typed FeaturePython)
  n = 9
  ref = H_element
FEATURE [App::DocumentObjectGroupPython] N_element037  label="N_element : 016"  # scripted group (container) (typed FeaturePython)
  n = 1
  ref = N_element
FEATURE [App::DocumentObjectGroupPython] O_element084  label="O_element : 045"  # scripted group (container) (typed FeaturePython)
  n = 1
  ref = O_element
FEATURE [App::DocumentObjectGroupPython] G4_POLYVINYL_PYRROLIDONE  # scripted group (container) (typed FeaturePython)
  Dunit = g/cm3
  Dvalue = 1.25
  Group = -> [C_element095,H_element087,N_element037,O_element084]
  conduct = 2
  density = 1
  expand = 3
  formula = G4_POLYVINYL_PYRROLIDONE
  name = G4_POLYVINYL_PYRROLIDONE
  specific = 4
FEATURE [App::DocumentObjectGroupPython] K_element008  label="K_element : 1"  # scripted group (container) (typed FeaturePython)
  n = 1
  ref = K_element
FEATURE [App::DocumentObjectGroupPython] I_element006  label="I_element : 003"  # scripted group (container) (typed FeaturePython)
  n = 1
  ref = I_element
FEATURE [App::DocumentObjectGroupPython] G4_POTASSIUM_IODIDE  # scripted group (container) (typed FeaturePython)
  Dunit = g/cm3
  Dvalue = 3.13
  Group = -> [K_element008,I_element006]
  conduct = 2
  density = 1
  expand = 3
  formula = G4_POTASSIUM_IODIDE
  name = G4_POTASSIUM_IODIDE
  specific = 4
FEATURE [App::DocumentObjectGroupPython] K_element009  label="K_element : 2"  # scripted group (container) (typed FeaturePython)
  n = 2
  ref = K_element
FEATURE [App::DocumentObjectGroupPython] O_element085  label="O_element : 046"  # scripted group (container) (typed FeaturePython)
  n = 1
  ref = O_element
FEATURE [App::DocumentObjectGroupPython] G4_POTASSIUM_OXIDE  # scripted group (container) (typed FeaturePython)
  Dunit = g/cm3
  Dvalue = 2.32
  Group = -> [K_element009,O_element085]
  conduct = 2
  density = 1
  expand = 3
  formula = G4_POTASSIUM_OXIDE
  name = G4_POTASSIUM_OXIDE
  specific = 4
FEATURE [App::DocumentObjectGroupPython] C_element096  label="C_element : 054"  # scripted group (container) (typed FeaturePython)
  n = 3
  ref = C_element
FEATURE [App::DocumentObjectGroupPython] H_element088  label="H_element : 049"  # scripted group (container) (typed FeaturePython)
  n = 8
  ref = H_element
FEATURE [App::DocumentObjectGroupPython] G4_PROPANE  # scripted group (container) (typed FeaturePython)
  Dunit = g/cm3
  Dvalue = 0.00187939
  Group = -> [C_element096,H_element088]
  conduct = 2
  density = 1
  expand = 3
  formula = G4_PROPANE
  name = G4_PROPANE
  specific = 4
FEATURE [App::DocumentObjectGroupPython] C_element097  label="C_element : 055"  # scripted group (container) (typed FeaturePython)
  n = 3
  ref = C_element
FEATURE [App::DocumentObjectGroupPython] H_element089  label="H_element : 050"  # scripted group (container) (typed FeaturePython)
  n = 8
  ref = H_element
FEATURE [App::DocumentObjectGroupPython] G4_lPROPANE  # scripted group (container) (typed FeaturePython)
  Dunit = g/cm3
  Dvalue = 0.43
  Group = -> [C_element097,H_element089]
  conduct = 2
  density = 1
  expand = 3
  formula = G4_lPROPANE
  name = G4_lPROPANE
  specific = 4
FEATURE [App::DocumentObjectGroupPython] C_element098  label="C_element : 056"  # scripted group (container) (typed FeaturePython)
  n = 3
  ref = C_element
FEATURE [App::DocumentObjectGroupPython] H_element090  label="H_element : 051"  # scripted group (container) (typed FeaturePython)
  n = 8
  ref = H_element
FEATURE [App::DocumentObjectGroupPython] O_element086  label="O_element : 047"  # scripted group (container) (typed FeaturePython)
  n = 1
  ref = O_element
FEATURE [App::DocumentObjectGroupPython] G4_N_PROPYL_ALCOHOL  label="G4_N-PROPYL_ALCOHOL"  # scripted group (container) (typed FeaturePython)
  Dunit = g/cm3
  Dvalue = 0.8035
  Group = -> [C_element098,H_element090,O_element086]
  conduct = 2
  density = 1
  expand = 3
  formula = G4_N-PROPYL_ALCOHOL
  name = G4_N-PROPYL_ALCOHOL
  specific = 4
FEATURE [App::DocumentObjectGroupPython] C_element099  label="C_element : 057"  # scripted group (container) (typed FeaturePython)
  n = 5
  ref = C_element
FEATURE [App::DocumentObjectGroupPython] H_element091  label="H_element : 052"  # scripted group (container) (typed FeaturePython)
  n = 5
  ref = H_element
FEATURE [App::DocumentObjectGroupPython] N_element038  label="N_element : 017"  # scripted group (container) (typed FeaturePython)
  n = 1
  ref = N_element
FEATURE [App::DocumentObjectGroupPython] G4_PYRIDINE  # scripted group (container) (typed FeaturePython)
  Dunit = g/cm3
  Dvalue = 0.9819
  Group = -> [C_element099,H_element091,N_element038]
  conduct = 2
  density = 1
  expand = 3
  formula = G4_PYRIDINE
  name = G4_PYRIDINE
  specific = 4
FEATURE [App::DocumentObjectGroupPython] H_element092  label="H_element : 0.144"  # scripted group (container) (typed FeaturePython)
  n = 0.143711
FEATURE [App::DocumentObjectGroupPython] C_element100  label="C_element : 0.856"  # scripted group (container) (typed FeaturePython)
  n = 0.856289
FEATURE [App::DocumentObjectGroupPython] G4_RUBBER_BUTYL  # scripted group (container) (typed FeaturePython)
  Dunit = g/cm3
  Dvalue = 0.92
  Group = -> [H_element092,C_element100]
  conduct = 2
  density = 1
  expand = 3
  formula = G4_RUBBER_BUTYL
  name = G4_RUBBER_BUTYL
  specific = 4
FEATURE [App::DocumentObjectGroupPython] H_element093  label="H_element : 0.118"  # scripted group (container) (typed FeaturePython)
  n = 0.118371
FEATURE [App::DocumentObjectGroupPython] C_element101  label="C_element : 0.882"  # scripted group (container) (typed FeaturePython)
  n = 0.881629
FEATURE [App::DocumentObjectGroupPython] G4_RUBBER_NATURAL  # scripted group (container) (typed FeaturePython)
  Dunit = g/cm3
  Dvalue = 0.92
  Group = -> [H_element093,C_element101]
  conduct = 2
  density = 1
  expand = 3
  formula = G4_RUBBER_NATURAL
  name = G4_RUBBER_NATURAL
  specific = 4
FEATURE [App::DocumentObjectGroupPython] H_element094  label="H_element : 0.145"  # scripted group (container) (typed FeaturePython)
  n = 0.05692
FEATURE [App::DocumentObjectGroupPython] C_element102  label="C_element : 0.543"  # scripted group (container) (typed FeaturePython)
  n = 0.542646
FEATURE [App::DocumentObjectGroupPython] Cl_element021  label="Cl_element : 0.400"  # scripted group (container) (typed FeaturePython)
  n = 0.400434
FEATURE [App::DocumentObjectGroupPython] G4_RUBBER_NEOPRENE  # scripted group (container) (typed FeaturePython)
  Dunit = g/cm3
  Dvalue = 1.23
  Group = -> [H_element094,C_element102,Cl_element021]
  conduct = 2
  density = 1
  expand = 3
  formula = G4_RUBBER_NEOPRENE
  name = G4_RUBBER_NEOPRENE
  specific = 4
FEATURE [App::DocumentObjectGroupPython] Si_element006  label="Si_element : 1"  # scripted group (container) (typed FeaturePython)
  n = 1
  ref = Si_element
FEATURE [App::DocumentObjectGroupPython] O_element087  label="O_element : 048"  # scripted group (container) (typed FeaturePython)
  n = 2
  ref = O_element
FEATURE [App::DocumentObjectGroupPython] G4_SILICON_DIOXIDE  # scripted group (container) (typed FeaturePython)
  Dunit = g/cm3
  Dvalue = 2.32
  Group = -> [Si_element006,O_element087]
  conduct = 2
  density = 1
  expand = 3
  formula = G4_SILICON_DIOXIDE
  name = G4_SILICON_DIOXIDE
  specific = 4
FEATURE [App::DocumentObjectGroupPython] Ag_element002  label="Ag_element : 1"  # scripted group (container) (typed FeaturePython)
  n = 1
  ref = Ag_element
FEATURE [App::DocumentObjectGroupPython] Br_element005  label="Br_element : 003"  # scripted group (container) (typed FeaturePython)
  n = 1
  ref = Br_element
FEATURE [App::DocumentObjectGroupPython] G4_SILVER_BROMIDE  # scripted group (container) (typed FeaturePython)
  Dunit = g/cm3
  Dvalue = 6.473
  Group = -> [Ag_element002,Br_element005]
  conduct = 2
  density = 1
  expand = 3
  formula = G4_SILVER_BROMIDE
  name = G4_SILVER_BROMIDE
  specific = 4
FEATURE [App::DocumentObjectGroupPython] Ag_element003  label="Ag_element : 002"  # scripted group (container) (typed FeaturePython)
  n = 1
  ref = Ag_element
FEATURE [App::DocumentObjectGroupPython] Cl_element022  label="Cl_element : 011"  # scripted group (container) (typed FeaturePython)
  n = 1
  ref = Cl_element
FEATURE [App::DocumentObjectGroupPython] G4_SILVER_CHLORIDE  # scripted group (container) (typed FeaturePython)
  Dunit = g/cm3
  Dvalue = 5.56
  Group = -> [Ag_element003,Cl_element022]
  conduct = 2
  density = 1
  expand = 3
  formula = G4_SILVER_CHLORIDE
  name = G4_SILVER_CHLORIDE
  specific = 4
FEATURE [App::DocumentObjectGroupPython] Br_element006  label="Br_element : 0.423"  # scripted group (container) (typed FeaturePython)
  n = 0.422895
FEATURE [App::DocumentObjectGroupPython] Ag_element004  label="Ag_element : 0.574"  # scripted group (container) (typed FeaturePython)
  n = 0.573748
FEATURE [App::DocumentObjectGroupPython] I_element007  label="I_element : 0.649"  # scripted group (container) (typed FeaturePython)
  n = 0.003357
FEATURE [App::DocumentObjectGroupPython] G4_SILVER_HALIDES  # scripted group (container) (typed FeaturePython)
  Dunit = g/cm3
  Dvalue = 6.47
  Group = -> [Br_element006,Ag_element004,I_element007]
  conduct = 2
  density = 1
  expand = 3
  formula = G4_SILVER_HALIDES
  name = G4_SILVER_HALIDES
  specific = 4
FEATURE [App::DocumentObjectGroupPython] Ag_element005  label="Ag_element : 003"  # scripted group (container) (typed FeaturePython)
  n = 1
  ref = Ag_element
FEATURE [App::DocumentObjectGroupPython] I_element008  label="I_element : 004"  # scripted group (container) (typed FeaturePython)
  n = 1
  ref = I_element
FEATURE [App::DocumentObjectGroupPython] G4_SILVER_IODIDE  # scripted group (container) (typed FeaturePython)
  Dunit = g/cm3
  Dvalue = 6.01
  Group = -> [Ag_element005,I_element008]
  conduct = 2
  density = 1
  expand = 3
  formula = G4_SILVER_IODIDE
  name = G4_SILVER_IODIDE
  specific = 4
FEATURE [App::DocumentObjectGroupPython] H_element095  label="H_element : 0.100"  # scripted group (container) (typed FeaturePython)
  n = 0.1
FEATURE [App::DocumentObjectGroupPython] C_element103  label="C_element : 0.204"  # scripted group (container) (typed FeaturePython)
  n = 0.204
FEATURE [App::DocumentObjectGroupPython] N_element039  label="N_element : 0.759"  # scripted group (container) (typed FeaturePython)
  n = 0.042
FEATURE [App::DocumentObjectGroupPython] O_element088  label="O_element : 0.645"  # scripted group (container) (typed FeaturePython)
  n = 0.645
FEATURE [App::DocumentObjectGroupPython] Na_element013  label="Na_element : 0.100"  # scripted group (container) (typed FeaturePython)
  n = 0.002
FEATURE [App::DocumentObjectGroupPython] P_element009  label="P_element : 0.107"  # scripted group (container) (typed FeaturePython)
  n = 0.001
FEATURE [App::DocumentObjectGroupPython] S_element020  label="S_element : 0.021"  # scripted group (container) (typed FeaturePython)
  n = 0.002
FEATURE [App::DocumentObjectGroupPython] Cl_element023  label="Cl_element : 0.590"  # scripted group (container) (typed FeaturePython)
  n = 0.003
FEATURE [App::DocumentObjectGroupPython] K_element010  label="K_element : 0.001"  # scripted group (container) (typed FeaturePython)
  n = 0.001
FEATURE [App::DocumentObjectGroupPython] G4_SKIN_ICRP  # scripted group (container) (typed FeaturePython)
  Dunit = g/cm3
  Dvalue = 1.09
  Group = -> [H_element095,C_element103,N_element039,O_element088,Na_element013,P_element009,S_element020,Cl_element023,K_element010]
  conduct = 2
  density = 1
  expand = 3
  formula = G4_SKIN_ICRP
  name = G4_SKIN_ICRP
  specific = 4
FEATURE [App::DocumentObjectGroupPython] Na_element014  label="Na_element : 2"  # scripted group (container) (typed FeaturePython)
  n = 2
  ref = Na_element
FEATURE [App::DocumentObjectGroupPython] C_element104  label="C_element : 058"  # scripted group (container) (typed FeaturePython)
  n = 1
  ref = C_element
FEATURE [App::DocumentObjectGroupPython] O_element089  label="O_element : 049"  # scripted group (container) (typed FeaturePython)
  n = 3
  ref = O_element
FEATURE [App::DocumentObjectGroupPython] G4_SODIUM_CARBONATE  # scripted group (container) (typed FeaturePython)
  Dunit = g/cm3
  Dvalue = 2.532
  Group = -> [Na_element014,C_element104,O_element089]
  conduct = 2
  density = 1
  expand = 3
  formula = G4_SODIUM_CARBONATE
  name = G4_SODIUM_CARBONATE
  specific = 4
FEATURE [App::DocumentObjectGroupPython] Na_element015  label="Na_element : 1"  # scripted group (container) (typed FeaturePython)
  n = 1
  ref = Na_element
FEATURE [App::DocumentObjectGroupPython] I_element009  label="I_element : 005"  # scripted group (container) (typed FeaturePython)
  n = 1
  ref = I_element
FEATURE [App::DocumentObjectGroupPython] G4_SODIUM_IODIDE  # scripted group (container) (typed FeaturePython)
  Dunit = g/cm3
  Dvalue = 3.667
  Group = -> [Na_element015,I_element009]
  conduct = 2
  density = 1
  expand = 3
  formula = G4_SODIUM_IODIDE
  name = G4_SODIUM_IODIDE
  specific = 4
FEATURE [App::DocumentObjectGroupPython] Na_element016  label="Na_element : 003"  # scripted group (container) (typed FeaturePython)
  n = 2
  ref = Na_element
FEATURE [App::DocumentObjectGroupPython] O_element090  label="O_element : 050"  # scripted group (container) (typed FeaturePython)
  n = 1
  ref = O_element
FEATURE [App::DocumentObjectGroupPython] G4_SODIUM_MONOXIDE  # scripted group (container) (typed FeaturePython)
  Dunit = g/cm3
  Dvalue = 2.27
  Group = -> [Na_element016,O_element090]
  conduct = 2
  density = 1
  expand = 3
  formula = G4_SODIUM_MONOXIDE
  name = G4_SODIUM_MONOXIDE
  specific = 4
FEATURE [App::DocumentObjectGroupPython] Na_element017  label="Na_element : 004"  # scripted group (container) (typed FeaturePython)
  n = 1
  ref = Na_element
FEATURE [App::DocumentObjectGroupPython] N_element040  label="N_element : 018"  # scripted group (container) (typed FeaturePython)
  n = 1
  ref = N_element
FEATURE [App::DocumentObjectGroupPython] O_element091  label="O_element : 051"  # scripted group (container) (typed FeaturePython)
  n = 3
  ref = O_element
FEATURE [App::DocumentObjectGroupPython] G4_SODIUM_NITRATE  # scripted group (container) (typed FeaturePython)
  Dunit = g/cm3
  Dvalue = 2.261
  Group = -> [Na_element017,N_element040,O_element091]
  conduct = 2
  density = 1
  expand = 3
  formula = G4_SODIUM_NITRATE
  name = G4_SODIUM_NITRATE
  specific = 4
FEATURE [App::DocumentObjectGroupPython] C_element105  label="C_element : 059"  # scripted group (container) (typed FeaturePython)
  n = 14
  ref = C_element
FEATURE [App::DocumentObjectGroupPython] H_element096  label="H_element : 053"  # scripted group (container) (typed FeaturePython)
  n = 12
  ref = H_element
FEATURE [App::DocumentObjectGroupPython] G4_STILBENE  # scripted group (container) (typed FeaturePython)
  Dunit = g/cm3
  Dvalue = 0.9707
  Group = -> [C_element105,H_element096]
  conduct = 2
  density = 1
  expand = 3
  formula = G4_STILBENE
  name = G4_STILBENE
  specific = 4
FEATURE [App::DocumentObjectGroupPython] C_element106  label="C_element : 12"  # scripted group (container) (typed FeaturePython)
  n = 12
  ref = C_element
FEATURE [App::DocumentObjectGroupPython] H_element097  label="H_element : 22"  # scripted group (container) (typed FeaturePython)
  n = 22
  ref = H_element
FEATURE [App::DocumentObjectGroupPython] O_element092  label="O_element : 11"  # scripted group (container) (typed FeaturePython)
  n = 11
  ref = O_element
FEATURE [App::DocumentObjectGroupPython] G4_SUCROSE  # scripted group (container) (typed FeaturePython)
  Dunit = g/cm3
  Dvalue = 1.5805
  Group = -> [C_element106,H_element097,O_element092]
  conduct = 2
  density = 1
  expand = 3
  formula = G4_SUCROSE
  name = G4_SUCROSE
  specific = 4
FEATURE [App::DocumentObjectGroupPython] C_element107  label="C_element : 18"  # scripted group (container) (typed FeaturePython)
  n = 18
  ref = C_element
FEATURE [App::DocumentObjectGroupPython] H_element098  label="H_element : 054"  # scripted group (container) (typed FeaturePython)
  n = 14
  ref = H_element
FEATURE [App::DocumentObjectGroupPython] G4_TERPHENYL  # scripted group (container) (typed FeaturePython)
  Dunit = g/cm3
  Dvalue = 1.24
  Group = -> [C_element107,H_element098]
  conduct = 2
  density = 1
  expand = 3
  formula = G4_TERPHENYL
  name = G4_TERPHENYL
  specific = 4
FEATURE [App::DocumentObjectGroupPython] H_element099  label="H_element : 0.146"  # scripted group (container) (typed FeaturePython)
  n = 0.106
FEATURE [App::DocumentObjectGroupPython] C_element108  label="C_element : 0.883"  # scripted group (container) (typed FeaturePython)
  n = 0.099
FEATURE [App::DocumentObjectGroupPython] N_element041  label="N_element : 0.020"  # scripted group (container) (typed FeaturePython)
  n = 0.02
FEATURE [App::DocumentObjectGroupPython] O_element093  label="O_element : 0.766"  # scripted group (container) (typed FeaturePython)
  n = 0.766
FEATURE [App::DocumentObjectGroupPython] Na_element018  label="Na_element : 0.101"  # scripted group (container) (typed FeaturePython)
  n = 0.002
FEATURE [App::DocumentObjectGroupPython] P_element010  label="P_element : 0.108"  # scripted group (container) (typed FeaturePython)
  n = 0.001
FEATURE [App::DocumentObjectGroupPython] S_element021  label="S_element : 0.022"  # scripted group (container) (typed FeaturePython)
  n = 0.002
FEATURE [App::DocumentObjectGroupPython] Cl_element024  label="Cl_element : 0.002"  # scripted group (container) (typed FeaturePython)
  n = 0.002
FEATURE [App::DocumentObjectGroupPython] K_element011  label="K_element : 0.017"  # scripted group (container) (typed FeaturePython)
  n = 0.002
FEATURE [App::DocumentObjectGroupPython] G4_TESTIS_ICRP  # scripted group (container) (typed FeaturePython)
  Dunit = g/cm3
  Dvalue = 1.04
  Group = -> [H_element099,C_element108,N_element041,O_element093,Na_element018,P_element010,S_element021,Cl_element024,K_element011]
  conduct = 2
  density = 1
  expand = 3
  formula = G4_TESTIS_ICRP
  name = G4_TESTIS_ICRP
  specific = 4
FEATURE [App::DocumentObjectGroupPython] C_element109  label="C_element : 060"  # scripted group (container) (typed FeaturePython)
  n = 2
  ref = C_element
FEATURE [App::DocumentObjectGroupPython] Cl_element025  label="Cl_element : 012"  # scripted group (container) (typed FeaturePython)
  n = 4
  ref = Cl_element
FEATURE [App::DocumentObjectGroupPython] G4_TETRACHLOROETHYLENE  # scripted group (container) (typed FeaturePython)
  Dunit = g/cm3
  Dvalue = 1.625
  Group = -> [C_element109,Cl_element025]
  conduct = 2
  density = 1
  expand = 3
  formula = G4_TETRACHLOROETHYLENE
  name = G4_TETRACHLOROETHYLENE
  specific = 4
FEATURE [App::DocumentObjectGroupPython] Tl_element001  label="Tl_element : 1"  # scripted group (container) (typed FeaturePython)
  n = 1
  ref = Tl_element
FEATURE [App::DocumentObjectGroupPython] Cl_element026  label="Cl_element : 013"  # scripted group (container) (typed FeaturePython)
  n = 1
  ref = Cl_element
FEATURE [App::DocumentObjectGroupPython] G4_THALLIUM_CHLORIDE  # scripted group (container) (typed FeaturePython)
  Dunit = g/cm3
  Dvalue = 7.004
  Group = -> [Tl_element001,Cl_element026]
  conduct = 2
  density = 1
  expand = 3
  formula = G4_THALLIUM_CHLORIDE
  name = G4_THALLIUM_CHLORIDE
  specific = 4
FEATURE [App::DocumentObjectGroupPython] H_element100  label="H_element : 0.147"  # scripted group (container) (typed FeaturePython)
  n = 0.105
FEATURE [App::DocumentObjectGroupPython] C_element110  label="C_element : 0.256"  # scripted group (container) (typed FeaturePython)
  n = 0.256
FEATURE [App::DocumentObjectGroupPython] N_element042  label="N_element : 0.760"  # scripted group (container) (typed FeaturePython)
  n = 0.027
FEATURE [App::DocumentObjectGroupPython] O_element094  label="O_element : 0.602"  # scripted group (container) (typed FeaturePython)
  n = 0.602
FEATURE [App::DocumentObjectGroupPython] Na_element019  label="Na_element : 0.102"  # scripted group (container) (typed FeaturePython)
  n = 0.001
FEATURE [App::DocumentObjectGroupPython] P_element011  label="P_element : 0.109"  # scripted group (container) (typed FeaturePython)
  n = 0.002
FEATURE [App::DocumentObjectGroupPython] S_element022  label="S_element : 0.023"  # scripted group (container) (typed FeaturePython)
  n = 0.003
FEATURE [App::DocumentObjectGroupPython] Cl_element027  label="Cl_element : 0.591"  # scripted group (container) (typed FeaturePython)
  n = 0.002
FEATURE [App::DocumentObjectGroupPython] K_element012  label="K_element : 0.018"  # scripted group (container) (typed FeaturePython)
  n = 0.002
FEATURE [App::DocumentObjectGroupPython] G4_TISSUE_SOFT_ICRP  # scripted group (container) (typed FeaturePython)
  Dunit = g/cm3
  Dvalue = 1.03
  Group = -> [H_element100,C_element110,N_element042,O_element094,Na_element019,P_element011,S_element022,Cl_element027,K_element012]
  conduct = 2
  density = 1
  expand = 3
  formula = G4_TISSUE_SOFT_ICRP
  name = G4_TISSUE_SOFT_ICRP
  specific = 4
FEATURE [App::DocumentObjectGroupPython] H_element101  label="H_element : 0.148"  # scripted group (container) (typed FeaturePython)
  n = 0.101
FEATURE [App::DocumentObjectGroupPython] C_element111  label="C_element : 0.111"  # scripted group (container) (typed FeaturePython)
  n = 0.111
FEATURE [App::DocumentObjectGroupPython] N_element043  label="N_element : 0.026"  # scripted group (container) (typed FeaturePython)
  n = 0.026
FEATURE [App::DocumentObjectGroupPython] O_element095  label="O_element : 0.762"  # scripted group (container) (typed FeaturePython)
  n = 0.762
FEATURE [App::DocumentObjectGroupPython] G4_TISSUE_SOFT_ICRU_4  label="G4_TISSUE_SOFT_ICRU-4"  # scripted group (container) (typed FeaturePython)
  Dunit = g/cm3
  Dvalue = 1
  Group = -> [H_element101,C_element111,N_element043,O_element095]
  conduct = 2
  density = 1
  expand = 3
  formula = G4_TISSUE_SOFT_ICRU-4
  name = G4_TISSUE_SOFT_ICRU-4
  specific = 4
FEATURE [App::DocumentObjectGroupPython] H_element102  label="H_element : 0.149"  # scripted group (container) (typed FeaturePython)
  n = 0.101869
FEATURE [App::DocumentObjectGroupPython] C_element112  label="C_element : 0.456"  # scripted group (container) (typed FeaturePython)
  n = 0.456179
FEATURE [App::DocumentObjectGroupPython] N_element044  label="N_element : 0.761"  # scripted group (container) (typed FeaturePython)
  n = 0.035172
FEATURE [App::DocumentObjectGroupPython] O_element096  label="O_element : 0.407"  # scripted group (container) (typed FeaturePython)
  n = 0.40678
FEATURE [App::DocumentObjectGroupPython] G4_TISSUE_METHANE  label="G4_TISSUE-METHANE"  # scripted group (container) (typed FeaturePython)
  Dunit = g/cm3
  Dvalue = 0.00106409
  Group = -> [H_element102,C_element112,N_element044,O_element096]
  conduct = 2
  density = 1
  expand = 3
  formula = G4_TISSUE-METHANE
  name = G4_TISSUE-METHANE
  specific = 4
FEATURE [App::DocumentObjectGroupPython] H_element103  label="H_element : 0.103"  # scripted group (container) (typed FeaturePython)
  n = 0.102672
FEATURE [App::DocumentObjectGroupPython] C_element113  label="C_element : 0.569"  # scripted group (container) (typed FeaturePython)
  n = 0.56894
FEATURE [App::DocumentObjectGroupPython] N_element045  label="N_element : 0.762"  # scripted group (container) (typed FeaturePython)
  n = 0.035022
FEATURE [App::DocumentObjectGroupPython] O_element097  label="O_element : 0.293"  # scripted group (container) (typed FeaturePython)
  n = 0.293366
FEATURE [App::DocumentObjectGroupPython] G4_TISSUE_PROPANE  label="G4_TISSUE-PROPANE"  # scripted group (container) (typed FeaturePython)
  Dunit = g/cm3
  Dvalue = 0.00182628
  Group = -> [H_element103,C_element113,N_element045,O_element097]
  conduct = 2
  density = 1
  expand = 3
  formula = G4_TISSUE-PROPANE
  name = G4_TISSUE-PROPANE
  specific = 4
FEATURE [App::DocumentObjectGroupPython] Ti_element003  label="Ti_element : 1"  # scripted group (container) (typed FeaturePython)
  n = 1
  ref = Ti_element
FEATURE [App::DocumentObjectGroupPython] O_element098  label="O_element : 052"  # scripted group (container) (typed FeaturePython)
  n = 2
  ref = O_element
FEATURE [App::DocumentObjectGroupPython] G4_TITANIUM_DIOXIDE  # scripted group (container) (typed FeaturePython)
  Dunit = g/cm3
  Dvalue = 4.26
  Group = -> [Ti_element003,O_element098]
  conduct = 2
  density = 1
  expand = 3
  formula = G4_TITANIUM_DIOXIDE
  name = G4_TITANIUM_DIOXIDE
  specific = 4
FEATURE [App::DocumentObjectGroupPython] C_element114  label="C_element : 061"  # scripted group (container) (typed FeaturePython)
  n = 7
  ref = C_element
FEATURE [App::DocumentObjectGroupPython] H_element104  label="H_element : 055"  # scripted group (container) (typed FeaturePython)
  n = 8
  ref = H_element
FEATURE [App::DocumentObjectGroupPython] G4_TOLUENE  # scripted group (container) (typed FeaturePython)
  Dunit = g/cm3
  Dvalue = 0.8669
  Group = -> [C_element114,H_element104]
  conduct = 2
  density = 1
  expand = 3
  formula = G4_TOLUENE
  name = G4_TOLUENE
  specific = 4
FEATURE [App::DocumentObjectGroupPython] C_element115  label="C_element : 062"  # scripted group (container) (typed FeaturePython)
  n = 2
  ref = C_element
FEATURE [App::DocumentObjectGroupPython] H_element105  label="H_element : 056"  # scripted group (container) (typed FeaturePython)
  n = 1
  ref = H_element
FEATURE [App::DocumentObjectGroupPython] Cl_element028  label="Cl_element : 014"  # scripted group (container) (typed FeaturePython)
  n = 3
  ref = Cl_element
FEATURE [App::DocumentObjectGroupPython] G4_TRICHLOROETHYLENE  # scripted group (container) (typed FeaturePython)
  Dunit = g/cm3
  Dvalue = 1.46
  Group = -> [C_element115,H_element105,Cl_element028]
  conduct = 2
  density = 1
  expand = 3
  formula = G4_TRICHLOROETHYLENE
  name = G4_TRICHLOROETHYLENE
  specific = 4
FEATURE [App::DocumentObjectGroupPython] C_element116  label="C_element : 063"  # scripted group (container) (typed FeaturePython)
  n = 6
  ref = C_element
FEATURE [App::DocumentObjectGroupPython] H_element106  label="H_element : 15"  # scripted group (container) (typed FeaturePython)
  n = 15
  ref = H_element
FEATURE [App::DocumentObjectGroupPython] O_element099  label="O_element : 053"  # scripted group (container) (typed FeaturePython)
  n = 4
  ref = O_element
FEATURE [App::DocumentObjectGroupPython] P_element012  label="P_element : 1"  # scripted group (container) (typed FeaturePython)
  n = 1
  ref = P_element
FEATURE [App::DocumentObjectGroupPython] G4_TRIETHYL_PHOSPHATE  # scripted group (container) (typed FeaturePython)
  Dunit = g/cm3
  Dvalue = 1.07
  Group = -> [C_element116,H_element106,O_element099,P_element012]
  conduct = 2
  density = 1
  expand = 3
  formula = G4_TRIETHYL_PHOSPHATE
  name = G4_TRIETHYL_PHOSPHATE
  specific = 4
FEATURE [App::DocumentObjectGroupPython] W_element003  label="W_element : 003"  # scripted group (container) (typed FeaturePython)
  n = 1
  ref = W_element
FEATURE [App::DocumentObjectGroupPython] F_element017  label="F_element : 6"  # scripted group (container) (typed FeaturePython)
  n = 6
  ref = F_element
FEATURE [App::DocumentObjectGroupPython] G4_TUNGSTEN_HEXAFLUORIDE  # scripted group (container) (typed FeaturePython)
  Dunit = g/cm3
  Dvalue = 2.4
  Group = -> [W_element003,F_element017]
  conduct = 2
  density = 1
  expand = 3
  formula = G4_TUNGSTEN_HEXAFLUORIDE
  name = G4_TUNGSTEN_HEXAFLUORIDE
  specific = 4
FEATURE [App::DocumentObjectGroupPython] U_element001  label="U_element : 1"  # scripted group (container) (typed FeaturePython)
  n = 1
  ref = U_element
FEATURE [App::DocumentObjectGroupPython] C_element117  label="C_element : 064"  # scripted group (container) (typed FeaturePython)
  n = 2
  ref = C_element
FEATURE [App::DocumentObjectGroupPython] G4_URANIUM_DICARBIDE  # scripted group (container) (typed FeaturePython)
  Dunit = g/cm3
  Dvalue = 11.28
  Group = -> [U_element001,C_element117]
  conduct = 2
  density = 1
  expand = 3
  formula = G4_URANIUM_DICARBIDE
  name = G4_URANIUM_DICARBIDE
  specific = 4
FEATURE [App::DocumentObjectGroupPython] U_element002  label="U_element : 002"  # scripted group (container) (typed FeaturePython)
  n = 1
  ref = U_element
FEATURE [App::DocumentObjectGroupPython] C_element118  label="C_element : 065"  # scripted group (container) (typed FeaturePython)
  n = 1
  ref = C_element
FEATURE [App::DocumentObjectGroupPython] G4_URANIUM_MONOCARBIDE  # scripted group (container) (typed FeaturePython)
  Dunit = g/cm3
  Dvalue = 13.63
  Group = -> [U_element002,C_element118]
  conduct = 2
  density = 1
  expand = 3
  formula = G4_URANIUM_MONOCARBIDE
  name = G4_URANIUM_MONOCARBIDE
  specific = 4
FEATURE [App::DocumentObjectGroupPython] U_element003  label="U_element : 003"  # scripted group (container) (typed FeaturePython)
  n = 1
  ref = U_element
FEATURE [App::DocumentObjectGroupPython] O_element100  label="O_element : 054"  # scripted group (container) (typed FeaturePython)
  n = 2
  ref = O_element
FEATURE [App::DocumentObjectGroupPython] G4_URANIUM_OXIDE  # scripted group (container) (typed FeaturePython)
  Dunit = g/cm3
  Dvalue = 10.96
  Group = -> [U_element003,O_element100]
  conduct = 2
  density = 1
  expand = 3
  formula = G4_URANIUM_OXIDE
  name = G4_URANIUM_OXIDE
  specific = 4
FEATURE [App::DocumentObjectGroupPython] C_element119  label="C_element : 066"  # scripted group (container) (typed FeaturePython)
  n = 1
  ref = C_element
FEATURE [App::DocumentObjectGroupPython] H_element107  label="H_element : 057"  # scripted group (container) (typed FeaturePython)
  n = 4
  ref = H_element
FEATURE [App::DocumentObjectGroupPython] N_element046  label="N_element : 019"  # scripted group (container) (typed FeaturePython)
  n = 2
  ref = N_element
FEATURE [App::DocumentObjectGroupPython] O_element101  label="O_element : 055"  # scripted group (container) (typed FeaturePython)
  n = 1
  ref = O_element
FEATURE [App::DocumentObjectGroupPython] G4_UREA  # scripted group (container) (typed FeaturePython)
  Dunit = g/cm3
  Dvalue = 1.323
  Group = -> [C_element119,H_element107,N_element046,O_element101]
  conduct = 2
  density = 1
  expand = 3
  formula = G4_UREA
  name = G4_UREA
  specific = 4
FEATURE [App::DocumentObjectGroupPython] C_element120  label="C_element : 067"  # scripted group (container) (typed FeaturePython)
  n = 5
  ref = C_element
FEATURE [App::DocumentObjectGroupPython] H_element108  label="H_element : 058"  # scripted group (container) (typed FeaturePython)
  n = 11
  ref = H_element
FEATURE [App::DocumentObjectGroupPython] N_element047  label="N_element : 020"  # scripted group (container) (typed FeaturePython)
  n = 1
  ref = N_element
FEATURE [App::DocumentObjectGroupPython] O_element102  label="O_element : 056"  # scripted group (container) (typed FeaturePython)
  n = 2
  ref = O_element
FEATURE [App::DocumentObjectGroupPython] G4_VALINE  # scripted group (container) (typed FeaturePython)
  Dunit = g/cm3
  Dvalue = 1.23
  Group = -> [C_element120,H_element108,N_element047,O_element102]
  conduct = 2
  density = 1
  expand = 3
  formula = G4_VALINE
  name = G4_VALINE
  specific = 4
FEATURE [App::DocumentObjectGroupPython] H_element109  label="H_element : 0.009"  # scripted group (container) (typed FeaturePython)
  n = 0.009417
FEATURE [App::DocumentObjectGroupPython] C_element121  label="C_element : 0.281"  # scripted group (container) (typed FeaturePython)
  n = 0.280555
FEATURE [App::DocumentObjectGroupPython] F_element018  label="F_element : 0.710"  # scripted group (container) (typed FeaturePython)
  n = 0.710028
FEATURE [App::DocumentObjectGroupPython] G4_VITON  # scripted group (container) (typed FeaturePython)
  Dunit = g/cm3
  Dvalue = 1.8
  Group = -> [H_element109,C_element121,F_element018]
  conduct = 2
  density = 1
  expand = 3
  formula = G4_VITON
  name = G4_VITON
  specific = 4
FEATURE [App::DocumentObjectGroupPython] H_element110  label="H_element : 059"  # scripted group (container) (typed FeaturePython)
  n = 2
  ref = H_element
FEATURE [App::DocumentObjectGroupPython] O_element103  label="O_element : 057"  # scripted group (container) (typed FeaturePython)
  n = 1
  ref = O_element
FEATURE [App::DocumentObjectGroupPython] G4_WATER  # scripted group (container) (typed FeaturePython)
  Dunit = g/cm3
  Dvalue = 1
  Group = -> [H_element110,O_element103]
  conduct = 2
  density = 1
  expand = 3
  formula = G4_WATER
  name = G4_WATER
  specific = 4
FEATURE [App::DocumentObjectGroupPython] H_element111  label="H_element : 060"  # scripted group (container) (typed FeaturePython)
  n = 2
  ref = H_element
FEATURE [App::DocumentObjectGroupPython] O_element104  label="O_element : 058"  # scripted group (container) (typed FeaturePython)
  n = 1
  ref = O_element
FEATURE [App::DocumentObjectGroupPython] G4_WATER_VAPOR  # scripted group (container) (typed FeaturePython)
  Dunit = g/cm3
  Dvalue = 0.000756182
  Group = -> [H_element111,O_element104]
  conduct = 2
  density = 1
  expand = 3
  formula = G4_WATER_VAPOR
  name = G4_WATER_VAPOR
  specific = 4
FEATURE [App::DocumentObjectGroupPython] C_element122  label="C_element : 068"  # scripted group (container) (typed FeaturePython)
  n = 8
  ref = C_element
FEATURE [App::DocumentObjectGroupPython] H_element112  label="H_element : 061"  # scripted group (container) (typed FeaturePython)
  n = 10
  ref = H_element
FEATURE [App::DocumentObjectGroupPython] G4_XYLENE  # scripted group (container) (typed FeaturePython)
  Dunit = g/cm3
  Dvalue = 0.87
  Group = -> [C_element122,H_element112]
  conduct = 2
  density = 1
  expand = 3
  formula = G4_XYLENE
  name = G4_XYLENE
  specific = 4
FEATURE [App::DocumentObjectGroupPython] C_element123  label="C_element : 069"  # scripted group (container) (typed FeaturePython)
  n = 1
  ref = C_element
FEATURE [App::DocumentObjectGroupPython] G4_GRAPHITE  # scripted group (container) (typed FeaturePython)
  Dunit = g/cm3
  Dvalue = 2.21
  Group = -> [C_element123]
  conduct = 2
  density = 1
  expand = 3
  formula = G4_GRAPHITE
  name = G4_GRAPHITE
  specific = 4
FEATURE [App::DocumentObjectGroupPython] NIST  # scripted group (container) (typed FeaturePython)
  Group = -> [G4_A_150_TISSUE,G4_ACETONE,G4_ACETYLENE,G4_ADENINE,G4_ADIPOSE_TISSUE_ICRP,G4_AIR,G4_ALANINE,G4_ALUMINUM_OXIDE,G4_AMBER,G4_AMMONIA,G4_ANILINE,G4_ANTHRACENE,G4_B_100_BONE,G4_BAKELITE,G4_BARIUM_FLUORIDE,G4_BARIUM_SULFATE,G4_BENZENE,G4_BERYLLIUM_OXIDE,G4_BGO,G4_BLOOD_ICRP,G4_BONE_COMPACT_ICRU,G4_BONE_CORTICAL_ICRP,G4_BORON_CARBIDE,G4_BORON_OXIDE,G4_BRAIN_ICRP,G4_BUTANE,G4_N_BUTYL_ALCOHOL,G4_C_552,+152 more]
FEATURE [App::DocumentObjectGroupPython] H_element113  label="H_element : 062"  # scripted group (container) (typed FeaturePython)
  n = 1
  ref = H_element
FEATURE [App::DocumentObjectGroupPython] G4_H  # scripted group (container) (typed FeaturePython)
  Dunit = g/cm3
  Dvalue = 8.3748e-05
  Group = -> [H_element113]
  conduct = 2
  density = 1
  expand = 3
  formula = H
  name = G4_H
  specific = 4
FEATURE [App::DocumentObjectGroupPython] He_element001  label="He_element : 1"  # scripted group (container) (typed FeaturePython)
  n = 1
  ref = He_element
FEATURE [App::DocumentObjectGroupPython] G4_He  # scripted group (container) (typed FeaturePython)
  Dunit = g/cm3
  Dvalue = 0.000166322
  Group = -> [He_element001]
  conduct = 2
  density = 1
  expand = 3
  formula = He
  name = G4_He
  specific = 4
FEATURE [App::DocumentObjectGroupPython] Li_element008  label="Li_element : 008"  # scripted group (container) (typed FeaturePython)
  n = 1
  ref = Li_element
FEATURE [App::DocumentObjectGroupPython] G4_Li  # scripted group (container) (typed FeaturePython)
  Dunit = g/cm3
  Dvalue = 0.534
  Group = -> [Li_element008]
  conduct = 2
  density = 1
  expand = 3
  formula = Li
  name = G4_Li
  specific = 4
FEATURE [App::DocumentObjectGroupPython] Be_element002  label="Be_element : 002"  # scripted group (container) (typed FeaturePython)
  n = 1
  ref = Be_element
FEATURE [App::DocumentObjectGroupPython] G4_Be  # scripted group (container) (typed FeaturePython)
  Dunit = g/cm3
  Dvalue = 1.848
  Group = -> [Be_element002]
  conduct = 2
  density = 1
  expand = 3
  formula = Be
  name = G4_Be
  specific = 4
FEATURE [App::DocumentObjectGroupPython] B_element007  label="B_element : 007"  # scripted group (container) (typed FeaturePython)
  n = 1
  ref = B_element
FEATURE [App::DocumentObjectGroupPython] G4_B  # scripted group (container) (typed FeaturePython)
  Dunit = g/cm3
  Dvalue = 2.37
  Group = -> [B_element007]
  conduct = 2
  density = 1
  expand = 3
  formula = B
  name = G4_B
  specific = 4
FEATURE [App::DocumentObjectGroupPython] C_element124  label="C_element : 070"  # scripted group (container) (typed FeaturePython)
  n = 1
  ref = C_element
FEATURE [App::DocumentObjectGroupPython] G4_C  # scripted group (container) (typed FeaturePython)
  Dunit = g/cm3
  Dvalue = 2
  Group = -> [C_element124]
  conduct = 2
  density = 1
  expand = 3
  formula = C
  name = G4_C
  specific = 4
FEATURE [App::DocumentObjectGroupPython] N_element048  label="N_element : 021"  # scripted group (container) (typed FeaturePython)
  n = 1
  ref = N_element
FEATURE [App::DocumentObjectGroupPython] G4_N  # scripted group (container) (typed FeaturePython)
  Dunit = g/cm3
  Dvalue = 0.0011652
  Group = -> [N_element048]
  conduct = 2
  density = 1
  expand = 3
  formula = N
  name = G4_N
  specific = 4
FEATURE [App::DocumentObjectGroupPython] O_element105  label="O_element : 059"  # scripted group (container) (typed FeaturePython)
  n = 1
  ref = O_element
FEATURE [App::DocumentObjectGroupPython] G4_O  # scripted group (container) (typed FeaturePython)
  Dunit = g/cm3
  Dvalue = 0.00133151
  Group = -> [O_element105]
  conduct = 2
  density = 1
  expand = 3
  formula = O
  name = G4_O
  specific = 4
FEATURE [App::DocumentObjectGroupPython] F_element019  label="F_element : 008"  # scripted group (container) (typed FeaturePython)
  n = 1
  ref = F_element
FEATURE [App::DocumentObjectGroupPython] G4_F  # scripted group (container) (typed FeaturePython)
  Dunit = g/cm3
  Dvalue = 0.00158029
  Group = -> [F_element019]
  conduct = 2
  density = 1
  expand = 3
  formula = F
  name = G4_F
  specific = 4
FEATURE [App::DocumentObjectGroupPython] Ne_element001  label="Ne_element : 1"  # scripted group (container) (typed FeaturePython)
  n = 1
  ref = Ne_element
FEATURE [App::DocumentObjectGroupPython] G4_Ne  # scripted group (container) (typed FeaturePython)
  Dunit = g/cm3
  Dvalue = 0.000838505
  Group = -> [Ne_element001]
  conduct = 2
  density = 1
  expand = 3
  formula = Ne
  name = G4_Ne
  specific = 4
FEATURE [App::DocumentObjectGroupPython] Na_element020  label="Na_element : 005"  # scripted group (container) (typed FeaturePython)
  n = 1
  ref = Na_element
FEATURE [App::DocumentObjectGroupPython] G4_Na  # scripted group (container) (typed FeaturePython)
  Dunit = g/cm3
  Dvalue = 0.971
  Group = -> [Na_element020]
  conduct = 2
  density = 1
  expand = 3
  formula = Na
  name = G4_Na
  specific = 4
FEATURE [App::DocumentObjectGroupPython] Mg_element011  label="Mg_element : 005"  # scripted group (container) (typed FeaturePython)
  n = 1
  ref = Mg_element
FEATURE [App::DocumentObjectGroupPython] G4_Mg  # scripted group (container) (typed FeaturePython)
  Dunit = g/cm3
  Dvalue = 1.74
  Group = -> [Mg_element011]
  conduct = 2
  density = 1
  expand = 3
  formula = Mg
  name = G4_Mg
  specific = 4
FEATURE [App::DocumentObjectGroupPython] Al_element004  label="Al_element : 1"  # scripted group (container) (typed FeaturePython)
  n = 1
  ref = Al_element
FEATURE [App::DocumentObjectGroupPython] G4_Al  # scripted group (container) (typed FeaturePython)
  Dunit = g/cm3
  Dvalue = 2.699
  Group = -> [Al_element004]
  conduct = 2
  density = 1
  expand = 3
  formula = Al
  name = G4_Al
  specific = 4
FEATURE [App::DocumentObjectGroupPython] Si_element007  label="Si_element : 002"  # scripted group (container) (typed FeaturePython)
  n = 1
  ref = Si_element
FEATURE [App::DocumentObjectGroupPython] G4_Si  # scripted group (container) (typed FeaturePython)
  Dunit = g/cm3
  Dvalue = 2.33
  Group = -> [Si_element007]
  conduct = 2
  density = 1
  expand = 3
  formula = Si
  name = G4_Si
  specific = 4
FEATURE [App::DocumentObjectGroupPython] P_element013  label="P_element : 002"  # scripted group (container) (typed FeaturePython)
  n = 1
  ref = P_element
FEATURE [App::DocumentObjectGroupPython] G4_P  # scripted group (container) (typed FeaturePython)
  Dunit = g/cm3
  Dvalue = 2.2
  Group = -> [P_element013]
  conduct = 2
  density = 1
  expand = 3
  formula = P
  name = G4_P
  specific = 4
FEATURE [App::DocumentObjectGroupPython] S_element023  label="S_element : 007"  # scripted group (container) (typed FeaturePython)
  n = 1
  ref = S_element
FEATURE [App::DocumentObjectGroupPython] G4_S  # scripted group (container) (typed FeaturePython)
  Dunit = g/cm3
  Dvalue = 2
  Group = -> [S_element023]
  conduct = 2
  density = 1
  expand = 3
  formula = S
  name = G4_S
  specific = 4
FEATURE [App::DocumentObjectGroupPython] Cl_element029  label="Cl_element : 015"  # scripted group (container) (typed FeaturePython)
  n = 1
  ref = Cl_element
FEATURE [App::DocumentObjectGroupPython] G4_Cl  # scripted group (container) (typed FeaturePython)
  Dunit = g/cm3
  Dvalue = 0.00299473
  Group = -> [Cl_element029]
  conduct = 2
  density = 1
  expand = 3
  formula = Cl
  name = G4_Cl
  specific = 4
FEATURE [App::DocumentObjectGroupPython] Ar_element002  label="Ar_element : 1"  # scripted group (container) (typed FeaturePython)
  n = 1
  ref = Ar_element
FEATURE [App::DocumentObjectGroupPython] G4_Ar  # scripted group (container) (typed FeaturePython)
  Dunit = g/cm3
  Dvalue = 0.00166201
  Group = -> [Ar_element002]
  conduct = 2
  density = 1
  expand = 3
  formula = Ar
  name = G4_Ar
  specific = 4
FEATURE [App::DocumentObjectGroupPython] K_element013  label="K_element : 003"  # scripted group (container) (typed FeaturePython)
  n = 1
  ref = K_element
FEATURE [App::DocumentObjectGroupPython] G4_K  # scripted group (container) (typed FeaturePython)
  Dunit = g/cm3
  Dvalue = 0.862
  Group = -> [K_element013]
  conduct = 2
  density = 1
  expand = 3
  formula = K
  name = G4_K
  specific = 4
FEATURE [App::DocumentObjectGroupPython] Ca_element014  label="Ca_element : 007"  # scripted group (container) (typed FeaturePython)
  n = 1
  ref = Ca_element
FEATURE [App::DocumentObjectGroupPython] G4_Ca  # scripted group (container) (typed FeaturePython)
  Dunit = g/cm3
  Dvalue = 1.55
  Group = -> [Ca_element014]
  conduct = 2
  density = 1
  expand = 3
  formula = Ca
  name = G4_Ca
  specific = 4
FEATURE [App::DocumentObjectGroupPython] Sc_element001  label="Sc_element : 1"  # scripted group (container) (typed FeaturePython)
  n = 1
  ref = Sc_element
FEATURE [App::DocumentObjectGroupPython] G4_Sc  # scripted group (container) (typed FeaturePython)
  Dunit = g/cm3
  Dvalue = 2.989
  Group = -> [Sc_element001]
  conduct = 2
  density = 1
  expand = 3
  formula = Sc
  name = G4_Sc
  specific = 4
FEATURE [App::DocumentObjectGroupPython] Ti_element004  label="Ti_element : 002"  # scripted group (container) (typed FeaturePython)
  n = 1
  ref = Ti_element
FEATURE [App::DocumentObjectGroupPython] G4_Ti  # scripted group (container) (typed FeaturePython)
  Dunit = g/cm3
  Dvalue = 4.54
  Group = -> [Ti_element004]
  conduct = 2
  density = 1
  expand = 3
  formula = Ti
  name = G4_Ti
  specific = 4
FEATURE [App::DocumentObjectGroupPython] V_element001  label="V_element : 1"  # scripted group (container) (typed FeaturePython)
  n = 1
  ref = V_element
FEATURE [App::DocumentObjectGroupPython] G4_V  # scripted group (container) (typed FeaturePython)
  Dunit = g/cm3
  Dvalue = 6.11
  Group = -> [V_element001]
  conduct = 2
  density = 1
  expand = 3
  formula = V
  name = G4_V
  specific = 4
FEATURE [App::DocumentObjectGroupPython] Cr_element001  label="Cr_element : 1"  # scripted group (container) (typed FeaturePython)
  n = 1
  ref = Cr_element
FEATURE [App::DocumentObjectGroupPython] G4_Cr  # scripted group (container) (typed FeaturePython)
  Dunit = g/cm3
  Dvalue = 7.18
  Group = -> [Cr_element001]
  conduct = 2
  density = 1
  expand = 3
  formula = Cr
  name = G4_Cr
  specific = 4
FEATURE [App::DocumentObjectGroupPython] Mn_element001  label="Mn_element : 1"  # scripted group (container) (typed FeaturePython)
  n = 1
  ref = Mn_element
FEATURE [App::DocumentObjectGroupPython] G4_Mn  # scripted group (container) (typed FeaturePython)
  Dunit = g/cm3
  Dvalue = 7.44
  Group = -> [Mn_element001]
  conduct = 2
  density = 1
  expand = 3
  formula = Mn
  name = G4_Mn
  specific = 4
FEATURE [App::DocumentObjectGroupPython] Fe_element007  label="Fe_element : 004"  # scripted group (container) (typed FeaturePython)
  n = 1
  ref = Fe_element
FEATURE [App::DocumentObjectGroupPython] G4_Fe  # scripted group (container) (typed FeaturePython)
  Dunit = g/cm3
  Dvalue = 7.874
  Group = -> [Fe_element007]
  conduct = 2
  density = 1
  expand = 3
  formula = Fe
  name = G4_Fe
  specific = 4
FEATURE [App::DocumentObjectGroupPython] Co_element001  label="Co_element : 1"  # scripted group (container) (typed FeaturePython)
  n = 1
  ref = Co_element
FEATURE [App::DocumentObjectGroupPython] G4_Co  # scripted group (container) (typed FeaturePython)
  Dunit = g/cm3
  Dvalue = 8.9
  Group = -> [Co_element001]
  conduct = 2
  density = 1
  expand = 3
  formula = Co
  name = G4_Co
  specific = 4
FEATURE [App::DocumentObjectGroupPython] Ni_element001  label="Ni_element : 1"  # scripted group (container) (typed FeaturePython)
  n = 1
  ref = Ni_element
FEATURE [App::DocumentObjectGroupPython] G4_Ni  # scripted group (container) (typed FeaturePython)
  Dunit = g/cm3
  Dvalue = 8.902
  Group = -> [Ni_element001]
  conduct = 2
  density = 1
  expand = 3
  formula = Ni
  name = G4_Ni
  specific = 4
FEATURE [App::DocumentObjectGroupPython] Cu_element001  label="Cu_element : 1"  # scripted group (container) (typed FeaturePython)
  n = 1
  ref = Cu_element
FEATURE [App::DocumentObjectGroupPython] G4_Cu  # scripted group (container) (typed FeaturePython)
  Dunit = g/cm3
  Dvalue = 8.96
  Group = -> [Cu_element001]
  conduct = 2
  density = 1
  expand = 3
  formula = Cu
  name = G4_Cu
  specific = 4
FEATURE [App::DocumentObjectGroupPython] Zn_element001  label="Zn_element : 1"  # scripted group (container) (typed FeaturePython)
  n = 1
  ref = Zn_element
FEATURE [App::DocumentObjectGroupPython] G4_Zn  # scripted group (container) (typed FeaturePython)
  Dunit = g/cm3
  Dvalue = 7.133
  Group = -> [Zn_element001]
  conduct = 2
  density = 1
  expand = 3
  formula = Zn
  name = G4_Zn
  specific = 4
FEATURE [App::DocumentObjectGroupPython] Ga_element002  label="Ga_element : 002"  # scripted group (container) (typed FeaturePython)
  n = 1
  ref = Ga_element
FEATURE [App::DocumentObjectGroupPython] G4_Ga  # scripted group (container) (typed FeaturePython)
  Dunit = g/cm3
  Dvalue = 5.904
  Group = -> [Ga_element002]
  conduct = 2
  density = 1
  expand = 3
  formula = Ga
  name = G4_Ga
  specific = 4
FEATURE [App::DocumentObjectGroupPython] Ge_element002  label="Ge_element : 1"  # scripted group (container) (typed FeaturePython)
  n = 1
  ref = Ge_element
FEATURE [App::DocumentObjectGroupPython] G4_Ge  # scripted group (container) (typed FeaturePython)
  Dunit = g/cm3
  Dvalue = 5.323
  Group = -> [Ge_element002]
  conduct = 2
  density = 1
  expand = 3
  formula = Ge
  name = G4_Ge
  specific = 4
FEATURE [App::DocumentObjectGroupPython] As_element003  label="As_element : 002"  # scripted group (container) (typed FeaturePython)
  n = 1
  ref = As_element
FEATURE [App::DocumentObjectGroupPython] G4_As  # scripted group (container) (typed FeaturePython)
  Dunit = g/cm3
  Dvalue = 5.73
  Group = -> [As_element003]
  conduct = 2
  density = 1
  expand = 3
  formula = As
  name = G4_As
  specific = 4
FEATURE [App::DocumentObjectGroupPython] Se_element001  label="Se_element : 1"  # scripted group (container) (typed FeaturePython)
  n = 1
  ref = Se_element
FEATURE [App::DocumentObjectGroupPython] G4_Se  # scripted group (container) (typed FeaturePython)
  Dunit = g/cm3
  Dvalue = 4.5
  Group = -> [Se_element001]
  conduct = 2
  density = 1
  expand = 3
  formula = Se
  name = G4_Se
  specific = 4
FEATURE [App::DocumentObjectGroupPython] Br_element007  label="Br_element : 004"  # scripted group (container) (typed FeaturePython)
  n = 1
  ref = Br_element
FEATURE [App::DocumentObjectGroupPython] G4_Br  # scripted group (container) (typed FeaturePython)
  Dunit = g/cm3
  Dvalue = 0.0070721
  Group = -> [Br_element007]
  conduct = 2
  density = 1
  expand = 3
  formula = Br
  name = G4_Br
  specific = 4
FEATURE [App::DocumentObjectGroupPython] Kr_element001  label="Kr_element : 1"  # scripted group (container) (typed FeaturePython)
  n = 1
  ref = Kr_element
FEATURE [App::DocumentObjectGroupPython] G4_Kr  # scripted group (container) (typed FeaturePython)
  Dunit = g/cm3
  Dvalue = 0.00347832
  Group = -> [Kr_element001]
  conduct = 2
  density = 1
  expand = 3
  formula = Kr
  name = G4_Kr
  specific = 4
FEATURE [App::DocumentObjectGroupPython] Rb_element001  label="Rb_element : 1"  # scripted group (container) (typed FeaturePython)
  n = 1
  ref = Rb_element
FEATURE [App::DocumentObjectGroupPython] G4_Rb  # scripted group (container) (typed FeaturePython)
  Dunit = g/cm3
  Dvalue = 1.532
  Group = -> [Rb_element001]
  conduct = 2
  density = 1
  expand = 3
  formula = Rb
  name = G4_Rb
  specific = 4
FEATURE [App::DocumentObjectGroupPython] Sr_element001  label="Sr_element : 1"  # scripted group (container) (typed FeaturePython)
  n = 1
  ref = Sr_element
FEATURE [App::DocumentObjectGroupPython] G4_Sr  # scripted group (container) (typed FeaturePython)
  Dunit = g/cm3
  Dvalue = 2.54
  Group = -> [Sr_element001]
  conduct = 2
  density = 1
  expand = 3
  formula = Sr
  name = G4_Sr
  specific = 4
FEATURE [App::DocumentObjectGroupPython] Y_element001  label="Y_element : 1"  # scripted group (container) (typed FeaturePython)
  n = 1
  ref = Y_element
FEATURE [App::DocumentObjectGroupPython] G4_Y  # scripted group (container) (typed FeaturePython)
  Dunit = g/cm3
  Dvalue = 4.469
  Group = -> [Y_element001]
  conduct = 2
  density = 1
  expand = 3
  formula = Y
  name = G4_Y
  specific = 4
FEATURE [App::DocumentObjectGroupPython] Zr_element001  label="Zr_element : 1"  # scripted group (container) (typed FeaturePython)
  n = 1
  ref = Zr_element
FEATURE [App::DocumentObjectGroupPython] G4_Zr  # scripted group (container) (typed FeaturePython)
  Dunit = g/cm3
  Dvalue = 6.506
  Group = -> [Zr_element001]
  conduct = 2
  density = 1
  expand = 3
  formula = Zr
  name = G4_Zr
  specific = 4
FEATURE [App::DocumentObjectGroupPython] Nb_element001  label="Nb_element : 1"  # scripted group (container) (typed FeaturePython)
  n = 1
  ref = Nb_element
FEATURE [App::DocumentObjectGroupPython] G4_Nb  # scripted group (container) (typed FeaturePython)
  Dunit = g/cm3
  Dvalue = 8.57
  Group = -> [Nb_element001]
  conduct = 2
  density = 1
  expand = 3
  formula = Nb
  name = G4_Nb
  specific = 4
FEATURE [App::DocumentObjectGroupPython] Mo_element001  label="Mo_element : 1"  # scripted group (container) (typed FeaturePython)
  n = 1
  ref = Mo_element
FEATURE [App::DocumentObjectGroupPython] G4_Mo  # scripted group (container) (typed FeaturePython)
  Dunit = g/cm3
  Dvalue = 10.22
  Group = -> [Mo_element001]
  conduct = 2
  density = 1
  expand = 3
  formula = Mo
  name = G4_Mo
  specific = 4
FEATURE [App::DocumentObjectGroupPython] Tc_element001  label="Tc_element : 1"  # scripted group (container) (typed FeaturePython)
  n = 1
  ref = Tc_element
FEATURE [App::DocumentObjectGroupPython] G4_Tc  # scripted group (container) (typed FeaturePython)
  Dunit = g/cm3
  Dvalue = 11.5
  Group = -> [Tc_element001]
  conduct = 2
  density = 1
  expand = 3
  formula = Tc
  name = G4_Tc
  specific = 4
FEATURE [App::DocumentObjectGroupPython] Ru_element001  label="Ru_element : 1"  # scripted group (container) (typed FeaturePython)
  n = 1
  ref = Ru_element
FEATURE [App::DocumentObjectGroupPython] G4_Ru  # scripted group (container) (typed FeaturePython)
  Dunit = g/cm3
  Dvalue = 12.41
  Group = -> [Ru_element001]
  conduct = 2
  density = 1
  expand = 3
  formula = Ru
  name = G4_Ru
  specific = 4
FEATURE [App::DocumentObjectGroupPython] Rh_element001  label="Rh_element : 1"  # scripted group (container) (typed FeaturePython)
  n = 1
  ref = Rh_element
FEATURE [App::DocumentObjectGroupPython] G4_Rh  # scripted group (container) (typed FeaturePython)
  Dunit = g/cm3
  Dvalue = 12.41
  Group = -> [Rh_element001]
  conduct = 2
  density = 1
  expand = 3
  formula = Rh
  name = G4_Rh
  specific = 4
FEATURE [App::DocumentObjectGroupPython] Pd_element001  label="Pd_element : 1"  # scripted group (container) (typed FeaturePython)
  n = 1
  ref = Pd_element
FEATURE [App::DocumentObjectGroupPython] G4_Pd  # scripted group (container) (typed FeaturePython)
  Dunit = g/cm3
  Dvalue = 12.02
  Group = -> [Pd_element001]
  conduct = 2
  density = 1
  expand = 3
  formula = Pd
  name = G4_Pd
  specific = 4
FEATURE [App::DocumentObjectGroupPython] Ag_element006  label="Ag_element : 004"  # scripted group (container) (typed FeaturePython)
  n = 1
  ref = Ag_element
FEATURE [App::DocumentObjectGroupPython] G4_Ag  # scripted group (container) (typed FeaturePython)
  Dunit = g/cm3
  Dvalue = 10.5
  Group = -> [Ag_element006]
  conduct = 2
  density = 1
  expand = 3
  formula = Ag
  name = G4_Ag
  specific = 4
FEATURE [App::DocumentObjectGroupPython] Cd_element003  label="Cd_element : 003"  # scripted group (container) (typed FeaturePython)
  n = 1
  ref = Cd_element
FEATURE [App::DocumentObjectGroupPython] G4_Cd  # scripted group (container) (typed FeaturePython)
  Dunit = g/cm3
  Dvalue = 8.65
  Group = -> [Cd_element003]
  conduct = 2
  density = 1
  expand = 3
  formula = Cd
  name = G4_Cd
  specific = 4
FEATURE [App::DocumentObjectGroupPython] In_element001  label="In_element : 1"  # scripted group (container) (typed FeaturePython)
  n = 1
  ref = In_element
FEATURE [App::DocumentObjectGroupPython] G4_In  # scripted group (container) (typed FeaturePython)
  Dunit = g/cm3
  Dvalue = 7.31
  Group = -> [In_element001]
  conduct = 2
  density = 1
  expand = 3
  formula = In
  name = G4_In
  specific = 4
FEATURE [App::DocumentObjectGroupPython] Sn_element001  label="Sn_element : 1"  # scripted group (container) (typed FeaturePython)
  n = 1
  ref = Sn_element
FEATURE [App::DocumentObjectGroupPython] G4_Sn  # scripted group (container) (typed FeaturePython)
  Dunit = g/cm3
  Dvalue = 7.31
  Group = -> [Sn_element001]
  conduct = 2
  density = 1
  expand = 3
  formula = Sn
  name = G4_Sn
  specific = 4
FEATURE [App::DocumentObjectGroupPython] Sb_element001  label="Sb_element : 1"  # scripted group (container) (typed FeaturePython)
  n = 1
  ref = Sb_element
FEATURE [App::DocumentObjectGroupPython] G4_Sb  # scripted group (container) (typed FeaturePython)
  Dunit = g/cm3
  Dvalue = 6.691
  Group = -> [Sb_element001]
  conduct = 2
  density = 1
  expand = 3
  formula = Sb
  name = G4_Sb
  specific = 4
FEATURE [App::DocumentObjectGroupPython] Te_element002  label="Te_element : 002"  # scripted group (container) (typed FeaturePython)
  n = 1
  ref = Te_element
FEATURE [App::DocumentObjectGroupPython] G4_Te  # scripted group (container) (typed FeaturePython)
  Dunit = g/cm3
  Dvalue = 6.24
  Group = -> [Te_element002]
  conduct = 2
  density = 1
  expand = 3
  formula = Te
  name = G4_Te
  specific = 4
FEATURE [App::DocumentObjectGroupPython] I_element010  label="I_element : 006"  # scripted group (container) (typed FeaturePython)
  n = 1
  ref = I_element
FEATURE [App::DocumentObjectGroupPython] G4_I  # scripted group (container) (typed FeaturePython)
  Dunit = g/cm3
  Dvalue = 4.93
  Group = -> [I_element010]
  conduct = 2
  density = 1
  expand = 3
  formula = I
  name = G4_I
  specific = 4
FEATURE [App::DocumentObjectGroupPython] Xe_element001  label="Xe_element : 1"  # scripted group (container) (typed FeaturePython)
  n = 1
  ref = Xe_element
FEATURE [App::DocumentObjectGroupPython] G4_Xe  # scripted group (container) (typed FeaturePython)
  Dunit = g/cm3
  Dvalue = 0.00548536
  Group = -> [Xe_element001]
  conduct = 2
  density = 1
  expand = 3
  formula = Xe
  name = G4_Xe
  specific = 4
FEATURE [App::DocumentObjectGroupPython] Cs_element003  label="Cs_element : 003"  # scripted group (container) (typed FeaturePython)
  n = 1
  ref = Cs_element
FEATURE [App::DocumentObjectGroupPython] G4_Cs  # scripted group (container) (typed FeaturePython)
  Dunit = g/cm3
  Dvalue = 1.873
  Group = -> [Cs_element003]
  conduct = 2
  density = 1
  expand = 3
  formula = Cs
  name = G4_Cs
  specific = 4
FEATURE [App::DocumentObjectGroupPython] Ba_element003  label="Ba_element : 003"  # scripted group (container) (typed FeaturePython)
  n = 1
  ref = Ba_element
FEATURE [App::DocumentObjectGroupPython] G4_Ba  # scripted group (container) (typed FeaturePython)
  Dunit = g/cm3
  Dvalue = 3.5
  Group = -> [Ba_element003]
  conduct = 2
  density = 1
  expand = 3
  formula = Ba
  name = G4_Ba
  specific = 4
FEATURE [App::DocumentObjectGroupPython] La_element003  label="La_element : 003"  # scripted group (container) (typed FeaturePython)
  n = 1
  ref = La_element
FEATURE [App::DocumentObjectGroupPython] G4_La  # scripted group (container) (typed FeaturePython)
  Dunit = g/cm3
  Dvalue = 6.154
  Group = -> [La_element003]
  conduct = 2
  density = 1
  expand = 3
  formula = La
  name = G4_La
  specific = 4
FEATURE [App::DocumentObjectGroupPython] Ce_element002  label="Ce_element : 1"  # scripted group (container) (typed FeaturePython)
  n = 1
  ref = Ce_element
FEATURE [App::DocumentObjectGroupPython] G4_Ce  # scripted group (container) (typed FeaturePython)
  Dunit = g/cm3
  Dvalue = 6.657
  Group = -> [Ce_element002]
  conduct = 2
  density = 1
  expand = 3
  formula = Ce
  name = G4_Ce
  specific = 4
FEATURE [App::DocumentObjectGroupPython] Pr_element001  label="Pr_element : 1"  # scripted group (container) (typed FeaturePython)
  n = 1
  ref = Pr_element
FEATURE [App::DocumentObjectGroupPython] G4_Pr  # scripted group (container) (typed FeaturePython)
  Dunit = g/cm3
  Dvalue = 6.71
  Group = -> [Pr_element001]
  conduct = 2
  density = 1
  expand = 3
  formula = Pr
  name = G4_Pr
  specific = 4
FEATURE [App::DocumentObjectGroupPython] Nd_element001  label="Nd_element : 1"  # scripted group (container) (typed FeaturePython)
  n = 1
  ref = Nd_element
FEATURE [App::DocumentObjectGroupPython] G4_Nd  # scripted group (container) (typed FeaturePython)
  Dunit = g/cm3
  Dvalue = 6.9
  Group = -> [Nd_element001]
  conduct = 2
  density = 1
  expand = 3
  formula = Nd
  name = G4_Nd
  specific = 4
FEATURE [App::DocumentObjectGroupPython] Pm_element001  label="Pm_element : 1"  # scripted group (container) (typed FeaturePython)
  n = 1
  ref = Pm_element
FEATURE [App::DocumentObjectGroupPython] G4_Pm  # scripted group (container) (typed FeaturePython)
  Dunit = g/cm3
  Dvalue = 7.22
  Group = -> [Pm_element001]
  conduct = 2
  density = 1
  expand = 3
  formula = Pm
  name = G4_Pm
  specific = 4
FEATURE [App::DocumentObjectGroupPython] Sm_element001  label="Sm_element : 1"  # scripted group (container) (typed FeaturePython)
  n = 1
  ref = Sm_element
FEATURE [App::DocumentObjectGroupPython] G4_Sm  # scripted group (container) (typed FeaturePython)
  Dunit = g/cm3
  Dvalue = 7.46
  Group = -> [Sm_element001]
  conduct = 2
  density = 1
  expand = 3
  formula = Sm
  name = G4_Sm
  specific = 4
FEATURE [App::DocumentObjectGroupPython] Eu_element001  label="Eu_element : 1"  # scripted group (container) (typed FeaturePython)
  n = 1
  ref = Eu_element
FEATURE [App::DocumentObjectGroupPython] G4_Eu  # scripted group (container) (typed FeaturePython)
  Dunit = g/cm3
  Dvalue = 5.243
  Group = -> [Eu_element001]
  conduct = 2
  density = 1
  expand = 3
  formula = Eu
  name = G4_Eu
  specific = 4
FEATURE [App::DocumentObjectGroupPython] Gd_element002  label="Gd_element : 1"  # scripted group (container) (typed FeaturePython)
  n = 1
  ref = Gd_element
FEATURE [App::DocumentObjectGroupPython] G4_Gd  # scripted group (container) (typed FeaturePython)
  Dunit = g/cm3
  Dvalue = 7.9004
  Group = -> [Gd_element002]
  conduct = 2
  density = 1
  expand = 3
  formula = Gd
  name = G4_Gd
  specific = 4
FEATURE [App::DocumentObjectGroupPython] Tb_element001  label="Tb_element : 1"  # scripted group (container) (typed FeaturePython)
  n = 1
  ref = Tb_element
FEATURE [App::DocumentObjectGroupPython] G4_Tb  # scripted group (container) (typed FeaturePython)
  Dunit = g/cm3
  Dvalue = 8.229
  Group = -> [Tb_element001]
  conduct = 2
  density = 1
  expand = 3
  formula = Tb
  name = G4_Tb
  specific = 4
FEATURE [App::DocumentObjectGroupPython] Dy_element001  label="Dy_element : 1"  # scripted group (container) (typed FeaturePython)
  n = 1
  ref = Dy_element
FEATURE [App::DocumentObjectGroupPython] G4_Dy  # scripted group (container) (typed FeaturePython)
  Dunit = g/cm3
  Dvalue = 8.55
  Group = -> [Dy_element001]
  conduct = 2
  density = 1
  expand = 3
  formula = Dy
  name = G4_Dy
  specific = 4
FEATURE [App::DocumentObjectGroupPython] Ho_element001  label="Ho_element : 1"  # scripted group (container) (typed FeaturePython)
  n = 1
  ref = Ho_element
FEATURE [App::DocumentObjectGroupPython] G4_Ho  # scripted group (container) (typed FeaturePython)
  Dunit = g/cm3
  Dvalue = 8.795
  Group = -> [Ho_element001]
  conduct = 2
  density = 1
  expand = 3
  formula = Ho
  name = G4_Ho
  specific = 4
FEATURE [App::DocumentObjectGroupPython] Er_element001  label="Er_element : 1"  # scripted group (container) (typed FeaturePython)
  n = 1
  ref = Er_element
FEATURE [App::DocumentObjectGroupPython] G4_Er  # scripted group (container) (typed FeaturePython)
  Dunit = g/cm3
  Dvalue = 9.066
  Group = -> [Er_element001]
  conduct = 2
  density = 1
  expand = 3
  formula = Er
  name = G4_Er
  specific = 4
FEATURE [App::DocumentObjectGroupPython] Tm_element001  label="Tm_element : 1"  # scripted group (container) (typed FeaturePython)
  n = 1
  ref = Tm_element
FEATURE [App::DocumentObjectGroupPython] G4_Tm  # scripted group (container) (typed FeaturePython)
  Dunit = g/cm3
  Dvalue = 9.321
  Group = -> [Tm_element001]
  conduct = 2
  density = 1
  expand = 3
  formula = Tm
  name = G4_Tm
  specific = 4
FEATURE [App::DocumentObjectGroupPython] Yb_element001  label="Yb_element : 1"  # scripted group (container) (typed FeaturePython)
  n = 1
  ref = Yb_element
FEATURE [App::DocumentObjectGroupPython] G4_Yb  # scripted group (container) (typed FeaturePython)
  Dunit = g/cm3
  Dvalue = 6.73
  Group = -> [Yb_element001]
  conduct = 2
  density = 1
  expand = 3
  formula = Yb
  name = G4_Yb
  specific = 4
FEATURE [App::DocumentObjectGroupPython] Lu_element001  label="Lu_element : 1"  # scripted group (container) (typed FeaturePython)
  n = 1
  ref = Lu_element
FEATURE [App::DocumentObjectGroupPython] G4_Lu  # scripted group (container) (typed FeaturePython)
  Dunit = g/cm3
  Dvalue = 9.84
  Group = -> [Lu_element001]
  conduct = 2
  density = 1
  expand = 3
  formula = Lu
  name = G4_Lu
  specific = 4
FEATURE [App::DocumentObjectGroupPython] Hf_element001  label="Hf_element : 1"  # scripted group (container) (typed FeaturePython)
  n = 1
  ref = Hf_element
FEATURE [App::DocumentObjectGroupPython] G4_Hf  # scripted group (container) (typed FeaturePython)
  Dunit = g/cm3
  Dvalue = 13.31
  Group = -> [Hf_element001]
  conduct = 2
  density = 1
  expand = 3
  formula = Hf
  name = G4_Hf
  specific = 4
FEATURE [App::DocumentObjectGroupPython] Ta_element001  label="Ta_element : 1"  # scripted group (container) (typed FeaturePython)
  n = 1
  ref = Ta_element
FEATURE [App::DocumentObjectGroupPython] G4_Ta  # scripted group (container) (typed FeaturePython)
  Dunit = g/cm3
  Dvalue = 16.654
  Group = -> [Ta_element001]
  conduct = 2
  density = 1
  expand = 3
  formula = Ta
  name = G4_Ta
  specific = 4
FEATURE [App::DocumentObjectGroupPython] W_element004  label="W_element : 004"  # scripted group (container) (typed FeaturePython)
  n = 1
  ref = W_element
FEATURE [App::DocumentObjectGroupPython] G4_W  # scripted group (container) (typed FeaturePython)
  Dunit = g/cm3
  Dvalue = 19.3
  Group = -> [W_element004]
  conduct = 2
  density = 1
  expand = 3
  formula = W
  name = G4_W
  specific = 4
FEATURE [App::DocumentObjectGroupPython] Re_element001  label="Re_element : 1"  # scripted group (container) (typed FeaturePython)
  n = 1
  ref = Re_element
FEATURE [App::DocumentObjectGroupPython] G4_Re  # scripted group (container) (typed FeaturePython)
  Dunit = g/cm3
  Dvalue = 21.02
  Group = -> [Re_element001]
  conduct = 2
  density = 1
  expand = 3
  formula = Re
  name = G4_Re
  specific = 4
FEATURE [App::DocumentObjectGroupPython] Os_element001  label="Os_element : 1"  # scripted group (container) (typed FeaturePython)
  n = 1
  ref = Os_element
FEATURE [App::DocumentObjectGroupPython] G4_Os  # scripted group (container) (typed FeaturePython)
  Dunit = g/cm3
  Dvalue = 22.57
  Group = -> [Os_element001]
  conduct = 2
  density = 1
  expand = 3
  formula = Os
  name = G4_Os
  specific = 4
FEATURE [App::DocumentObjectGroupPython] Ir_element001  label="Ir_element : 1"  # scripted group (container) (typed FeaturePython)
  n = 1
  ref = Ir_element
FEATURE [App::DocumentObjectGroupPython] G4_Ir  # scripted group (container) (typed FeaturePython)
  Dunit = g/cm3
  Dvalue = 22.42
  Group = -> [Ir_element001]
  conduct = 2
  density = 1
  expand = 3
  formula = Ir
  name = G4_Ir
  specific = 4
FEATURE [App::DocumentObjectGroupPython] Pt_element001  label="Pt_element : 1"  # scripted group (container) (typed FeaturePython)
  n = 1
  ref = Pt_element
FEATURE [App::DocumentObjectGroupPython] G4_Pt  # scripted group (container) (typed FeaturePython)
  Dunit = g/cm3
  Dvalue = 21.45
  Group = -> [Pt_element001]
  conduct = 2
  density = 1
  expand = 3
  formula = Pt
  name = G4_Pt
  specific = 4
FEATURE [App::DocumentObjectGroupPython] Au_element001  label="Au_element : 1"  # scripted group (container) (typed FeaturePython)
  n = 1
  ref = Au_element
FEATURE [App::DocumentObjectGroupPython] G4_Au  # scripted group (container) (typed FeaturePython)
  Dunit = g/cm3
  Dvalue = 19.32
  Group = -> [Au_element001]
  conduct = 2
  density = 1
  expand = 3
  formula = Au
  name = G4_Au
  specific = 4
FEATURE [App::DocumentObjectGroupPython] Hg_element002  label="Hg_element : 002"  # scripted group (container) (typed FeaturePython)
  n = 1
  ref = Hg_element
FEATURE [App::DocumentObjectGroupPython] G4_Hg  # scripted group (container) (typed FeaturePython)
  Dunit = g/cm3
  Dvalue = 13.546
  Group = -> [Hg_element002]
  conduct = 2
  density = 1
  expand = 3
  formula = Hg
  name = G4_Hg
  specific = 4
FEATURE [App::DocumentObjectGroupPython] Tl_element002  label="Tl_element : 002"  # scripted group (container) (typed FeaturePython)
  n = 1
  ref = Tl_element
FEATURE [App::DocumentObjectGroupPython] G4_Tl  # scripted group (container) (typed FeaturePython)
  Dunit = g/cm3
  Dvalue = 11.72
  Group = -> [Tl_element002]
  conduct = 2
  density = 1
  expand = 3
  formula = Tl
  name = G4_Tl
  specific = 4
FEATURE [App::DocumentObjectGroupPython] Pb_element003  label="Pb_element : 1"  # scripted group (container) (typed FeaturePython)
  n = 1
  ref = Pb_element
FEATURE [App::DocumentObjectGroupPython] G4_Pb  # scripted group (container) (typed FeaturePython)
  Dunit = g/cm3
  Dvalue = 11.35
  Group = -> [Pb_element003]
  conduct = 2
  density = 1
  expand = 3
  formula = Pb
  name = G4_Pb
  specific = 4
FEATURE [App::DocumentObjectGroupPython] Bi_element002  label="Bi_element : 1"  # scripted group (container) (typed FeaturePython)
  n = 1
  ref = Bi_element
FEATURE [App::DocumentObjectGroupPython] G4_Bi  # scripted group (container) (typed FeaturePython)
  Dunit = g/cm3
  Dvalue = 9.747
  Group = -> [Bi_element002]
  conduct = 2
  density = 1
  expand = 3
  formula = Bi
  name = G4_Bi
  specific = 4
FEATURE [App::DocumentObjectGroupPython] Po_element001  label="Po_element : 1"  # scripted group (container) (typed FeaturePython)
  n = 1
  ref = Po_element
FEATURE [App::DocumentObjectGroupPython] G4_Po  # scripted group (container) (typed FeaturePython)
  Dunit = g/cm3
  Dvalue = 9.32
  Group = -> [Po_element001]
  conduct = 2
  density = 1
  expand = 3
  formula = Po
  name = G4_Po
  specific = 4
FEATURE [App::DocumentObjectGroupPython] At_element001  label="At_element : 1"  # scripted group (container) (typed FeaturePython)
  n = 1
  ref = At_element
FEATURE [App::DocumentObjectGroupPython] G4_At  # scripted group (container) (typed FeaturePython)
  Dunit = g/cm3
  Dvalue = 9.32
  Group = -> [At_element001]
  conduct = 2
  density = 1
  expand = 3
  formula = At
  name = G4_At
  specific = 4
FEATURE [App::DocumentObjectGroupPython] Rn_element001  label="Rn_element : 1"  # scripted group (container) (typed FeaturePython)
  n = 1
  ref = Rn_element
FEATURE [App::DocumentObjectGroupPython] G4_Rn  # scripted group (container) (typed FeaturePython)
  Dunit = g/cm3
  Dvalue = 0.00900662
  Group = -> [Rn_element001]
  conduct = 2
  density = 1
  expand = 3
  formula = Rn
  name = G4_Rn
  specific = 4
FEATURE [App::DocumentObjectGroupPython] Fr_element001  label="Fr_element : 1"  # scripted group (container) (typed FeaturePython)
  n = 1
  ref = Fr_element
FEATURE [App::DocumentObjectGroupPython] G4_Fr  # scripted group (container) (typed FeaturePython)
  Dunit = g/cm3
  Dvalue = 1
  Group = -> [Fr_element001]
  conduct = 2
  density = 1
  expand = 3
  formula = Fr
  name = G4_Fr
  specific = 4
FEATURE [App::DocumentObjectGroupPython] Ra_element001  label="Ra_element : 1"  # scripted group (container) (typed FeaturePython)
  n = 1
  ref = Ra_element
FEATURE [App::DocumentObjectGroupPython] G4_Ra  # scripted group (container) (typed FeaturePython)
  Dunit = g/cm3
  Dvalue = 5
  Group = -> [Ra_element001]
  conduct = 2
  density = 1
  expand = 3
  formula = Ra
  name = G4_Ra
  specific = 4
FEATURE [App::DocumentObjectGroupPython] Ac_element001  label="Ac_element : 1"  # scripted group (container) (typed FeaturePython)
  n = 1
  ref = Ac_element
FEATURE [App::DocumentObjectGroupPython] G4_Ac  # scripted group (container) (typed FeaturePython)
  Dunit = g/cm3
  Dvalue = 10.07
  Group = -> [Ac_element001]
  conduct = 2
  density = 1
  expand = 3
  formula = Ac
  name = G4_Ac
  specific = 4
FEATURE [App::DocumentObjectGroupPython] Th_element001  label="Th_element : 1"  # scripted group (container) (typed FeaturePython)
  n = 1
  ref = Th_element
FEATURE [App::DocumentObjectGroupPython] G4_Th  # scripted group (container) (typed FeaturePython)
  Dunit = g/cm3
  Dvalue = 11.72
  Group = -> [Th_element001]
  conduct = 2
  density = 1
  expand = 3
  formula = Th
  name = G4_Th
  specific = 4
FEATURE [App::DocumentObjectGroupPython] Pa_element001  label="Pa_element : 1"  # scripted group (container) (typed FeaturePython)
  n = 1
  ref = Pa_element
FEATURE [App::DocumentObjectGroupPython] G4_Pa  # scripted group (container) (typed FeaturePython)
  Dunit = g/cm3
  Dvalue = 15.37
  Group = -> [Pa_element001]
  conduct = 2
  density = 1
  expand = 3
  formula = Pa
  name = G4_Pa
  specific = 4
FEATURE [App::DocumentObjectGroupPython] U_element004  label="U_element : 004"  # scripted group (container) (typed FeaturePython)
  n = 1
  ref = U_element
FEATURE [App::DocumentObjectGroupPython] G4_U  # scripted group (container) (typed FeaturePython)
  Dunit = g/cm3
  Dvalue = 18.95
  Group = -> [U_element004]
  conduct = 2
  density = 1
  expand = 3
  formula = U
  name = G4_U
  specific = 4
FEATURE [App::DocumentObjectGroupPython] Np_element001  label="Np_element : 1"  # scripted group (container) (typed FeaturePython)
  n = 1
  ref = Np_element
FEATURE [App::DocumentObjectGroupPython] G4_Np  # scripted group (container) (typed FeaturePython)
  Dunit = g/cm3
  Dvalue = 20.25
  Group = -> [Np_element001]
  conduct = 2
  density = 1
  expand = 3
  formula = Np
  name = G4_Np
  specific = 4
FEATURE [App::DocumentObjectGroupPython] Pu_element002  label="Pu_element : 002"  # scripted group (container) (typed FeaturePython)
  n = 1
  ref = Pu_element
FEATURE [App::DocumentObjectGroupPython] G4_Pu  # scripted group (container) (typed FeaturePython)
  Dunit = g/cm3
  Dvalue = 19.84
  Group = -> [Pu_element002]
  conduct = 2
  density = 1
  expand = 3
  formula = Pu
  name = G4_Pu
  specific = 4
FEATURE [App::DocumentObjectGroupPython] Am_element001  label="Am_element : 1"  # scripted group (container) (typed FeaturePython)
  n = 1
  ref = Am_element
FEATURE [App::DocumentObjectGroupPython] G4_Am  # scripted group (container) (typed FeaturePython)
  Dunit = g/cm3
  Dvalue = 13.67
  Group = -> [Am_element001]
  conduct = 2
  density = 1
  expand = 3
  formula = Am
  name = G4_Am
  specific = 4
FEATURE [App::DocumentObjectGroupPython] Cm_element001  label="Cm_element : 1"  # scripted group (container) (typed FeaturePython)
  n = 1
  ref = Cm_element
FEATURE [App::DocumentObjectGroupPython] G4_Cm  # scripted group (container) (typed FeaturePython)
  Dunit = g/cm3
  Dvalue = 13.51
  Group = -> [Cm_element001]
  conduct = 2
  density = 1
  expand = 3
  formula = Cm
  name = G4_Cm
  specific = 4
FEATURE [App::DocumentObjectGroupPython] Bk_element001  label="Bk_element : 1"  # scripted group (container) (typed FeaturePython)
  n = 1
  ref = Bk_element
FEATURE [App::DocumentObjectGroupPython] G4_Bk  # scripted group (container) (typed FeaturePython)
  Dunit = g/cm3
  Dvalue = 14
  Group = -> [Bk_element001]
  conduct = 2
  density = 1
  expand = 3
  formula = Bk
  name = G4_Bk
  specific = 4
FEATURE [App::DocumentObjectGroupPython] Cf_element001  label="Cf_element : 1"  # scripted group (container) (typed FeaturePython)
  n = 1
  ref = Cf_element
FEATURE [App::DocumentObjectGroupPython] G4_Cf  # scripted group (container) (typed FeaturePython)
  Dunit = g/cm3
  Dvalue = 10
  Group = -> [Cf_element001]
  conduct = 2
  density = 1
  expand = 3
  formula = Cf
  name = G4_Cf
  specific = 4
FEATURE [App::DocumentObjectGroupPython] Element  # scripted group (container) (typed FeaturePython)
  Group = -> [G4_H,G4_He,G4_Li,G4_Be,G4_B,G4_C,G4_N,G4_O,G4_F,G4_Ne,G4_Na,G4_Mg,G4_Al,G4_Si,G4_P,G4_S,G4_Cl,G4_Ar,G4_K,G4_Ca,G4_Sc,G4_Ti,G4_V,G4_Cr,G4_Mn,G4_Fe,G4_Co,G4_Ni,G4_Cu,G4_Zn,G4_Ga,G4_Ge,G4_As,G4_Se,G4_Br,G4_Kr,G4_Rb,G4_Sr,G4_Y,G4_Zr,G4_Nb,G4_Mo,G4_Tc,G4_Ru,G4_Rh,G4_Pd,G4_Ag,G4_Cd,G4_In,G4_Sn,G4_Sb,G4_Te,G4_I,G4_Xe,G4_Cs,G4_Ba,G4_La,G4_Ce,G4_Pr,G4_Nd,G4_Pm,G4_Sm,G4_Eu,G4_Gd,G4_Tb,G4_Dy,G4_Ho,G4_Er,+30 more]
FEATURE [App::DocumentObjectGroupPython] H_element114  label="H_element : 063"  # scripted group (container) (typed FeaturePython)
  n = 2
  ref = H_element
FEATURE [App::DocumentObjectGroupPython] G4_lH2  # scripted group (container) (typed FeaturePython)
  Dunit = g/cm3
  Dvalue = 0.0708
  Group = -> [H_element114]
  conduct = 2
  density = 1
  expand = 3
  formula = G4_lH2
  name = G4_lH2
  specific = 4
FEATURE [App::DocumentObjectGroupPython] N_element049  label="N_element : 022"  # scripted group (container) (typed FeaturePython)
  n = 2
  ref = N_element
FEATURE [App::DocumentObjectGroupPython] G4_lN2  # scripted group (container) (typed FeaturePython)
  Dunit = g/cm3
  Dvalue = 0.807
  Group = -> [N_element049]
  conduct = 2
  density = 1
  expand = 3
  formula = G4_lN2
  name = G4_lN2
  specific = 4
FEATURE [App::DocumentObjectGroupPython] O_element106  label="O_element : 060"  # scripted group (container) (typed FeaturePython)
  n = 2
  ref = O_element
FEATURE [App::DocumentObjectGroupPython] G4_lO2  # scripted group (container) (typed FeaturePython)
  Dunit = g/cm3
  Dvalue = 1.141
  Group = -> [O_element106]
  conduct = 2
  density = 1
  expand = 3
  formula = G4_lO2
  name = G4_lO2
  specific = 4
FEATURE [App::DocumentObjectGroupPython] Ar  label="Ar : 1"  # scripted group (container) (typed FeaturePython)
  n = 1
  ref = Ar
FEATURE [App::DocumentObjectGroupPython] G4_lAr  # scripted group (container) (typed FeaturePython)
  Dunit = g/cm3
  Dvalue = 1.396
  Group = -> [Ar]
  conduct = 2
  density = 1
  expand = 3
  formula = G4_lAr
  name = G4_lAr
  specific = 4
FEATURE [App::DocumentObjectGroupPython] Br  label="Br : 1"  # scripted group (container) (typed FeaturePython)
  n = 1
  ref = Br
FEATURE [App::DocumentObjectGroupPython] G4_lBr  # scripted group (container) (typed FeaturePython)
  Dunit = g/cm3
  Dvalue = 3.1028
  Group = -> [Br]
  conduct = 2
  density = 1
  expand = 3
  formula = G4_lBr
  name = G4_lBr
  specific = 4
FEATURE [App::DocumentObjectGroupPython] Kr  label="Kr : 1"  # scripted group (container) (typed FeaturePython)
  n = 1
  ref = Kr
FEATURE [App::DocumentObjectGroupPython] G4_lKr  # scripted group (container) (typed FeaturePython)
  Dunit = g/cm3
  Dvalue = 2.418
  Group = -> [Kr]
  conduct = 2
  density = 1
  expand = 3
  formula = G4_lKr
  name = G4_lKr
  specific = 4
FEATURE [App::DocumentObjectGroupPython] Xe  label="Xe : 1"  # scripted group (container) (typed FeaturePython)
  n = 1
  ref = Xe
FEATURE [App::DocumentObjectGroupPython] G4_lXe  # scripted group (container) (typed FeaturePython)
  Dunit = g/cm3
  Dvalue = 2.953
  Group = -> [Xe]
  conduct = 2
  density = 1
  expand = 3
  formula = G4_lXe
  name = G4_lXe
  specific = 4
FEATURE [App::DocumentObjectGroupPython] O_element107  label="O_element : 061"  # scripted group (container) (typed FeaturePython)
  n = 4
  ref = O_element
FEATURE [App::DocumentObjectGroupPython] Pb_element004  label="Pb_element : 002"  # scripted group (container) (typed FeaturePython)
  n = 1
  ref = Pb_element
FEATURE [App::DocumentObjectGroupPython] W_element005  label="W_element : 005"  # scripted group (container) (typed FeaturePython)
  n = 1
  ref = W_element
FEATURE [App::DocumentObjectGroupPython] G4_PbWO4  # scripted group (container) (typed FeaturePython)
  Dunit = g/cm3
  Dvalue = 8.28
  Group = -> [O_element107,Pb_element004,W_element005]
  conduct = 2
  density = 1
  expand = 3
  formula = G4_PbWO4
  name = G4_PbWO4
  specific = 4
FEATURE [App::DocumentObjectGroupPython] alactic  label="alactic : 1"  # scripted group (container) (typed FeaturePython)
  n = 1
  ref = alactic
FEATURE [App::DocumentObjectGroupPython] G4_Galactic  # scripted group (container) (typed FeaturePython)
  Dunit = g/cm3
  Dvalue = 0
  Group = -> [alactic]
  conduct = 2
  density = 1
  expand = 3
  formula = G4_Galactic
  name = G4_Galactic
  specific = 4
FEATURE [App::DocumentObjectGroupPython] RAPHITE_POROUS  label="RAPHITE_POROUS : 1"  # scripted group (container) (typed FeaturePython)
  n = 1
  ref = RAPHITE_POROUS
FEATURE [App::DocumentObjectGroupPython] G4_GRAPHITE_POROUS  # scripted group (container) (typed FeaturePython)
  Dunit = g/cm3
  Dvalue = 1.7
  Group = -> [RAPHITE_POROUS]
  conduct = 2
  density = 1
  expand = 3
  formula = G4_GRAPHITE_POROUS
  name = G4_GRAPHITE_POROUS
  specific = 4
FEATURE [App::DocumentObjectGroupPython] H_element115  label="H_element : 0.150"  # scripted group (container) (typed FeaturePython)
  n = 0.080538
FEATURE [App::DocumentObjectGroupPython] C_element125  label="C_element : 0.600"  # scripted group (container) (typed FeaturePython)
  n = 0.599848
FEATURE [App::DocumentObjectGroupPython] O_element108  label="O_element : 0.320"  # scripted group (container) (typed FeaturePython)
  n = 0.319614
FEATURE [App::DocumentObjectGroupPython] G4_LUCITE  # scripted group (container) (typed FeaturePython)
  Dunit = g/cm3
  Dvalue = 1.19
  Group = -> [H_element115,C_element125,O_element108]
  conduct = 2
  density = 1
  expand = 3
  formula = G4_LUCITE
  name = G4_LUCITE
  specific = 4
FEATURE [App::DocumentObjectGroupPython] Cu_element002  label="Cu_element : 62"  # scripted group (container) (typed FeaturePython)
  n = 62
  ref = Cu_element
FEATURE [App::DocumentObjectGroupPython] Zn_element002  label="Zn_element : 35"  # scripted group (container) (typed FeaturePython)
  n = 35
  ref = Zn_element
FEATURE [App::DocumentObjectGroupPython] Pb_element005  label="Pb_element : 3"  # scripted group (container) (typed FeaturePython)
  n = 3
  ref = Pb_element
FEATURE [App::DocumentObjectGroupPython] G4_BRASS  # scripted group (container) (typed FeaturePython)
  Dunit = g/cm3
  Dvalue = 8.52
  Group = -> [Cu_element002,Zn_element002,Pb_element005]
  conduct = 2
  density = 1
  expand = 3
  formula = G4_BRASS
  name = G4_BRASS
  specific = 4
FEATURE [App::DocumentObjectGroupPython] Cu_element003  label="Cu_element : 89"  # scripted group (container) (typed FeaturePython)
  n = 89
  ref = Cu_element
FEATURE [App::DocumentObjectGroupPython] Zn_element003  label="Zn_element : 9"  # scripted group (container) (typed FeaturePython)
  n = 9
  ref = Zn_element
FEATURE [App::DocumentObjectGroupPython] Pb_element006  label="Pb_element : 2"  # scripted group (container) (typed FeaturePython)
  n = 2
  ref = Pb_element
FEATURE [App::DocumentObjectGroupPython] G4_BRONZE  # scripted group (container) (typed FeaturePython)
  Dunit = g/cm3
  Dvalue = 8.82
  Group = -> [Cu_element003,Zn_element003,Pb_element006]
  conduct = 2
  density = 1
  expand = 3
  formula = G4_BRONZE
  name = G4_BRONZE
  specific = 4
FEATURE [App::DocumentObjectGroupPython] Fe_element008  label="Fe_element : 74"  # scripted group (container) (typed FeaturePython)
  n = 74
  ref = Fe_element
FEATURE [App::DocumentObjectGroupPython] Cr_element002  label="Cr_element : 18"  # scripted group (container) (typed FeaturePython)
  n = 18
  ref = Cr_element
FEATURE [App::DocumentObjectGroupPython] Ni_element002  label="Ni_element : 8"  # scripted group (container) (typed FeaturePython)
  n = 8
  ref = Ni_element
FEATURE [App::DocumentObjectGroupPython] G4_STAINLESS_STEEL  label="G4_STAINLESS-STEEL"  # scripted group (container) (typed FeaturePython)
  Dunit = g/cm3
  Dvalue = 8
  Group = -> [Fe_element008,Cr_element002,Ni_element002]
  conduct = 2
  density = 1
  expand = 3
  formula = G4_STAINLESS-STEEL
  name = G4_STAINLESS-STEEL
  specific = 4
FEATURE [App::DocumentObjectGroupPython] H_element116  label="H_element : 064"  # scripted group (container) (typed FeaturePython)
  n = 18
  ref = H_element
FEATURE [App::DocumentObjectGroupPython] C_element126  label="C_element : 071"  # scripted group (container) (typed FeaturePython)
  n = 12
  ref = C_element
FEATURE [App::DocumentObjectGroupPython] O_element109  label="O_element : 062"  # scripted group (container) (typed FeaturePython)
  n = 7
  ref = O_element
FEATURE [App::DocumentObjectGroupPython] G4_CR39  # scripted group (container) (typed FeaturePython)
  Dunit = g/cm3
  Dvalue = 1.32
  Group = -> [H_element116,C_element126,O_element109]
  conduct = 2
  density = 1
  expand = 3
  formula = G4_CR39
  name = G4_CR39
  specific = 4
FEATURE [App::DocumentObjectGroupPython] H_element117  label="H_element : 38"  # scripted group (container) (typed FeaturePython)
  n = 38
  ref = H_element
FEATURE [App::DocumentObjectGroupPython] C_element127  label="C_element : 072"  # scripted group (container) (typed FeaturePython)
  n = 18
  ref = C_element
FEATURE [App::DocumentObjectGroupPython] O_element110  label="O_element : 063"  # scripted group (container) (typed FeaturePython)
  n = 1
  ref = O_element
FEATURE [App::DocumentObjectGroupPython] G4_OCTADECANOL  # scripted group (container) (typed FeaturePython)
  Dunit = g/cm3
  Dvalue = 0.812
  Group = -> [H_element117,C_element127,O_element110]
  conduct = 2
  density = 1
  expand = 3
  formula = G4_OCTADECANOL
  name = G4_OCTADECANOL
  specific = 4
FEATURE [App::DocumentObjectGroupPython] HEP  # scripted group (container) (typed FeaturePython)
  Group = -> [G4_lH2,G4_lN2,G4_lO2,G4_lAr,G4_lBr,G4_lKr,G4_lXe,G4_PbWO4,G4_Galactic,G4_GRAPHITE_POROUS,G4_LUCITE,G4_BRASS,G4_BRONZE,G4_STAINLESS_STEEL,G4_CR39,G4_OCTADECANOL]
FEATURE [App::DocumentObjectGroupPython] C_element128  label="C_element : 073"  # scripted group (container) (typed FeaturePython)
  n = 14
  ref = C_element
FEATURE [App::DocumentObjectGroupPython] H_element118  label="H_element : 065"  # scripted group (container) (typed FeaturePython)
  n = 10
  ref = H_element
FEATURE [App::DocumentObjectGroupPython] O_element111  label="O_element : 064"  # scripted group (container) (typed FeaturePython)
  n = 2
  ref = O_element
FEATURE [App::DocumentObjectGroupPython] N_element050  label="N_element : 023"  # scripted group (container) (typed FeaturePython)
  n = 2
  ref = N_element
FEATURE [App::DocumentObjectGroupPython] G4_KEVLAR  # scripted group (container) (typed FeaturePython)
  Dunit = g/cm3
  Dvalue = 1.44
  Group = -> [C_element128,H_element118,O_element111,N_element050]
  conduct = 2
  density = 1
  expand = 3
  formula = G4_KEVLAR
  name = G4_KEVLAR
  specific = 4
FEATURE [App::DocumentObjectGroupPython] C_element129  label="C_element : 074"  # scripted group (container) (typed FeaturePython)
  n = 10
  ref = C_element
FEATURE [App::DocumentObjectGroupPython] H_element119  label="H_element : 066"  # scripted group (container) (typed FeaturePython)
  n = 8
  ref = H_element
FEATURE [App::DocumentObjectGroupPython] O_element112  label="O_element : 065"  # scripted group (container) (typed FeaturePython)
  n = 4
  ref = O_element
FEATURE [App::DocumentObjectGroupPython] G4_DACRON  # scripted group (container) (typed FeaturePython)
  Dunit = g/cm3
  Dvalue = 1.4
  Group = -> [C_element129,H_element119,O_element112]
  conduct = 2
  density = 1
  expand = 3
  formula = G4_DACRON
  name = G4_DACRON
  specific = 4
FEATURE [App::DocumentObjectGroupPython] C_element130  label="C_element : 075"  # scripted group (container) (typed FeaturePython)
  n = 4
  ref = C_element
FEATURE [App::DocumentObjectGroupPython] H_element120  label="H_element : 067"  # scripted group (container) (typed FeaturePython)
  n = 5
  ref = H_element
FEATURE [App::DocumentObjectGroupPython] Cl_element030  label="Cl_element : 016"  # scripted group (container) (typed FeaturePython)
  n = 1
  ref = Cl_element
FEATURE [App::DocumentObjectGroupPython] G4_NEOPRENE  # scripted group (container) (typed FeaturePython)
  Dunit = g/cm3
  Dvalue = 1.23
  Group = -> [C_element130,H_element120,Cl_element030]
  conduct = 2
  density = 1
  expand = 3
  formula = G4_NEOPRENE
  name = G4_NEOPRENE
  specific = 4
FEATURE [App::DocumentObjectGroupPython] Space  # scripted group (container) (typed FeaturePython)
  Group = -> [G4_KEVLAR,G4_DACRON,G4_NEOPRENE]
FEATURE [App::DocumentObjectGroupPython] H_element121  label="H_element : 068"  # scripted group (container) (typed FeaturePython)
  n = 5
  ref = H_element
FEATURE [App::DocumentObjectGroupPython] C_element131  label="C_element : 076"  # scripted group (container) (typed FeaturePython)
  n = 4
  ref = C_element
FEATURE [App::DocumentObjectGroupPython] N_element051  label="N_element : 3"  # scripted group (container) (typed FeaturePython)
  n = 3
  ref = N_element
FEATURE [App::DocumentObjectGroupPython] O_element113  label="O_element : 066"  # scripted group (container) (typed FeaturePython)
  n = 1
  ref = O_element
FEATURE [App::DocumentObjectGroupPython] G4_CYTOSINE  # scripted group (container) (typed FeaturePython)
  Dunit = g/cm3
  Dvalue = 1.55
  Group = -> [H_element121,C_element131,N_element051,O_element113]
  conduct = 2
  density = 1
  expand = 3
  formula = G4_CYTOSINE
  name = G4_CYTOSINE
  specific = 4
FEATURE [App::DocumentObjectGroupPython] H_element122  label="H_element : 069"  # scripted group (container) (typed FeaturePython)
  n = 6
  ref = H_element
FEATURE [App::DocumentObjectGroupPython] C_element132  label="C_element : 077"  # scripted group (container) (typed FeaturePython)
  n = 5
  ref = C_element
FEATURE [App::DocumentObjectGroupPython] N_element052  label="N_element : 024"  # scripted group (container) (typed FeaturePython)
  n = 2
  ref = N_element
FEATURE [App::DocumentObjectGroupPython] O_element114  label="O_element : 067"  # scripted group (container) (typed FeaturePython)
  n = 2
  ref = O_element
FEATURE [App::DocumentObjectGroupPython] G4_THYMINE  # scripted group (container) (typed FeaturePython)
  Dunit = g/cm3
  Dvalue = 1.23
  Group = -> [H_element122,C_element132,N_element052,O_element114]
  conduct = 2
  density = 1
  expand = 3
  formula = G4_THYMINE
  name = G4_THYMINE
  specific = 4
FEATURE [App::DocumentObjectGroupPython] H_element123  label="H_element : 070"  # scripted group (container) (typed FeaturePython)
  n = 4
  ref = H_element
FEATURE [App::DocumentObjectGroupPython] C_element133  label="C_element : 078"  # scripted group (container) (typed FeaturePython)
  n = 4
  ref = C_element
FEATURE [App::DocumentObjectGroupPython] N_element053  label="N_element : 025"  # scripted group (container) (typed FeaturePython)
  n = 2
  ref = N_element
FEATURE [App::DocumentObjectGroupPython] O_element115  label="O_element : 068"  # scripted group (container) (typed FeaturePython)
  n = 2
  ref = O_element
FEATURE [App::DocumentObjectGroupPython] G4_URACIL  # scripted group (container) (typed FeaturePython)
  Dunit = g/cm3
  Dvalue = 1.32
  Group = -> [H_element123,C_element133,N_element053,O_element115]
  conduct = 2
  density = 1
  expand = 3
  formula = G4_URACIL
  name = G4_URACIL
  specific = 4
FEATURE [App::DocumentObjectGroupPython] H_element124  label="H_element : 071"  # scripted group (container) (typed FeaturePython)
  n = 4
  ref = H_element
FEATURE [App::DocumentObjectGroupPython] C_element134  label="C_element : 079"  # scripted group (container) (typed FeaturePython)
  n = 5
  ref = C_element
FEATURE [App::DocumentObjectGroupPython] N_element054  label="N_element : 026"  # scripted group (container) (typed FeaturePython)
  n = 5
  ref = N_element
FEATURE [App::DocumentObjectGroupPython] G4_DNA_ADENINE  # scripted group (container) (typed FeaturePython)
  Dunit = g/cm3
  Dvalue = 1
  Group = -> [H_element124,C_element134,N_element054]
  conduct = 2
  density = 1
  expand = 3
  formula = G4_DNA_ADENINE
  name = G4_DNA_ADENINE
  specific = 4
FEATURE [App::DocumentObjectGroupPython] H_element125  label="H_element : 072"  # scripted group (container) (typed FeaturePython)
  n = 4
  ref = H_element
FEATURE [App::DocumentObjectGroupPython] C_element135  label="C_element : 080"  # scripted group (container) (typed FeaturePython)
  n = 5
  ref = C_element
FEATURE [App::DocumentObjectGroupPython] N_element055  label="N_element : 027"  # scripted group (container) (typed FeaturePython)
  n = 5
  ref = N_element
FEATURE [App::DocumentObjectGroupPython] O_element116  label="O_element : 069"  # scripted group (container) (typed FeaturePython)
  n = 1
  ref = O_element
FEATURE [App::DocumentObjectGroupPython] G4_DNA_GUANINE  # scripted group (container) (typed FeaturePython)
  Dunit = g/cm3
  Dvalue = 1
  Group = -> [H_element125,C_element135,N_element055,O_element116]
  conduct = 2
  density = 1
  expand = 3
  formula = G4_DNA_GUANINE
  name = G4_DNA_GUANINE
  specific = 4
FEATURE [App::DocumentObjectGroupPython] H_element126  label="H_element : 073"  # scripted group (container) (typed FeaturePython)
  n = 4
  ref = H_element
FEATURE [App::DocumentObjectGroupPython] C_element136  label="C_element : 081"  # scripted group (container) (typed FeaturePython)
  n = 4
  ref = C_element
FEATURE [App::DocumentObjectGroupPython] N_element056  label="N_element : 028"  # scripted group (container) (typed FeaturePython)
  n = 3
  ref = N_element
FEATURE [App::DocumentObjectGroupPython] O_element117  label="O_element : 070"  # scripted group (container) (typed FeaturePython)
  n = 1
  ref = O_element
FEATURE [App::DocumentObjectGroupPython] G4_DNA_CYTOSINE  # scripted group (container) (typed FeaturePython)
  Dunit = g/cm3
  Dvalue = 1
  Group = -> [H_element126,C_element136,N_element056,O_element117]
  conduct = 2
  density = 1
  expand = 3
  formula = G4_DNA_CYTOSINE
  name = G4_DNA_CYTOSINE
  specific = 4
FEATURE [App::DocumentObjectGroupPython] H_element127  label="H_element : 074"  # scripted group (container) (typed FeaturePython)
  n = 5
  ref = H_element
FEATURE [App::DocumentObjectGroupPython] C_element137  label="C_element : 082"  # scripted group (container) (typed FeaturePython)
  n = 5
  ref = C_element
FEATURE [App::DocumentObjectGroupPython] N_element057  label="N_element : 029"  # scripted group (container) (typed FeaturePython)
  n = 2
  ref = N_element
FEATURE [App::DocumentObjectGroupPython] O_element118  label="O_element : 071"  # scripted group (container) (typed FeaturePython)
  n = 2
  ref = O_element
FEATURE [App::DocumentObjectGroupPython] G4_DNA_THYMINE  # scripted group (container) (typed FeaturePython)
  Dunit = g/cm3
  Dvalue = 1
  Group = -> [H_element127,C_element137,N_element057,O_element118]
  conduct = 2
  density = 1
  expand = 3
  formula = G4_DNA_THYMINE
  name = G4_DNA_THYMINE
  specific = 4
FEATURE [App::DocumentObjectGroupPython] H_element128  label="H_element : 075"  # scripted group (container) (typed FeaturePython)
  n = 3
  ref = H_element
FEATURE [App::DocumentObjectGroupPython] C_element138  label="C_element : 083"  # scripted group (container) (typed FeaturePython)
  n = 4
  ref = C_element
FEATURE [App::DocumentObjectGroupPython] N_element058  label="N_element : 030"  # scripted group (container) (typed FeaturePython)
  n = 2
  ref = N_element
FEATURE [App::DocumentObjectGroupPython] O_element119  label="O_element : 072"  # scripted group (container) (typed FeaturePython)
  n = 2
  ref = O_element
FEATURE [App::DocumentObjectGroupPython] G4_DNA_URACIL  # scripted group (container) (typed FeaturePython)
  Dunit = g/cm3
  Dvalue = 1
  Group = -> [H_element128,C_element138,N_element058,O_element119]
  conduct = 2
  density = 1
  expand = 3
  formula = G4_DNA_URACIL
  name = G4_DNA_URACIL
  specific = 4
FEATURE [App::DocumentObjectGroupPython] H_element129  label="H_element : 076"  # scripted group (container) (typed FeaturePython)
  n = 10
  ref = H_element
FEATURE [App::DocumentObjectGroupPython] C_element139  label="C_element : 084"  # scripted group (container) (typed FeaturePython)
  n = 10
  ref = C_element
FEATURE [App::DocumentObjectGroupPython] N_element059  label="N_element : 031"  # scripted group (container) (typed FeaturePython)
  n = 5
  ref = N_element
FEATURE [App::DocumentObjectGroupPython] O_element120  label="O_element : 073"  # scripted group (container) (typed FeaturePython)
  n = 4
  ref = O_element
FEATURE [App::DocumentObjectGroupPython] G4_DNA_ADENOSINE  # scripted group (container) (typed FeaturePython)
  Dunit = g/cm3
  Dvalue = 1
  Group = -> [H_element129,C_element139,N_element059,O_element120]
  conduct = 2
  density = 1
  expand = 3
  formula = G4_DNA_ADENOSINE
  name = G4_DNA_ADENOSINE
  specific = 4
FEATURE [App::DocumentObjectGroupPython] H_element130  label="H_element : 077"  # scripted group (container) (typed FeaturePython)
  n = 10
  ref = H_element
FEATURE [App::DocumentObjectGroupPython] C_element140  label="C_element : 085"  # scripted group (container) (typed FeaturePython)
  n = 10
  ref = C_element
FEATURE [App::DocumentObjectGroupPython] N_element060  label="N_element : 032"  # scripted group (container) (typed FeaturePython)
  n = 5
  ref = N_element
FEATURE [App::DocumentObjectGroupPython] O_element121  label="O_element : 074"  # scripted group (container) (typed FeaturePython)
  n = 5
  ref = O_element
FEATURE [App::DocumentObjectGroupPython] G4_DNA_GUANOSINE  # scripted group (container) (typed FeaturePython)
  Dunit = g/cm3
  Dvalue = 1
  Group = -> [H_element130,C_element140,N_element060,O_element121]
  conduct = 2
  density = 1
  expand = 3
  formula = G4_DNA_GUANOSINE
  name = G4_DNA_GUANOSINE
  specific = 4
FEATURE [App::DocumentObjectGroupPython] H_element131  label="H_element : 078"  # scripted group (container) (typed FeaturePython)
  n = 10
  ref = H_element
FEATURE [App::DocumentObjectGroupPython] C_element141  label="C_element : 086"  # scripted group (container) (typed FeaturePython)
  n = 9
  ref = C_element
FEATURE [App::DocumentObjectGroupPython] N_element061  label="N_element : 033"  # scripted group (container) (typed FeaturePython)
  n = 3
  ref = N_element
FEATURE [App::DocumentObjectGroupPython] O_element122  label="O_element : 075"  # scripted group (container) (typed FeaturePython)
  n = 5
  ref = O_element
FEATURE [App::DocumentObjectGroupPython] G4_DNA_CYTIDINE  # scripted group (container) (typed FeaturePython)
  Dunit = g/cm3
  Dvalue = 1
  Group = -> [H_element131,C_element141,N_element061,O_element122]
  conduct = 2
  density = 1
  expand = 3
  formula = G4_DNA_CYTIDINE
  name = G4_DNA_CYTIDINE
  specific = 4
FEATURE [App::DocumentObjectGroupPython] H_element132  label="H_element : 079"  # scripted group (container) (typed FeaturePython)
  n = 9
  ref = H_element
FEATURE [App::DocumentObjectGroupPython] C_element142  label="C_element : 087"  # scripted group (container) (typed FeaturePython)
  n = 9
  ref = C_element
FEATURE [App::DocumentObjectGroupPython] N_element062  label="N_element : 034"  # scripted group (container) (typed FeaturePython)
  n = 2
  ref = N_element
FEATURE [App::DocumentObjectGroupPython] O_element123  label="O_element : 076"  # scripted group (container) (typed FeaturePython)
  n = 6
  ref = O_element
FEATURE [App::DocumentObjectGroupPython] G4_DNA_URIDINE  # scripted group (container) (typed FeaturePython)
  Dunit = g/cm3
  Dvalue = 1
  Group = -> [H_element132,C_element142,N_element062,O_element123]
  conduct = 2
  density = 1
  expand = 3
  formula = G4_DNA_URIDINE
  name = G4_DNA_URIDINE
  specific = 4
FEATURE [App::DocumentObjectGroupPython] H_element133  label="H_element : 080"  # scripted group (container) (typed FeaturePython)
  n = 11
  ref = H_element
FEATURE [App::DocumentObjectGroupPython] C_element143  label="C_element : 088"  # scripted group (container) (typed FeaturePython)
  n = 10
  ref = C_element
FEATURE [App::DocumentObjectGroupPython] N_element063  label="N_element : 035"  # scripted group (container) (typed FeaturePython)
  n = 2
  ref = N_element
FEATURE [App::DocumentObjectGroupPython] O_element124  label="O_element : 077"  # scripted group (container) (typed FeaturePython)
  n = 6
  ref = O_element
FEATURE [App::DocumentObjectGroupPython] G4_DNA_METHYLURIDINE  # scripted group (container) (typed FeaturePython)
  Dunit = g/cm3
  Dvalue = 1
  Group = -> [H_element133,C_element143,N_element063,O_element124]
  conduct = 2
  density = 1
  expand = 3
  formula = G4_DNA_METHYLURIDINE
  name = G4_DNA_METHYLURIDINE
  specific = 4
FEATURE [App::DocumentObjectGroupPython] P_element014  label="P_element : 003"  # scripted group (container) (typed FeaturePython)
  n = 1
  ref = P_element
FEATURE [App::DocumentObjectGroupPython] O_element125  label="O_element : 078"  # scripted group (container) (typed FeaturePython)
  n = 3
  ref = O_element
FEATURE [App::DocumentObjectGroupPython] G4_DNA_MONOPHOSPHATE  # scripted group (container) (typed FeaturePython)
  Dunit = g/cm3
  Dvalue = 1
  Group = -> [P_element014,O_element125]
  conduct = 2
  density = 1
  expand = 3
  formula = G4_DNA_MONOPHOSPHATE
  name = G4_DNA_MONOPHOSPHATE
  specific = 4
FEATURE [App::DocumentObjectGroupPython] H_element134  label="H_element : 081"  # scripted group (container) (typed FeaturePython)
  n = 10
  ref = H_element
FEATURE [App::DocumentObjectGroupPython] C_element144  label="C_element : 089"  # scripted group (container) (typed FeaturePython)
  n = 10
  ref = C_element
FEATURE [App::DocumentObjectGroupPython] N_element064  label="N_element : 036"  # scripted group (container) (typed FeaturePython)
  n = 5
  ref = N_element
FEATURE [App::DocumentObjectGroupPython] O_element126  label="O_element : 079"  # scripted group (container) (typed FeaturePython)
  n = 7
  ref = O_element
FEATURE [App::DocumentObjectGroupPython] P_element015  label="P_element : 004"  # scripted group (container) (typed FeaturePython)
  n = 1
  ref = P_element
FEATURE [App::DocumentObjectGroupPython] G4_DNA_A  # scripted group (container) (typed FeaturePython)
  Dunit = g/cm3
  Dvalue = 1
  Group = -> [H_element134,C_element144,N_element064,O_element126,P_element015]
  conduct = 2
  density = 1
  expand = 3
  formula = G4_DNA_A
  name = G4_DNA_A
  specific = 4
FEATURE [App::DocumentObjectGroupPython] H_element135  label="H_element : 082"  # scripted group (container) (typed FeaturePython)
  n = 10
  ref = H_element
FEATURE [App::DocumentObjectGroupPython] C_element145  label="C_element : 090"  # scripted group (container) (typed FeaturePython)
  n = 10
  ref = C_element
FEATURE [App::DocumentObjectGroupPython] N_element065  label="N_element : 037"  # scripted group (container) (typed FeaturePython)
  n = 5
  ref = N_element
FEATURE [App::DocumentObjectGroupPython] O_element127  label="O_element : 8"  # scripted group (container) (typed FeaturePython)
  n = 8
  ref = O_element
FEATURE [App::DocumentObjectGroupPython] P_element016  label="P_element : 005"  # scripted group (container) (typed FeaturePython)
  n = 1
  ref = P_element
FEATURE [App::DocumentObjectGroupPython] G4_DNA_G  # scripted group (container) (typed FeaturePython)
  Dunit = g/cm3
  Dvalue = 1
  Group = -> [H_element135,C_element145,N_element065,O_element127,P_element016]
  conduct = 2
  density = 1
  expand = 3
  formula = G4_DNA_G
  name = G4_DNA_G
  specific = 4
FEATURE [App::DocumentObjectGroupPython] H_element136  label="H_element : 083"  # scripted group (container) (typed FeaturePython)
  n = 10
  ref = H_element
FEATURE [App::DocumentObjectGroupPython] C_element146  label="C_element : 091"  # scripted group (container) (typed FeaturePython)
  n = 9
  ref = C_element
FEATURE [App::DocumentObjectGroupPython] N_element066  label="N_element : 038"  # scripted group (container) (typed FeaturePython)
  n = 3
  ref = N_element
FEATURE [App::DocumentObjectGroupPython] O_element128  label="O_element : 080"  # scripted group (container) (typed FeaturePython)
  n = 8
  ref = O_element
FEATURE [App::DocumentObjectGroupPython] P_element017  label="P_element : 006"  # scripted group (container) (typed FeaturePython)
  n = 1
  ref = P_element
FEATURE [App::DocumentObjectGroupPython] G4_DNA_C  # scripted group (container) (typed FeaturePython)
  Dunit = g/cm3
  Dvalue = 1
  Group = -> [H_element136,C_element146,N_element066,O_element128,P_element017]
  conduct = 2
  density = 1
  expand = 3
  formula = G4_DNA_C
  name = G4_DNA_C
  specific = 4
FEATURE [App::DocumentObjectGroupPython] H_element137  label="H_element : 084"  # scripted group (container) (typed FeaturePython)
  n = 9
  ref = H_element
FEATURE [App::DocumentObjectGroupPython] C_element147  label="C_element : 092"  # scripted group (container) (typed FeaturePython)
  n = 9
  ref = C_element
FEATURE [App::DocumentObjectGroupPython] N_element067  label="N_element : 039"  # scripted group (container) (typed FeaturePython)
  n = 2
  ref = N_element
FEATURE [App::DocumentObjectGroupPython] O_element129  label="O_element : 9"  # scripted group (container) (typed FeaturePython)
  n = 9
  ref = O_element
FEATURE [App::DocumentObjectGroupPython] P_element018  label="P_element : 007"  # scripted group (container) (typed FeaturePython)
  n = 1
  ref = P_element
FEATURE [App::DocumentObjectGroupPython] G4_DNA_U  # scripted group (container) (typed FeaturePython)
  Dunit = g/cm3
  Dvalue = 1
  Group = -> [H_element137,C_element147,N_element067,O_element129,P_element018]
  conduct = 2
  density = 1
  expand = 3
  formula = G4_DNA_U
  name = G4_DNA_U
  specific = 4
FEATURE [App::DocumentObjectGroupPython] H_element138  label="H_element : 085"  # scripted group (container) (typed FeaturePython)
  n = 11
  ref = H_element
FEATURE [App::DocumentObjectGroupPython] C_element148  label="C_element : 093"  # scripted group (container) (typed FeaturePython)
  n = 10
  ref = C_element
FEATURE [App::DocumentObjectGroupPython] N_element068  label="N_element : 040"  # scripted group (container) (typed FeaturePython)
  n = 2
  ref = N_element
FEATURE [App::DocumentObjectGroupPython] O_element130  label="O_element : 081"  # scripted group (container) (typed FeaturePython)
  n = 9
  ref = O_element
FEATURE [App::DocumentObjectGroupPython] P_element019  label="P_element : 008"  # scripted group (container) (typed FeaturePython)
  n = 1
  ref = P_element
FEATURE [App::DocumentObjectGroupPython] G4_DNA_MU  # scripted group (container) (typed FeaturePython)
  Dunit = g/cm3
  Dvalue = 1
  Group = -> [H_element138,C_element148,N_element068,O_element130,P_element019]
  conduct = 2
  density = 1
  expand = 3
  formula = G4_DNA_MU
  name = G4_DNA_MU
  specific = 4
FEATURE [App::DocumentObjectGroupPython] BioChemical  # scripted group (container) (typed FeaturePython)
  Group = -> [G4_CYTOSINE,G4_THYMINE,G4_URACIL,G4_DNA_ADENINE,G4_DNA_GUANINE,G4_DNA_CYTOSINE,G4_DNA_THYMINE,G4_DNA_URACIL,G4_DNA_ADENOSINE,G4_DNA_GUANOSINE,G4_DNA_CYTIDINE,G4_DNA_URIDINE,G4_DNA_METHYLURIDINE,G4_DNA_MONOPHOSPHATE,G4_DNA_A,G4_DNA_G,G4_DNA_C,G4_DNA_U,G4_DNA_MU]
FEATURE [App::DocumentObjectGroupPython] G4Materials  # scripted group (container) (typed FeaturePython)
  Group = -> [NIST,Element,HEP,Space,BioChemical]
  version = 1
FEATURE [App::DocumentObjectGroupPython] Geant4  # scripted group (container) (typed FeaturePython)
  Group = -> [G4Isotopes,G4Elements,G4Materials]
FEATURE [App::DocumentObjectGroupPython] Materials  # scripted group (container) (typed FeaturePython)
  Group = -> [Geant4]
FEATURE [Part::FeaturePython] GDMLBox_WorldBox  # WARN: FeaturePython — macro-defined, semantics opaque (R4)
  lunit = 2
  material = 5
  x = 780
  y = 780
  z = 780
FEATURE [Part::Box] Box  label="Interposer"
  AttacherType = Attacher::AttachEngine3D
  Height = 10
  Length = 10
  Width = 10
FEATURE [Part::Box] Box001  label="ImageArea"
  AttacherType = Attacher::AttachEngine3D
  Height = 10
  Length = 10
  Placement = pos=(15,0,0) rot=(0,0,1;0rad)
  Width = 10
FEATURE [Part::Box] Box002  label="FrameStore"
  AttacherType = Attacher::AttachEngine3D
  Height = 10
  Length = 10
  Placement = pos=(28,0,0) rot=(0,0,1;0rad)
  Width = 10
FEATURE [Part::Box] Box003  label="Fiducial"
  AttacherType = Attacher::AttachEngine3D
  Height = 10
  Length = 10
  Placement = pos=(0,16,0) rot=(0,0,1;0rad)
  Width = 10
FEATURE [Part::FeaturePython] Array  label="Interposer_array"  # Draft array (typed FeaturePython)
  AlwaysSyncPlacement = false
  Angle = 360
  ArrayType = 0
  Axis = (0,0,1)
  Base = -> Box
  Center = (0,0,0)
  Count = 4
  ExpandArray = false
  Fuse = false
  IntervalAxis = (0,0,0)
  IntervalX = (100,0,0)
  IntervalY = (0,100,0)
  IntervalZ = (0,0,100)
  NumberCircles = 3
  NumberPolar = 5
  NumberX = 2
  NumberY = 2
  NumberZ = 1
  PlacementList = 4 placements: [(0,0,0),(0,100,0),(100,0,0),(100,100,0)]
  RadialDistance = 50
  ScaleList = (4) [(1,1,1),(1,1,1),(1,1,1),(1,1,1)]
  Symmetry = 1
  TangentialDistance = 25
FEATURE [Part::FeaturePython] Array001  label="ImageArray_array"  # Draft array (typed FeaturePython)
  AlwaysSyncPlacement = false
  Angle = 360
  ArrayType = 0
  Axis = (0,0,1)
  Base = -> Box001
  Center = (0,0,0)
  Count = 4
  ExpandArray = false
  Fuse = false
  IntervalAxis = (0,0,0)
  IntervalX = (100,0,0)
  IntervalY = (0,100,0)
  IntervalZ = (0,0,100)
  NumberCircles = 3
  NumberPolar = 5
  NumberX = 2
  NumberY = 2
  NumberZ = 1
  PlacementList = 4 placements: [(15,0,0),(15,100,0),(115,0,0),(115,100,0)]
  RadialDistance = 50
  ScaleList = (4) [(1,1,1),(1,1,1),(1,1,1),(1,1,1)]
  Symmetry = 1
  TangentialDistance = 25
FEATURE [Part::FeaturePython] Array002  label="framestore_arary"  # Draft array (typed FeaturePython)
  AlwaysSyncPlacement = false
  Angle = 360
  ArrayType = 0
  Axis = (0,0,1)
  Base = -> Box002
  Center = (0,0,0)
  Count = 4
  ExpandArray = false
  Fuse = false
  IntervalAxis = (0,0,0)
  IntervalX = (100,0,0)
  IntervalY = (0,100,0)
  IntervalZ = (0,0,100)
  NumberCircles = 3
  NumberPolar = 5
  NumberX = 2
  NumberY = 2
  NumberZ = 1
  PlacementList = 4 placements: [(28,0,0),(28,100,0),(128,0,0),(128,100,0)]
  RadialDistance = 50
  ScaleList = (4) [(1,1,1),(1,1,1),(1,1,1),(1,1,1)]
  Symmetry = 1
  TangentialDistance = 25
FEATURE [Part::FeaturePython] Array003  label="fiducialarray"  # Draft array (typed FeaturePython)
  AlwaysSyncPlacement = false
  Angle = 360
  ArrayType = 0
  Axis = (0,0,1)
  Base = -> Box003
  Center = (0,0,0)
  Count = 4
  ExpandArray = false
  Fuse = false
  IntervalAxis = (0,0,0)
  IntervalX = (100,0,0)
  IntervalY = (0,100,0)
  IntervalZ = (0,0,100)
  NumberCircles = 3
  NumberPolar = 5
  NumberX = 2
  NumberY = 2
  NumberZ = 1
  PlacementList = 4 placements: [(0,16,0),(0,116,0),(100,16,0),(100,116,0)]
  RadialDistance = 50
  ScaleList = (4) [(1,1,1),(1,1,1),(1,1,1),(1,1,1)]
  Symmetry = 1
  TangentialDistance = 25
FEATURE [Part::FeaturePython] GDMLSphere  # WARN: FeaturePython — macro-defined, semantics opaque (R4)
  aunit = 1
  deltaphi = 360
  deltatheta = 180
  lunit = 2
  material = 0
  rmax = 300
  rmin = 290
  startphi = 0
  starttheta = 0
FEATURE [App::Part] Part001  label="Interposer001"
  Group = -> [Box,Array]
  Origin = -> Origin003
FEATURE [App::Part] Part002  label="ImageArea001"
  Group = -> [Box001,Array001]
  Origin = -> Origin004
FEATURE [App::Part] Part003  label="FrameStore001"
  Group = -> [Box002,Array002]
  Origin = -> Origin005
FEATURE [App::Part] Part004  label="fiducial"
  Group = -> [Box003,Array003]
  Origin = -> Origin006
FEATURE [App::Part] LV_Sphere
  Group = -> [GDMLSphere,Part004,Part003,Part002,Part001]
  Origin = -> Origin002
  SkinSurface = 0
FEATURE [App::Part] Part  label="Experiment"
  Group = -> [LV_Sphere]
  Origin = -> Origin001
FEATURE [App::Part] worldVOL
  Group = -> [GDMLBox_WorldBox,Part]
  Origin = -> Origin
